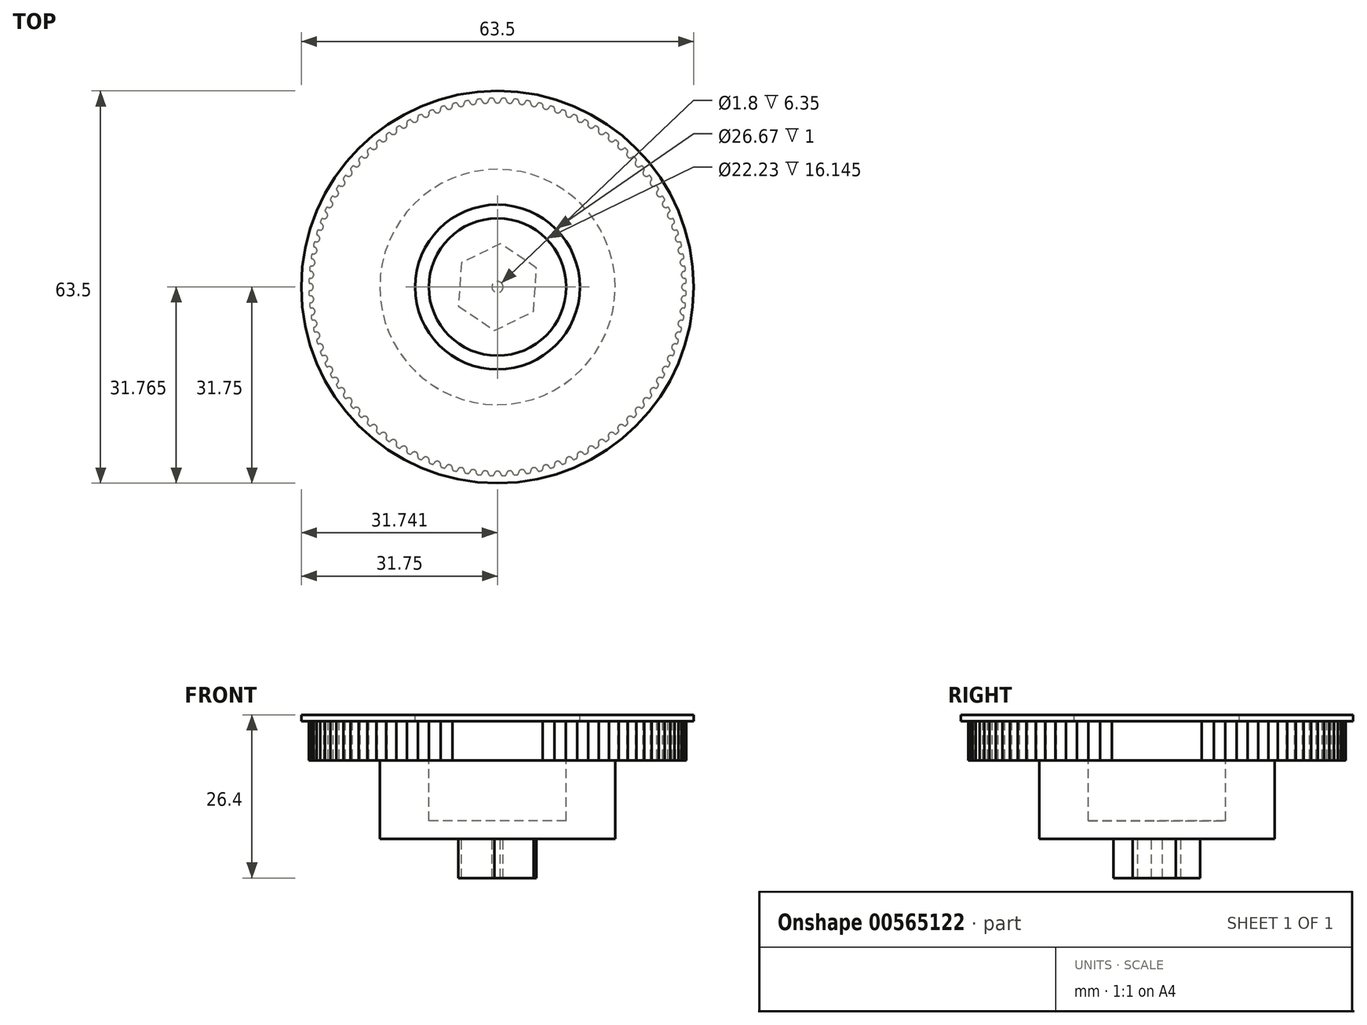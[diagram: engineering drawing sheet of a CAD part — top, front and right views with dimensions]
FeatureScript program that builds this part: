
annotation { "Feature Type Name" : "Feature", "Feature Type Description" : "" }
export const myFeature = defineFeature(function(context is Context, id is Id, definition is map)
    precondition{}
    {
        {
            var Q0;
            Q0=qCreatedBy(makeId("Top.planeOp"),FACE);
            var sketch = newSketch(context, id + "F0", { "sketchPlane" : qUnion([Q0])});
            skArc(sketch, "E0", {"start": v(0, 29.8) * mm, "mid": v(0.3, 29.9) * mm, "end": v(0.5, 30.12) * mm});
            skArc(sketch, "E1", {"start": v(1.47, 30.1) * mm, "mid": v(1.66, 29.85) * mm, "end": v(1.95, 29.74) * mm});
            skArc(sketch, "E2", {"start": v(0.5, 30.12) * mm, "mid": v(0.55, 30.23) * mm, "end": v(0.58, 30.34) * mm});
            skArc(sketch, "E3", {"start": v(1.4, 30.32) * mm, "mid": v(1.43, 30.2) * mm, "end": v(1.47, 30.1) * mm});
            skArc(sketch, "E4.trimOffspring", {"start": v(1.17, 30.53) * mm, "mid": v(1, 30.54) * mm, "end": v(0.83, 30.54) * mm});
            skPoint(sketch, "E5.visualSharp", {"position": v(0.6, 30.55) * mm});
            skArc(sketch, "E5.filletArc", {"start": v(0.83, 30.54) * mm, "mid": v(0.67, 30.5) * mm, "end": v(0.58, 30.34) * mm});
            skPoint(sketch, "E6.visualSharp", {"position": v(1.4, 30.52) * mm});
            skArc(sketch, "E6.filletArc", {"start": v(1.4, 30.32) * mm, "mid": v(1.33, 30.47) * mm, "end": v(1.17, 30.53) * mm});
            skArc(sketch, "E7.1.0", {"start": v(-1.95, 29.74) * mm, "mid": v(-1.66, 29.85) * mm, "end": v(-1.47, 30.1) * mm});
            skArc(sketch, "E7.1.1", {"start": v(-1.47, 30.1) * mm, "mid": v(-1.43, 30.2) * mm, "end": v(-1.4, 30.32) * mm});
            skArc(sketch, "E7.1.2", {"start": v(-1.17, 30.53) * mm, "mid": v(-1.33, 30.47) * mm, "end": v(-1.4, 30.32) * mm});
            skArc(sketch, "E7.1.3", {"start": v(-0.83, 30.54) * mm, "mid": v(-1, 30.54) * mm, "end": v(-1.17, 30.53) * mm});
            skArc(sketch, "E7.1.4", {"start": v(-0.58, 30.34) * mm, "mid": v(-0.67, 30.5) * mm, "end": v(-0.83, 30.54) * mm});
            skArc(sketch, "E7.1.5", {"start": v(-0.58, 30.34) * mm, "mid": v(-0.55, 30.23) * mm, "end": v(-0.5, 30.12) * mm});
            skArc(sketch, "E7.1.6", {"start": v(-0.5, 30.12) * mm, "mid": v(-0.3, 29.9) * mm, "end": v(0, 29.8) * mm});
            skArc(sketch, "E7.2.0", {"start": v(-3.9, 29.55) * mm, "mid": v(-3.6, 29.68) * mm, "end": v(-3.44, 29.93) * mm});
            skArc(sketch, "E7.2.1", {"start": v(-3.44, 29.93) * mm, "mid": v(-3.4, 30.04) * mm, "end": v(-3.39, 30.16) * mm});
            skArc(sketch, "E7.2.2", {"start": v(-3.16, 30.4) * mm, "mid": v(-3.32, 30.32) * mm, "end": v(-3.39, 30.16) * mm});
            skArc(sketch, "E7.2.3", {"start": v(-2.83, 30.43) * mm, "mid": v(-3, 30.4) * mm, "end": v(-3.16, 30.4) * mm});
            skArc(sketch, "E7.2.4", {"start": v(-2.56, 30.24) * mm, "mid": v(-2.66, 30.38) * mm, "end": v(-2.83, 30.43) * mm});
            skArc(sketch, "E7.2.5", {"start": v(-2.56, 30.24) * mm, "mid": v(-2.52, 30.13) * mm, "end": v(-2.47, 30.03) * mm});
            skArc(sketch, "E7.2.6", {"start": v(-2.47, 30.03) * mm, "mid": v(-2.25, 29.8) * mm, "end": v(-1.95, 29.74) * mm});
            skArc(sketch, "E7.3.0", {"start": v(-5.82, 29.23) * mm, "mid": v(-5.54, 29.38) * mm, "end": v(-5.39, 29.64) * mm});
            skArc(sketch, "E7.3.1", {"start": v(-5.39, 29.64) * mm, "mid": v(-5.36, 29.76) * mm, "end": v(-5.35, 29.87) * mm});
            skArc(sketch, "E7.3.2", {"start": v(-5.14, 30.12) * mm, "mid": v(-5.3, 30.04) * mm, "end": v(-5.35, 29.87) * mm});
            skArc(sketch, "E7.3.3", {"start": v(-4.81, 30.18) * mm, "mid": v(-4.98, 30.15) * mm, "end": v(-5.14, 30.12) * mm});
            skArc(sketch, "E7.3.4", {"start": v(-4.53, 30) * mm, "mid": v(-4.64, 30.14) * mm, "end": v(-4.81, 30.18) * mm});
            skArc(sketch, "E7.3.5", {"start": v(-4.53, 30) * mm, "mid": v(-4.49, 29.9) * mm, "end": v(-4.43, 29.8) * mm});
            skArc(sketch, "E7.3.6", {"start": v(-4.43, 29.8) * mm, "mid": v(-4.2, 29.6) * mm, "end": v(-3.9, 29.55) * mm});
            skArc(sketch, "E7.4.0", {"start": v(-7.71, 28.8) * mm, "mid": v(-7.45, 28.95) * mm, "end": v(-7.31, 29.23) * mm});
            skArc(sketch, "E7.4.1", {"start": v(-7.31, 29.23) * mm, "mid": v(-7.3, 29.34) * mm, "end": v(-7.3, 29.46) * mm});
            skArc(sketch, "E7.4.2", {"start": v(-7.1, 29.72) * mm, "mid": v(-7.25, 29.62) * mm, "end": v(-7.3, 29.46) * mm});
            skArc(sketch, "E7.4.3", {"start": v(-6.77, 29.8) * mm, "mid": v(-6.94, 29.76) * mm, "end": v(-7.1, 29.72) * mm});
            skArc(sketch, "E7.4.4", {"start": v(-6.49, 29.65) * mm, "mid": v(-6.6, 29.77) * mm, "end": v(-6.77, 29.8) * mm});
            skArc(sketch, "E7.4.5", {"start": v(-6.49, 29.65) * mm, "mid": v(-6.43, 29.54) * mm, "end": v(-6.37, 29.45) * mm});
            skArc(sketch, "E7.4.6", {"start": v(-6.37, 29.45) * mm, "mid": v(-6.12, 29.26) * mm, "end": v(-5.82, 29.23) * mm});
            skArc(sketch, "E7.5.0", {"start": v(-9.58, 28.23) * mm, "mid": v(-9.33, 28.4) * mm, "end": v(-9.2, 28.69) * mm});
            skArc(sketch, "E7.5.1", {"start": v(-9.2, 28.69) * mm, "mid": v(-9.2, 28.8) * mm, "end": v(-9.2, 28.92) * mm});
            skArc(sketch, "E7.5.2", {"start": v(-9.03, 29.2) * mm, "mid": v(-9.17, 29.09) * mm, "end": v(-9.2, 28.92) * mm});
            skArc(sketch, "E7.5.3", {"start": v(-8.7, 29.29) * mm, "mid": v(-8.87, 29.24) * mm, "end": v(-9.03, 29.2) * mm});
            skArc(sketch, "E7.5.4", {"start": v(-8.41, 29.16) * mm, "mid": v(-8.54, 29.28) * mm, "end": v(-8.7, 29.29) * mm});
            skArc(sketch, "E7.5.5", {"start": v(-8.41, 29.16) * mm, "mid": v(-8.35, 29.06) * mm, "end": v(-8.28, 28.97) * mm});
            skArc(sketch, "E7.5.6", {"start": v(-8.28, 28.97) * mm, "mid": v(-8.02, 28.8) * mm, "end": v(-7.71, 28.8) * mm});
            skArc(sketch, "E7.6.0", {"start": v(-11.4, 27.54) * mm, "mid": v(-11.17, 27.73) * mm, "end": v(-11.06, 28.02) * mm});
            skArc(sketch, "E7.6.1", {"start": v(-11.06, 28.02) * mm, "mid": v(-11.07, 28.14) * mm, "end": v(-11.08, 28.25) * mm});
            skArc(sketch, "E7.6.2", {"start": v(-10.92, 28.54) * mm, "mid": v(-11.05, 28.43) * mm, "end": v(-11.08, 28.25) * mm});
            skArc(sketch, "E7.6.3", {"start": v(-10.6, 28.66) * mm, "mid": v(-10.76, 28.6) * mm, "end": v(-10.92, 28.54) * mm});
            skArc(sketch, "E7.6.4", {"start": v(-10.3, 28.55) * mm, "mid": v(-10.43, 28.66) * mm, "end": v(-10.6, 28.66) * mm});
            skArc(sketch, "E7.6.5", {"start": v(-10.3, 28.55) * mm, "mid": v(-10.23, 28.45) * mm, "end": v(-10.16, 28.36) * mm});
            skArc(sketch, "E7.6.6", {"start": v(-10.16, 28.36) * mm, "mid": v(-9.89, 28.21) * mm, "end": v(-9.58, 28.23) * mm});
            skArc(sketch, "E7.7.0", {"start": v(-13.18, 26.73) * mm, "mid": v(-12.96, 26.94) * mm, "end": v(-12.87, 27.24) * mm});
            skArc(sketch, "E7.7.1", {"start": v(-12.87, 27.24) * mm, "mid": v(-12.88, 27.35) * mm, "end": v(-12.9, 27.47) * mm});
            skArc(sketch, "E7.7.2", {"start": v(-12.76, 27.76) * mm, "mid": v(-12.89, 27.64) * mm, "end": v(-12.9, 27.47) * mm});
            skArc(sketch, "E7.7.3", {"start": v(-12.46, 27.9) * mm, "mid": v(-12.61, 27.83) * mm, "end": v(-12.76, 27.76) * mm});
            skArc(sketch, "E7.7.4", {"start": v(-12.14, 27.81) * mm, "mid": v(-12.29, 27.91) * mm, "end": v(-12.46, 27.9) * mm});
            skArc(sketch, "E7.7.5", {"start": v(-12.14, 27.81) * mm, "mid": v(-12.07, 27.72) * mm, "end": v(-12, 27.64) * mm});
            skArc(sketch, "E7.7.6", {"start": v(-12, 27.64) * mm, "mid": v(-11.71, 27.5) * mm, "end": v(-11.4, 27.54) * mm});
            skArc(sketch, "E7.8.0", {"start": v(-14.9, 25.81) * mm, "mid": v(-14.69, 26.04) * mm, "end": v(-14.63, 26.34) * mm});
            skArc(sketch, "E7.8.1", {"start": v(-14.63, 26.34) * mm, "mid": v(-14.64, 26.45) * mm, "end": v(-14.67, 26.57) * mm});
            skArc(sketch, "E7.8.2", {"start": v(-14.55, 26.87) * mm, "mid": v(-14.67, 26.74) * mm, "end": v(-14.67, 26.57) * mm});
            skArc(sketch, "E7.8.3", {"start": v(-14.26, 27.03) * mm, "mid": v(-14.4, 26.95) * mm, "end": v(-14.55, 26.87) * mm});
            skArc(sketch, "E7.8.4", {"start": v(-13.94, 26.96) * mm, "mid": v(-14.08, 27.05) * mm, "end": v(-14.26, 27.03) * mm});
            skArc(sketch, "E7.8.5", {"start": v(-13.94, 26.96) * mm, "mid": v(-13.86, 26.87) * mm, "end": v(-13.77, 26.8) * mm});
            skArc(sketch, "E7.8.6", {"start": v(-13.77, 26.8) * mm, "mid": v(-13.49, 26.68) * mm, "end": v(-13.18, 26.73) * mm});
            skArc(sketch, "E7.9.0", {"start": v(-16.56, 24.78) * mm, "mid": v(-16.36, 25.02) * mm, "end": v(-16.32, 25.32) * mm});
            skArc(sketch, "E7.9.1", {"start": v(-16.32, 25.32) * mm, "mid": v(-16.34, 25.44) * mm, "end": v(-16.38, 25.55) * mm});
            skArc(sketch, "E7.9.2", {"start": v(-16.28, 25.86) * mm, "mid": v(-16.38, 25.72) * mm, "end": v(-16.38, 25.55) * mm});
            skArc(sketch, "E7.9.3", {"start": v(-16, 26.04) * mm, "mid": v(-16.14, 25.95) * mm, "end": v(-16.28, 25.86) * mm});
            skArc(sketch, "E7.9.4", {"start": v(-15.67, 26) * mm, "mid": v(-15.82, 26.07) * mm, "end": v(-16, 26.04) * mm});
            skArc(sketch, "E7.9.5", {"start": v(-15.67, 26) * mm, "mid": v(-15.59, 25.9) * mm, "end": v(-15.5, 25.84) * mm});
            skArc(sketch, "E7.9.6", {"start": v(-15.5, 25.84) * mm, "mid": v(-15.2, 25.74) * mm, "end": v(-14.9, 25.81) * mm});
            skArc(sketch, "E7.10.0", {"start": v(-18.15, 23.65) * mm, "mid": v(-17.96, 23.9) * mm, "end": v(-17.94, 24.2) * mm});
            skArc(sketch, "E7.10.1", {"start": v(-17.94, 24.2) * mm, "mid": v(-17.97, 24.32) * mm, "end": v(-18.02, 24.42) * mm});
            skArc(sketch, "E7.10.2", {"start": v(-17.93, 24.74) * mm, "mid": v(-18.03, 24.6) * mm, "end": v(-18.02, 24.42) * mm});
            skArc(sketch, "E7.10.3", {"start": v(-17.66, 24.94) * mm, "mid": v(-17.8, 24.84) * mm, "end": v(-17.93, 24.74) * mm});
            skArc(sketch, "E7.10.4", {"start": v(-17.34, 24.91) * mm, "mid": v(-17.5, 24.98) * mm, "end": v(-17.66, 24.94) * mm});
            skArc(sketch, "E7.10.5", {"start": v(-17.34, 24.91) * mm, "mid": v(-17.25, 24.83) * mm, "end": v(-17.15, 24.77) * mm});
            skArc(sketch, "E7.10.6", {"start": v(-17.15, 24.77) * mm, "mid": v(-16.85, 24.7) * mm, "end": v(-16.56, 24.78) * mm});
            skArc(sketch, "E7.11.0", {"start": v(-19.65, 22.41) * mm, "mid": v(-19.49, 22.67) * mm, "end": v(-19.48, 22.98) * mm});
            skArc(sketch, "E7.11.1", {"start": v(-19.48, 22.98) * mm, "mid": v(-19.52, 23.09) * mm, "end": v(-19.57, 23.2) * mm});
            skArc(sketch, "E7.11.2", {"start": v(-19.51, 23.51) * mm, "mid": v(-19.6, 23.36) * mm, "end": v(-19.57, 23.2) * mm});
            skArc(sketch, "E7.11.3", {"start": v(-19.25, 23.73) * mm, "mid": v(-19.38, 23.62) * mm, "end": v(-19.51, 23.51) * mm});
            skArc(sketch, "E7.11.4", {"start": v(-18.93, 23.72) * mm, "mid": v(-19.1, 23.78) * mm, "end": v(-19.25, 23.73) * mm});
            skArc(sketch, "E7.11.5", {"start": v(-18.93, 23.72) * mm, "mid": v(-18.84, 23.65) * mm, "end": v(-18.74, 23.6) * mm});
            skArc(sketch, "E7.11.6", {"start": v(-18.74, 23.6) * mm, "mid": v(-18.43, 23.54) * mm, "end": v(-18.15, 23.65) * mm});
            skArc(sketch, "E7.12.0", {"start": v(-21.08, 21.08) * mm, "mid": v(-20.93, 21.35) * mm, "end": v(-20.95, 21.65) * mm});
            skArc(sketch, "E7.12.1", {"start": v(-20.95, 21.65) * mm, "mid": v(-21, 21.76) * mm, "end": v(-21.05, 21.86) * mm});
            skArc(sketch, "E7.12.2", {"start": v(-21.01, 22.19) * mm, "mid": v(-21.09, 22.03) * mm, "end": v(-21.05, 21.86) * mm});
            skArc(sketch, "E7.12.3", {"start": v(-20.76, 22.42) * mm, "mid": v(-20.89, 22.3) * mm, "end": v(-21.01, 22.19) * mm});
            skArc(sketch, "E7.12.4", {"start": v(-20.44, 22.43) * mm, "mid": v(-20.6, 22.48) * mm, "end": v(-20.76, 22.42) * mm});
            skArc(sketch, "E7.12.5", {"start": v(-20.44, 22.43) * mm, "mid": v(-20.34, 22.37) * mm, "end": v(-20.24, 22.32) * mm});
            skArc(sketch, "E7.12.6", {"start": v(-20.24, 22.32) * mm, "mid": v(-19.93, 22.28) * mm, "end": v(-19.65, 22.41) * mm});
            skArc(sketch, "E7.13.0", {"start": v(-22.41, 19.65) * mm, "mid": v(-22.28, 19.93) * mm, "end": v(-22.32, 20.24) * mm});
            skArc(sketch, "E7.13.1", {"start": v(-22.32, 20.24) * mm, "mid": v(-22.37, 20.34) * mm, "end": v(-22.43, 20.44) * mm});
            skArc(sketch, "E7.13.2", {"start": v(-22.42, 20.76) * mm, "mid": v(-22.48, 20.6) * mm, "end": v(-22.43, 20.44) * mm});
            skArc(sketch, "E7.13.3", {"start": v(-22.19, 21.01) * mm, "mid": v(-22.3, 20.89) * mm, "end": v(-22.42, 20.76) * mm});
            skArc(sketch, "E7.13.4", {"start": v(-21.86, 21.05) * mm, "mid": v(-22.03, 21.09) * mm, "end": v(-22.19, 21.01) * mm});
            skArc(sketch, "E7.13.5", {"start": v(-21.86, 21.05) * mm, "mid": v(-21.76, 21) * mm, "end": v(-21.65, 20.95) * mm});
            skArc(sketch, "E7.13.6", {"start": v(-21.65, 20.95) * mm, "mid": v(-21.35, 20.93) * mm, "end": v(-21.08, 21.08) * mm});
            skArc(sketch, "E7.14.0", {"start": v(-23.65, 18.15) * mm, "mid": v(-23.54, 18.43) * mm, "end": v(-23.6, 18.74) * mm});
            skArc(sketch, "E7.14.1", {"start": v(-23.6, 18.74) * mm, "mid": v(-23.65, 18.84) * mm, "end": v(-23.72, 18.93) * mm});
            skArc(sketch, "E7.14.2", {"start": v(-23.73, 19.25) * mm, "mid": v(-23.78, 19.1) * mm, "end": v(-23.72, 18.93) * mm});
            skArc(sketch, "E7.14.3", {"start": v(-23.51, 19.51) * mm, "mid": v(-23.62, 19.38) * mm, "end": v(-23.73, 19.25) * mm});
            skArc(sketch, "E7.14.4", {"start": v(-23.2, 19.57) * mm, "mid": v(-23.36, 19.6) * mm, "end": v(-23.51, 19.51) * mm});
            skArc(sketch, "E7.14.5", {"start": v(-23.2, 19.57) * mm, "mid": v(-23.09, 19.52) * mm, "end": v(-22.98, 19.48) * mm});
            skArc(sketch, "E7.14.6", {"start": v(-22.98, 19.48) * mm, "mid": v(-22.67, 19.49) * mm, "end": v(-22.41, 19.65) * mm});
            skArc(sketch, "E7.15.0", {"start": v(-24.78, 16.56) * mm, "mid": v(-24.7, 16.85) * mm, "end": v(-24.77, 17.15) * mm});
            skArc(sketch, "E7.15.1", {"start": v(-24.77, 17.15) * mm, "mid": v(-24.83, 17.25) * mm, "end": v(-24.91, 17.34) * mm});
            skArc(sketch, "E7.15.2", {"start": v(-24.94, 17.66) * mm, "mid": v(-24.98, 17.5) * mm, "end": v(-24.91, 17.34) * mm});
            skArc(sketch, "E7.15.3", {"start": v(-24.74, 17.93) * mm, "mid": v(-24.84, 17.8) * mm, "end": v(-24.94, 17.66) * mm});
            skArc(sketch, "E7.15.4", {"start": v(-24.42, 18.02) * mm, "mid": v(-24.6, 18.03) * mm, "end": v(-24.74, 17.93) * mm});
            skArc(sketch, "E7.15.5", {"start": v(-24.42, 18.02) * mm, "mid": v(-24.32, 17.97) * mm, "end": v(-24.2, 17.94) * mm});
            skArc(sketch, "E7.15.6", {"start": v(-24.2, 17.94) * mm, "mid": v(-23.9, 17.96) * mm, "end": v(-23.65, 18.15) * mm});
            skArc(sketch, "E7.16.0", {"start": v(-25.81, 14.9) * mm, "mid": v(-25.74, 15.2) * mm, "end": v(-25.84, 15.5) * mm});
            skArc(sketch, "E7.16.1", {"start": v(-25.84, 15.5) * mm, "mid": v(-25.9, 15.59) * mm, "end": v(-26, 15.67) * mm});
            skArc(sketch, "E7.16.2", {"start": v(-26.04, 16) * mm, "mid": v(-26.07, 15.82) * mm, "end": v(-26, 15.67) * mm});
            skArc(sketch, "E7.16.3", {"start": v(-25.86, 16.28) * mm, "mid": v(-25.95, 16.14) * mm, "end": v(-26.04, 16) * mm});
            skArc(sketch, "E7.16.4", {"start": v(-25.55, 16.38) * mm, "mid": v(-25.72, 16.38) * mm, "end": v(-25.86, 16.28) * mm});
            skArc(sketch, "E7.16.5", {"start": v(-25.55, 16.38) * mm, "mid": v(-25.44, 16.34) * mm, "end": v(-25.32, 16.32) * mm});
            skArc(sketch, "E7.16.6", {"start": v(-25.32, 16.32) * mm, "mid": v(-25.02, 16.36) * mm, "end": v(-24.78, 16.56) * mm});
            skArc(sketch, "E7.17.0", {"start": v(-26.73, 13.18) * mm, "mid": v(-26.68, 13.49) * mm, "end": v(-26.8, 13.77) * mm});
            skArc(sketch, "E7.17.1", {"start": v(-26.8, 13.77) * mm, "mid": v(-26.87, 13.86) * mm, "end": v(-26.96, 13.94) * mm});
            skArc(sketch, "E7.17.2", {"start": v(-27.03, 14.26) * mm, "mid": v(-27.05, 14.08) * mm, "end": v(-26.96, 13.94) * mm});
            skArc(sketch, "E7.17.3", {"start": v(-26.87, 14.55) * mm, "mid": v(-26.95, 14.4) * mm, "end": v(-27.03, 14.26) * mm});
            skArc(sketch, "E7.17.4", {"start": v(-26.57, 14.67) * mm, "mid": v(-26.74, 14.67) * mm, "end": v(-26.87, 14.55) * mm});
            skArc(sketch, "E7.17.5", {"start": v(-26.57, 14.67) * mm, "mid": v(-26.45, 14.64) * mm, "end": v(-26.34, 14.63) * mm});
            skArc(sketch, "E7.17.6", {"start": v(-26.34, 14.63) * mm, "mid": v(-26.04, 14.69) * mm, "end": v(-25.81, 14.9) * mm});
            skArc(sketch, "E7.18.0", {"start": v(-27.54, 11.4) * mm, "mid": v(-27.5, 11.71) * mm, "end": v(-27.64, 12) * mm});
            skArc(sketch, "E7.18.1", {"start": v(-27.64, 12) * mm, "mid": v(-27.72, 12.07) * mm, "end": v(-27.81, 12.14) * mm});
            skArc(sketch, "E7.18.2", {"start": v(-27.9, 12.46) * mm, "mid": v(-27.91, 12.29) * mm, "end": v(-27.81, 12.14) * mm});
            skArc(sketch, "E7.18.3", {"start": v(-27.76, 12.76) * mm, "mid": v(-27.83, 12.61) * mm, "end": v(-27.9, 12.46) * mm});
            skArc(sketch, "E7.18.4", {"start": v(-27.47, 12.9) * mm, "mid": v(-27.64, 12.89) * mm, "end": v(-27.76, 12.76) * mm});
            skArc(sketch, "E7.18.5", {"start": v(-27.47, 12.9) * mm, "mid": v(-27.35, 12.88) * mm, "end": v(-27.24, 12.87) * mm});
            skArc(sketch, "E7.18.6", {"start": v(-27.24, 12.87) * mm, "mid": v(-26.94, 12.96) * mm, "end": v(-26.73, 13.18) * mm});
            skArc(sketch, "E7.19.0", {"start": v(-28.23, 9.58) * mm, "mid": v(-28.21, 9.89) * mm, "end": v(-28.36, 10.16) * mm});
            skArc(sketch, "E7.19.1", {"start": v(-28.36, 10.16) * mm, "mid": v(-28.45, 10.23) * mm, "end": v(-28.55, 10.3) * mm});
            skArc(sketch, "E7.19.2", {"start": v(-28.66, 10.6) * mm, "mid": v(-28.66, 10.43) * mm, "end": v(-28.55, 10.3) * mm});
            skArc(sketch, "E7.19.3", {"start": v(-28.54, 10.92) * mm, "mid": v(-28.6, 10.76) * mm, "end": v(-28.66, 10.6) * mm});
            skArc(sketch, "E7.19.4", {"start": v(-28.25, 11.08) * mm, "mid": v(-28.43, 11.05) * mm, "end": v(-28.54, 10.92) * mm});
            skArc(sketch, "E7.19.5", {"start": v(-28.25, 11.08) * mm, "mid": v(-28.14, 11.07) * mm, "end": v(-28.02, 11.06) * mm});
            skArc(sketch, "E7.19.6", {"start": v(-28.02, 11.06) * mm, "mid": v(-27.73, 11.17) * mm, "end": v(-27.54, 11.4) * mm});
            skArc(sketch, "E7.20.0", {"start": v(-28.8, 7.71) * mm, "mid": v(-28.8, 8.02) * mm, "end": v(-28.97, 8.28) * mm});
            skArc(sketch, "E7.20.1", {"start": v(-28.97, 8.28) * mm, "mid": v(-29.06, 8.35) * mm, "end": v(-29.16, 8.41) * mm});
            skArc(sketch, "E7.20.2", {"start": v(-29.29, 8.7) * mm, "mid": v(-29.28, 8.54) * mm, "end": v(-29.16, 8.41) * mm});
            skArc(sketch, "E7.20.3", {"start": v(-29.2, 9.03) * mm, "mid": v(-29.24, 8.87) * mm, "end": v(-29.29, 8.7) * mm});
            skArc(sketch, "E7.20.4", {"start": v(-28.92, 9.2) * mm, "mid": v(-29.09, 9.17) * mm, "end": v(-29.2, 9.03) * mm});
            skArc(sketch, "E7.20.5", {"start": v(-28.92, 9.2) * mm, "mid": v(-28.8, 9.2) * mm, "end": v(-28.69, 9.2) * mm});
            skArc(sketch, "E7.20.6", {"start": v(-28.69, 9.2) * mm, "mid": v(-28.4, 9.33) * mm, "end": v(-28.23, 9.58) * mm});
            skArc(sketch, "E7.21.0", {"start": v(-29.23, 5.82) * mm, "mid": v(-29.26, 6.12) * mm, "end": v(-29.45, 6.37) * mm});
            skArc(sketch, "E7.21.1", {"start": v(-29.45, 6.37) * mm, "mid": v(-29.54, 6.43) * mm, "end": v(-29.65, 6.49) * mm});
            skArc(sketch, "E7.21.2", {"start": v(-29.8, 6.77) * mm, "mid": v(-29.77, 6.6) * mm, "end": v(-29.65, 6.49) * mm});
            skArc(sketch, "E7.21.3", {"start": v(-29.72, 7.1) * mm, "mid": v(-29.76, 6.94) * mm, "end": v(-29.8, 6.77) * mm});
            skArc(sketch, "E7.21.4", {"start": v(-29.46, 7.3) * mm, "mid": v(-29.62, 7.25) * mm, "end": v(-29.72, 7.1) * mm});
            skArc(sketch, "E7.21.5", {"start": v(-29.46, 7.3) * mm, "mid": v(-29.34, 7.3) * mm, "end": v(-29.23, 7.31) * mm});
            skArc(sketch, "E7.21.6", {"start": v(-29.23, 7.31) * mm, "mid": v(-28.95, 7.45) * mm, "end": v(-28.8, 7.71) * mm});
            skArc(sketch, "E7.22.0", {"start": v(-29.55, 3.9) * mm, "mid": v(-29.6, 4.2) * mm, "end": v(-29.8, 4.43) * mm});
            skArc(sketch, "E7.22.1", {"start": v(-29.8, 4.43) * mm, "mid": v(-29.9, 4.49) * mm, "end": v(-30, 4.53) * mm});
            skArc(sketch, "E7.22.2", {"start": v(-30.18, 4.81) * mm, "mid": v(-30.14, 4.64) * mm, "end": v(-30, 4.53) * mm});
            skArc(sketch, "E7.22.3", {"start": v(-30.12, 5.14) * mm, "mid": v(-30.15, 4.98) * mm, "end": v(-30.18, 4.81) * mm});
            skArc(sketch, "E7.22.4", {"start": v(-29.87, 5.35) * mm, "mid": v(-30.04, 5.3) * mm, "end": v(-30.12, 5.14) * mm});
            skArc(sketch, "E7.22.5", {"start": v(-29.87, 5.35) * mm, "mid": v(-29.76, 5.36) * mm, "end": v(-29.64, 5.39) * mm});
            skArc(sketch, "E7.22.6", {"start": v(-29.64, 5.39) * mm, "mid": v(-29.38, 5.54) * mm, "end": v(-29.23, 5.82) * mm});
            skArc(sketch, "E7.23.0", {"start": v(-29.74, 1.95) * mm, "mid": v(-29.8, 2.25) * mm, "end": v(-30.03, 2.47) * mm});
            skArc(sketch, "E7.23.1", {"start": v(-30.03, 2.47) * mm, "mid": v(-30.13, 2.52) * mm, "end": v(-30.24, 2.56) * mm});
            skArc(sketch, "E7.23.2", {"start": v(-30.43, 2.83) * mm, "mid": v(-30.38, 2.66) * mm, "end": v(-30.24, 2.56) * mm});
            skArc(sketch, "E7.23.3", {"start": v(-30.4, 3.16) * mm, "mid": v(-30.4, 3) * mm, "end": v(-30.43, 2.83) * mm});
            skArc(sketch, "E7.23.4", {"start": v(-30.16, 3.39) * mm, "mid": v(-30.32, 3.32) * mm, "end": v(-30.4, 3.16) * mm});
            skArc(sketch, "E7.23.5", {"start": v(-30.16, 3.39) * mm, "mid": v(-30.04, 3.4) * mm, "end": v(-29.93, 3.44) * mm});
            skArc(sketch, "E7.23.6", {"start": v(-29.93, 3.44) * mm, "mid": v(-29.68, 3.6) * mm, "end": v(-29.55, 3.9) * mm});
            skArc(sketch, "E7.24.0", {"start": v(-29.8, 0) * mm, "mid": v(-29.9, 0.3) * mm, "end": v(-30.12, 0.5) * mm});
            skArc(sketch, "E7.24.1", {"start": v(-30.12, 0.5) * mm, "mid": v(-30.23, 0.55) * mm, "end": v(-30.34, 0.58) * mm});
            skArc(sketch, "E7.24.2", {"start": v(-30.54, 0.83) * mm, "mid": v(-30.5, 0.67) * mm, "end": v(-30.34, 0.58) * mm});
            skArc(sketch, "E7.24.3", {"start": v(-30.53, 1.17) * mm, "mid": v(-30.54, 1) * mm, "end": v(-30.54, 0.83) * mm});
            skArc(sketch, "E7.24.4", {"start": v(-30.32, 1.4) * mm, "mid": v(-30.47, 1.33) * mm, "end": v(-30.53, 1.17) * mm});
            skArc(sketch, "E7.24.5", {"start": v(-30.32, 1.4) * mm, "mid": v(-30.2, 1.43) * mm, "end": v(-30.1, 1.47) * mm});
            skArc(sketch, "E7.24.6", {"start": v(-30.1, 1.47) * mm, "mid": v(-29.85, 1.66) * mm, "end": v(-29.74, 1.95) * mm});
            skArc(sketch, "E7.25.0", {"start": v(-29.74, -1.95) * mm, "mid": v(-29.85, -1.66) * mm, "end": v(-30.1, -1.47) * mm});
            skArc(sketch, "E7.25.1", {"start": v(-30.1, -1.47) * mm, "mid": v(-30.2, -1.43) * mm, "end": v(-30.32, -1.4) * mm});
            skArc(sketch, "E7.25.2", {"start": v(-30.53, -1.17) * mm, "mid": v(-30.47, -1.33) * mm, "end": v(-30.32, -1.4) * mm});
            skArc(sketch, "E7.25.3", {"start": v(-30.54, -0.83) * mm, "mid": v(-30.54, -1) * mm, "end": v(-30.53, -1.17) * mm});
            skArc(sketch, "E7.25.4", {"start": v(-30.34, -0.58) * mm, "mid": v(-30.5, -0.67) * mm, "end": v(-30.54, -0.83) * mm});
            skArc(sketch, "E7.25.5", {"start": v(-30.34, -0.58) * mm, "mid": v(-30.23, -0.55) * mm, "end": v(-30.12, -0.5) * mm});
            skArc(sketch, "E7.25.6", {"start": v(-30.12, -0.5) * mm, "mid": v(-29.9, -0.3) * mm, "end": v(-29.8, 0) * mm});
            skArc(sketch, "E7.26.0", {"start": v(-29.55, -3.9) * mm, "mid": v(-29.68, -3.6) * mm, "end": v(-29.93, -3.44) * mm});
            skArc(sketch, "E7.26.1", {"start": v(-29.93, -3.44) * mm, "mid": v(-30.04, -3.4) * mm, "end": v(-30.16, -3.39) * mm});
            skArc(sketch, "E7.26.2", {"start": v(-30.4, -3.16) * mm, "mid": v(-30.32, -3.32) * mm, "end": v(-30.16, -3.39) * mm});
            skArc(sketch, "E7.26.3", {"start": v(-30.43, -2.83) * mm, "mid": v(-30.4, -3) * mm, "end": v(-30.4, -3.16) * mm});
            skArc(sketch, "E7.26.4", {"start": v(-30.24, -2.56) * mm, "mid": v(-30.38, -2.66) * mm, "end": v(-30.43, -2.83) * mm});
            skArc(sketch, "E7.26.5", {"start": v(-30.24, -2.56) * mm, "mid": v(-30.13, -2.52) * mm, "end": v(-30.03, -2.47) * mm});
            skArc(sketch, "E7.26.6", {"start": v(-30.03, -2.47) * mm, "mid": v(-29.8, -2.25) * mm, "end": v(-29.74, -1.95) * mm});
            skArc(sketch, "E7.27.0", {"start": v(-29.23, -5.82) * mm, "mid": v(-29.38, -5.54) * mm, "end": v(-29.64, -5.39) * mm});
            skArc(sketch, "E7.27.1", {"start": v(-29.64, -5.39) * mm, "mid": v(-29.76, -5.36) * mm, "end": v(-29.87, -5.35) * mm});
            skArc(sketch, "E7.27.2", {"start": v(-30.12, -5.14) * mm, "mid": v(-30.04, -5.3) * mm, "end": v(-29.87, -5.35) * mm});
            skArc(sketch, "E7.27.3", {"start": v(-30.18, -4.81) * mm, "mid": v(-30.15, -4.98) * mm, "end": v(-30.12, -5.14) * mm});
            skArc(sketch, "E7.27.4", {"start": v(-30, -4.53) * mm, "mid": v(-30.14, -4.64) * mm, "end": v(-30.18, -4.81) * mm});
            skArc(sketch, "E7.27.5", {"start": v(-30, -4.53) * mm, "mid": v(-29.9, -4.49) * mm, "end": v(-29.8, -4.43) * mm});
            skArc(sketch, "E7.27.6", {"start": v(-29.8, -4.43) * mm, "mid": v(-29.6, -4.2) * mm, "end": v(-29.55, -3.9) * mm});
            skArc(sketch, "E7.28.0", {"start": v(-28.8, -7.71) * mm, "mid": v(-28.95, -7.45) * mm, "end": v(-29.23, -7.31) * mm});
            skArc(sketch, "E7.28.1", {"start": v(-29.23, -7.31) * mm, "mid": v(-29.34, -7.3) * mm, "end": v(-29.46, -7.3) * mm});
            skArc(sketch, "E7.28.2", {"start": v(-29.72, -7.1) * mm, "mid": v(-29.62, -7.25) * mm, "end": v(-29.46, -7.3) * mm});
            skArc(sketch, "E7.28.3", {"start": v(-29.8, -6.77) * mm, "mid": v(-29.76, -6.94) * mm, "end": v(-29.72, -7.1) * mm});
            skArc(sketch, "E7.28.4", {"start": v(-29.65, -6.49) * mm, "mid": v(-29.77, -6.6) * mm, "end": v(-29.8, -6.77) * mm});
            skArc(sketch, "E7.28.5", {"start": v(-29.65, -6.49) * mm, "mid": v(-29.54, -6.43) * mm, "end": v(-29.45, -6.37) * mm});
            skArc(sketch, "E7.28.6", {"start": v(-29.45, -6.37) * mm, "mid": v(-29.26, -6.12) * mm, "end": v(-29.23, -5.82) * mm});
            skArc(sketch, "E7.29.0", {"start": v(-28.23, -9.58) * mm, "mid": v(-28.4, -9.33) * mm, "end": v(-28.69, -9.2) * mm});
            skArc(sketch, "E7.29.1", {"start": v(-28.69, -9.2) * mm, "mid": v(-28.8, -9.2) * mm, "end": v(-28.92, -9.2) * mm});
            skArc(sketch, "E7.29.2", {"start": v(-29.2, -9.03) * mm, "mid": v(-29.09, -9.17) * mm, "end": v(-28.92, -9.2) * mm});
            skArc(sketch, "E7.29.3", {"start": v(-29.29, -8.7) * mm, "mid": v(-29.24, -8.87) * mm, "end": v(-29.2, -9.03) * mm});
            skArc(sketch, "E7.29.4", {"start": v(-29.16, -8.41) * mm, "mid": v(-29.28, -8.54) * mm, "end": v(-29.29, -8.7) * mm});
            skArc(sketch, "E7.29.5", {"start": v(-29.16, -8.41) * mm, "mid": v(-29.06, -8.35) * mm, "end": v(-28.97, -8.28) * mm});
            skArc(sketch, "E7.29.6", {"start": v(-28.97, -8.28) * mm, "mid": v(-28.8, -8.02) * mm, "end": v(-28.8, -7.71) * mm});
            skArc(sketch, "E7.30.0", {"start": v(-27.54, -11.4) * mm, "mid": v(-27.73, -11.17) * mm, "end": v(-28.02, -11.06) * mm});
            skArc(sketch, "E7.30.1", {"start": v(-28.02, -11.06) * mm, "mid": v(-28.14, -11.07) * mm, "end": v(-28.25, -11.08) * mm});
            skArc(sketch, "E7.30.2", {"start": v(-28.54, -10.92) * mm, "mid": v(-28.43, -11.05) * mm, "end": v(-28.25, -11.08) * mm});
            skArc(sketch, "E7.30.3", {"start": v(-28.66, -10.6) * mm, "mid": v(-28.6, -10.76) * mm, "end": v(-28.54, -10.92) * mm});
            skArc(sketch, "E7.30.4", {"start": v(-28.55, -10.3) * mm, "mid": v(-28.66, -10.43) * mm, "end": v(-28.66, -10.6) * mm});
            skArc(sketch, "E7.30.5", {"start": v(-28.55, -10.3) * mm, "mid": v(-28.45, -10.23) * mm, "end": v(-28.36, -10.16) * mm});
            skArc(sketch, "E7.30.6", {"start": v(-28.36, -10.16) * mm, "mid": v(-28.21, -9.89) * mm, "end": v(-28.23, -9.58) * mm});
            skArc(sketch, "E7.31.0", {"start": v(-26.73, -13.18) * mm, "mid": v(-26.94, -12.96) * mm, "end": v(-27.24, -12.87) * mm});
            skArc(sketch, "E7.31.1", {"start": v(-27.24, -12.87) * mm, "mid": v(-27.35, -12.88) * mm, "end": v(-27.47, -12.9) * mm});
            skArc(sketch, "E7.31.2", {"start": v(-27.76, -12.76) * mm, "mid": v(-27.64, -12.89) * mm, "end": v(-27.47, -12.9) * mm});
            skArc(sketch, "E7.31.3", {"start": v(-27.9, -12.46) * mm, "mid": v(-27.83, -12.61) * mm, "end": v(-27.76, -12.76) * mm});
            skArc(sketch, "E7.31.4", {"start": v(-27.81, -12.14) * mm, "mid": v(-27.91, -12.29) * mm, "end": v(-27.9, -12.46) * mm});
            skArc(sketch, "E7.31.5", {"start": v(-27.81, -12.14) * mm, "mid": v(-27.72, -12.07) * mm, "end": v(-27.64, -12) * mm});
            skArc(sketch, "E7.31.6", {"start": v(-27.64, -12) * mm, "mid": v(-27.5, -11.71) * mm, "end": v(-27.54, -11.4) * mm});
            skArc(sketch, "E7.32.0", {"start": v(-25.81, -14.9) * mm, "mid": v(-26.04, -14.69) * mm, "end": v(-26.34, -14.63) * mm});
            skArc(sketch, "E7.32.1", {"start": v(-26.34, -14.63) * mm, "mid": v(-26.45, -14.64) * mm, "end": v(-26.57, -14.67) * mm});
            skArc(sketch, "E7.32.2", {"start": v(-26.87, -14.55) * mm, "mid": v(-26.74, -14.67) * mm, "end": v(-26.57, -14.67) * mm});
            skArc(sketch, "E7.32.3", {"start": v(-27.03, -14.26) * mm, "mid": v(-26.95, -14.4) * mm, "end": v(-26.87, -14.55) * mm});
            skArc(sketch, "E7.32.4", {"start": v(-26.96, -13.94) * mm, "mid": v(-27.05, -14.08) * mm, "end": v(-27.03, -14.26) * mm});
            skArc(sketch, "E7.32.5", {"start": v(-26.96, -13.94) * mm, "mid": v(-26.87, -13.86) * mm, "end": v(-26.8, -13.77) * mm});
            skArc(sketch, "E7.32.6", {"start": v(-26.8, -13.77) * mm, "mid": v(-26.68, -13.49) * mm, "end": v(-26.73, -13.18) * mm});
            skArc(sketch, "E7.33.0", {"start": v(-24.78, -16.56) * mm, "mid": v(-25.02, -16.36) * mm, "end": v(-25.32, -16.32) * mm});
            skArc(sketch, "E7.33.1", {"start": v(-25.32, -16.32) * mm, "mid": v(-25.44, -16.34) * mm, "end": v(-25.55, -16.38) * mm});
            skArc(sketch, "E7.33.2", {"start": v(-25.86, -16.28) * mm, "mid": v(-25.72, -16.38) * mm, "end": v(-25.55, -16.38) * mm});
            skArc(sketch, "E7.33.3", {"start": v(-26.04, -16) * mm, "mid": v(-25.95, -16.14) * mm, "end": v(-25.86, -16.28) * mm});
            skArc(sketch, "E7.33.4", {"start": v(-26, -15.67) * mm, "mid": v(-26.07, -15.82) * mm, "end": v(-26.04, -16) * mm});
            skArc(sketch, "E7.33.5", {"start": v(-26, -15.67) * mm, "mid": v(-25.9, -15.59) * mm, "end": v(-25.84, -15.5) * mm});
            skArc(sketch, "E7.33.6", {"start": v(-25.84, -15.5) * mm, "mid": v(-25.74, -15.2) * mm, "end": v(-25.81, -14.9) * mm});
            skArc(sketch, "E7.34.0", {"start": v(-23.65, -18.15) * mm, "mid": v(-23.9, -17.96) * mm, "end": v(-24.2, -17.94) * mm});
            skArc(sketch, "E7.34.1", {"start": v(-24.2, -17.94) * mm, "mid": v(-24.32, -17.97) * mm, "end": v(-24.42, -18.02) * mm});
            skArc(sketch, "E7.34.2", {"start": v(-24.74, -17.93) * mm, "mid": v(-24.6, -18.03) * mm, "end": v(-24.42, -18.02) * mm});
            skArc(sketch, "E7.34.3", {"start": v(-24.94, -17.66) * mm, "mid": v(-24.84, -17.8) * mm, "end": v(-24.74, -17.93) * mm});
            skArc(sketch, "E7.34.4", {"start": v(-24.91, -17.34) * mm, "mid": v(-24.98, -17.5) * mm, "end": v(-24.94, -17.66) * mm});
            skArc(sketch, "E7.34.5", {"start": v(-24.91, -17.34) * mm, "mid": v(-24.83, -17.25) * mm, "end": v(-24.77, -17.15) * mm});
            skArc(sketch, "E7.34.6", {"start": v(-24.77, -17.15) * mm, "mid": v(-24.7, -16.85) * mm, "end": v(-24.78, -16.56) * mm});
            skArc(sketch, "E7.35.0", {"start": v(-22.41, -19.65) * mm, "mid": v(-22.67, -19.49) * mm, "end": v(-22.98, -19.48) * mm});
            skArc(sketch, "E7.35.1", {"start": v(-22.98, -19.48) * mm, "mid": v(-23.09, -19.52) * mm, "end": v(-23.2, -19.57) * mm});
            skArc(sketch, "E7.35.2", {"start": v(-23.51, -19.51) * mm, "mid": v(-23.36, -19.6) * mm, "end": v(-23.2, -19.57) * mm});
            skArc(sketch, "E7.35.3", {"start": v(-23.73, -19.25) * mm, "mid": v(-23.62, -19.38) * mm, "end": v(-23.51, -19.51) * mm});
            skArc(sketch, "E7.35.4", {"start": v(-23.72, -18.93) * mm, "mid": v(-23.78, -19.1) * mm, "end": v(-23.73, -19.25) * mm});
            skArc(sketch, "E7.35.5", {"start": v(-23.72, -18.93) * mm, "mid": v(-23.65, -18.84) * mm, "end": v(-23.6, -18.74) * mm});
            skArc(sketch, "E7.35.6", {"start": v(-23.6, -18.74) * mm, "mid": v(-23.54, -18.43) * mm, "end": v(-23.65, -18.15) * mm});
            skArc(sketch, "E7.36.0", {"start": v(-21.08, -21.08) * mm, "mid": v(-21.35, -20.93) * mm, "end": v(-21.65, -20.95) * mm});
            skArc(sketch, "E7.36.1", {"start": v(-21.65, -20.95) * mm, "mid": v(-21.76, -21) * mm, "end": v(-21.86, -21.05) * mm});
            skArc(sketch, "E7.36.2", {"start": v(-22.19, -21.01) * mm, "mid": v(-22.03, -21.09) * mm, "end": v(-21.86, -21.05) * mm});
            skArc(sketch, "E7.36.3", {"start": v(-22.42, -20.76) * mm, "mid": v(-22.3, -20.89) * mm, "end": v(-22.19, -21.01) * mm});
            skArc(sketch, "E7.36.4", {"start": v(-22.43, -20.44) * mm, "mid": v(-22.48, -20.6) * mm, "end": v(-22.42, -20.76) * mm});
            skArc(sketch, "E7.36.5", {"start": v(-22.43, -20.44) * mm, "mid": v(-22.37, -20.34) * mm, "end": v(-22.32, -20.24) * mm});
            skArc(sketch, "E7.36.6", {"start": v(-22.32, -20.24) * mm, "mid": v(-22.28, -19.93) * mm, "end": v(-22.41, -19.65) * mm});
            skArc(sketch, "E7.37.0", {"start": v(-19.65, -22.41) * mm, "mid": v(-19.93, -22.28) * mm, "end": v(-20.24, -22.32) * mm});
            skArc(sketch, "E7.37.1", {"start": v(-20.24, -22.32) * mm, "mid": v(-20.34, -22.37) * mm, "end": v(-20.44, -22.43) * mm});
            skArc(sketch, "E7.37.2", {"start": v(-20.76, -22.42) * mm, "mid": v(-20.6, -22.48) * mm, "end": v(-20.44, -22.43) * mm});
            skArc(sketch, "E7.37.3", {"start": v(-21.01, -22.19) * mm, "mid": v(-20.89, -22.3) * mm, "end": v(-20.76, -22.42) * mm});
            skArc(sketch, "E7.37.4", {"start": v(-21.05, -21.86) * mm, "mid": v(-21.09, -22.03) * mm, "end": v(-21.01, -22.19) * mm});
            skArc(sketch, "E7.37.5", {"start": v(-21.05, -21.86) * mm, "mid": v(-21, -21.76) * mm, "end": v(-20.95, -21.65) * mm});
            skArc(sketch, "E7.37.6", {"start": v(-20.95, -21.65) * mm, "mid": v(-20.93, -21.35) * mm, "end": v(-21.08, -21.08) * mm});
            skArc(sketch, "E7.38.0", {"start": v(-18.15, -23.65) * mm, "mid": v(-18.43, -23.54) * mm, "end": v(-18.74, -23.6) * mm});
            skArc(sketch, "E7.38.1", {"start": v(-18.74, -23.6) * mm, "mid": v(-18.84, -23.65) * mm, "end": v(-18.93, -23.72) * mm});
            skArc(sketch, "E7.38.2", {"start": v(-19.25, -23.73) * mm, "mid": v(-19.1, -23.78) * mm, "end": v(-18.93, -23.72) * mm});
            skArc(sketch, "E7.38.3", {"start": v(-19.51, -23.51) * mm, "mid": v(-19.38, -23.62) * mm, "end": v(-19.25, -23.73) * mm});
            skArc(sketch, "E7.38.4", {"start": v(-19.57, -23.2) * mm, "mid": v(-19.6, -23.36) * mm, "end": v(-19.51, -23.51) * mm});
            skArc(sketch, "E7.38.5", {"start": v(-19.57, -23.2) * mm, "mid": v(-19.52, -23.09) * mm, "end": v(-19.48, -22.98) * mm});
            skArc(sketch, "E7.38.6", {"start": v(-19.48, -22.98) * mm, "mid": v(-19.49, -22.67) * mm, "end": v(-19.65, -22.41) * mm});
            skArc(sketch, "E7.39.0", {"start": v(-16.56, -24.78) * mm, "mid": v(-16.85, -24.7) * mm, "end": v(-17.15, -24.77) * mm});
            skArc(sketch, "E7.39.1", {"start": v(-17.15, -24.77) * mm, "mid": v(-17.25, -24.83) * mm, "end": v(-17.34, -24.91) * mm});
            skArc(sketch, "E7.39.2", {"start": v(-17.66, -24.94) * mm, "mid": v(-17.5, -24.98) * mm, "end": v(-17.34, -24.91) * mm});
            skArc(sketch, "E7.39.3", {"start": v(-17.93, -24.74) * mm, "mid": v(-17.8, -24.84) * mm, "end": v(-17.66, -24.94) * mm});
            skArc(sketch, "E7.39.4", {"start": v(-18.02, -24.42) * mm, "mid": v(-18.03, -24.6) * mm, "end": v(-17.93, -24.74) * mm});
            skArc(sketch, "E7.39.5", {"start": v(-18.02, -24.42) * mm, "mid": v(-17.97, -24.32) * mm, "end": v(-17.94, -24.2) * mm});
            skArc(sketch, "E7.39.6", {"start": v(-17.94, -24.2) * mm, "mid": v(-17.96, -23.9) * mm, "end": v(-18.15, -23.65) * mm});
            skArc(sketch, "E7.40.0", {"start": v(-14.9, -25.81) * mm, "mid": v(-15.2, -25.74) * mm, "end": v(-15.5, -25.84) * mm});
            skArc(sketch, "E7.40.1", {"start": v(-15.5, -25.84) * mm, "mid": v(-15.59, -25.9) * mm, "end": v(-15.67, -26) * mm});
            skArc(sketch, "E7.40.2", {"start": v(-16, -26.04) * mm, "mid": v(-15.82, -26.07) * mm, "end": v(-15.67, -26) * mm});
            skArc(sketch, "E7.40.3", {"start": v(-16.28, -25.86) * mm, "mid": v(-16.14, -25.95) * mm, "end": v(-16, -26.04) * mm});
            skArc(sketch, "E7.40.4", {"start": v(-16.38, -25.55) * mm, "mid": v(-16.38, -25.72) * mm, "end": v(-16.28, -25.86) * mm});
            skArc(sketch, "E7.40.5", {"start": v(-16.38, -25.55) * mm, "mid": v(-16.34, -25.44) * mm, "end": v(-16.32, -25.32) * mm});
            skArc(sketch, "E7.40.6", {"start": v(-16.32, -25.32) * mm, "mid": v(-16.36, -25.02) * mm, "end": v(-16.56, -24.78) * mm});
            skArc(sketch, "E7.41.0", {"start": v(-13.18, -26.73) * mm, "mid": v(-13.49, -26.68) * mm, "end": v(-13.77, -26.8) * mm});
            skArc(sketch, "E7.41.1", {"start": v(-13.77, -26.8) * mm, "mid": v(-13.86, -26.87) * mm, "end": v(-13.94, -26.96) * mm});
            skArc(sketch, "E7.41.2", {"start": v(-14.26, -27.03) * mm, "mid": v(-14.08, -27.05) * mm, "end": v(-13.94, -26.96) * mm});
            skArc(sketch, "E7.41.3", {"start": v(-14.55, -26.87) * mm, "mid": v(-14.4, -26.95) * mm, "end": v(-14.26, -27.03) * mm});
            skArc(sketch, "E7.41.4", {"start": v(-14.67, -26.57) * mm, "mid": v(-14.67, -26.74) * mm, "end": v(-14.55, -26.87) * mm});
            skArc(sketch, "E7.41.5", {"start": v(-14.67, -26.57) * mm, "mid": v(-14.64, -26.45) * mm, "end": v(-14.63, -26.34) * mm});
            skArc(sketch, "E7.41.6", {"start": v(-14.63, -26.34) * mm, "mid": v(-14.69, -26.04) * mm, "end": v(-14.9, -25.81) * mm});
            skArc(sketch, "E7.42.0", {"start": v(-11.4, -27.54) * mm, "mid": v(-11.71, -27.5) * mm, "end": v(-12, -27.64) * mm});
            skArc(sketch, "E7.42.1", {"start": v(-12, -27.64) * mm, "mid": v(-12.07, -27.72) * mm, "end": v(-12.14, -27.81) * mm});
            skArc(sketch, "E7.42.2", {"start": v(-12.46, -27.9) * mm, "mid": v(-12.29, -27.91) * mm, "end": v(-12.14, -27.81) * mm});
            skArc(sketch, "E7.42.3", {"start": v(-12.76, -27.76) * mm, "mid": v(-12.61, -27.83) * mm, "end": v(-12.46, -27.9) * mm});
            skArc(sketch, "E7.42.4", {"start": v(-12.9, -27.47) * mm, "mid": v(-12.89, -27.64) * mm, "end": v(-12.76, -27.76) * mm});
            skArc(sketch, "E7.42.5", {"start": v(-12.9, -27.47) * mm, "mid": v(-12.88, -27.35) * mm, "end": v(-12.87, -27.24) * mm});
            skArc(sketch, "E7.42.6", {"start": v(-12.87, -27.24) * mm, "mid": v(-12.96, -26.94) * mm, "end": v(-13.18, -26.73) * mm});
            skArc(sketch, "E7.43.0", {"start": v(-9.58, -28.23) * mm, "mid": v(-9.89, -28.21) * mm, "end": v(-10.16, -28.36) * mm});
            skArc(sketch, "E7.43.1", {"start": v(-10.16, -28.36) * mm, "mid": v(-10.23, -28.45) * mm, "end": v(-10.3, -28.55) * mm});
            skArc(sketch, "E7.43.2", {"start": v(-10.6, -28.66) * mm, "mid": v(-10.43, -28.66) * mm, "end": v(-10.3, -28.55) * mm});
            skArc(sketch, "E7.43.3", {"start": v(-10.92, -28.54) * mm, "mid": v(-10.76, -28.6) * mm, "end": v(-10.6, -28.66) * mm});
            skArc(sketch, "E7.43.4", {"start": v(-11.08, -28.25) * mm, "mid": v(-11.05, -28.43) * mm, "end": v(-10.92, -28.54) * mm});
            skArc(sketch, "E7.43.5", {"start": v(-11.08, -28.25) * mm, "mid": v(-11.07, -28.14) * mm, "end": v(-11.06, -28.02) * mm});
            skArc(sketch, "E7.43.6", {"start": v(-11.06, -28.02) * mm, "mid": v(-11.17, -27.73) * mm, "end": v(-11.4, -27.54) * mm});
            skArc(sketch, "E7.44.0", {"start": v(-7.71, -28.8) * mm, "mid": v(-8.02, -28.8) * mm, "end": v(-8.28, -28.97) * mm});
            skArc(sketch, "E7.44.1", {"start": v(-8.28, -28.97) * mm, "mid": v(-8.35, -29.06) * mm, "end": v(-8.41, -29.16) * mm});
            skArc(sketch, "E7.44.2", {"start": v(-8.7, -29.29) * mm, "mid": v(-8.54, -29.28) * mm, "end": v(-8.41, -29.16) * mm});
            skArc(sketch, "E7.44.3", {"start": v(-9.03, -29.2) * mm, "mid": v(-8.87, -29.24) * mm, "end": v(-8.7, -29.29) * mm});
            skArc(sketch, "E7.44.4", {"start": v(-9.2, -28.92) * mm, "mid": v(-9.17, -29.09) * mm, "end": v(-9.03, -29.2) * mm});
            skArc(sketch, "E7.44.5", {"start": v(-9.2, -28.92) * mm, "mid": v(-9.2, -28.8) * mm, "end": v(-9.2, -28.69) * mm});
            skArc(sketch, "E7.44.6", {"start": v(-9.2, -28.69) * mm, "mid": v(-9.33, -28.4) * mm, "end": v(-9.58, -28.23) * mm});
            skArc(sketch, "E7.45.0", {"start": v(-5.82, -29.23) * mm, "mid": v(-6.12, -29.26) * mm, "end": v(-6.37, -29.45) * mm});
            skArc(sketch, "E7.45.1", {"start": v(-6.37, -29.45) * mm, "mid": v(-6.43, -29.54) * mm, "end": v(-6.49, -29.65) * mm});
            skArc(sketch, "E7.45.2", {"start": v(-6.77, -29.8) * mm, "mid": v(-6.6, -29.77) * mm, "end": v(-6.49, -29.65) * mm});
            skArc(sketch, "E7.45.3", {"start": v(-7.1, -29.72) * mm, "mid": v(-6.94, -29.76) * mm, "end": v(-6.77, -29.8) * mm});
            skArc(sketch, "E7.45.4", {"start": v(-7.3, -29.46) * mm, "mid": v(-7.25, -29.62) * mm, "end": v(-7.1, -29.72) * mm});
            skArc(sketch, "E7.45.5", {"start": v(-7.3, -29.46) * mm, "mid": v(-7.3, -29.34) * mm, "end": v(-7.31, -29.23) * mm});
            skArc(sketch, "E7.45.6", {"start": v(-7.31, -29.23) * mm, "mid": v(-7.45, -28.95) * mm, "end": v(-7.71, -28.8) * mm});
            skArc(sketch, "E7.46.0", {"start": v(-3.9, -29.55) * mm, "mid": v(-4.2, -29.6) * mm, "end": v(-4.43, -29.8) * mm});
            skArc(sketch, "E7.46.1", {"start": v(-4.43, -29.8) * mm, "mid": v(-4.49, -29.9) * mm, "end": v(-4.53, -30) * mm});
            skArc(sketch, "E7.46.2", {"start": v(-4.81, -30.18) * mm, "mid": v(-4.64, -30.14) * mm, "end": v(-4.53, -30) * mm});
            skArc(sketch, "E7.46.3", {"start": v(-5.14, -30.12) * mm, "mid": v(-4.98, -30.15) * mm, "end": v(-4.81, -30.18) * mm});
            skArc(sketch, "E7.46.4", {"start": v(-5.35, -29.87) * mm, "mid": v(-5.3, -30.04) * mm, "end": v(-5.14, -30.12) * mm});
            skArc(sketch, "E7.46.5", {"start": v(-5.35, -29.87) * mm, "mid": v(-5.36, -29.76) * mm, "end": v(-5.39, -29.64) * mm});
            skArc(sketch, "E7.46.6", {"start": v(-5.39, -29.64) * mm, "mid": v(-5.54, -29.38) * mm, "end": v(-5.82, -29.23) * mm});
            skArc(sketch, "E7.47.0", {"start": v(-1.95, -29.74) * mm, "mid": v(-2.25, -29.8) * mm, "end": v(-2.47, -30.03) * mm});
            skArc(sketch, "E7.47.1", {"start": v(-2.47, -30.03) * mm, "mid": v(-2.52, -30.13) * mm, "end": v(-2.56, -30.24) * mm});
            skArc(sketch, "E7.47.2", {"start": v(-2.83, -30.43) * mm, "mid": v(-2.66, -30.38) * mm, "end": v(-2.56, -30.24) * mm});
            skArc(sketch, "E7.47.3", {"start": v(-3.16, -30.4) * mm, "mid": v(-3, -30.4) * mm, "end": v(-2.83, -30.43) * mm});
            skArc(sketch, "E7.47.4", {"start": v(-3.39, -30.16) * mm, "mid": v(-3.32, -30.32) * mm, "end": v(-3.16, -30.4) * mm});
            skArc(sketch, "E7.47.5", {"start": v(-3.39, -30.16) * mm, "mid": v(-3.4, -30.04) * mm, "end": v(-3.44, -29.93) * mm});
            skArc(sketch, "E7.47.6", {"start": v(-3.44, -29.93) * mm, "mid": v(-3.6, -29.68) * mm, "end": v(-3.9, -29.55) * mm});
            skArc(sketch, "E7.48.0", {"start": v(0, -29.8) * mm, "mid": v(-0.3, -29.9) * mm, "end": v(-0.5, -30.12) * mm});
            skArc(sketch, "E7.48.1", {"start": v(-0.5, -30.12) * mm, "mid": v(-0.55, -30.23) * mm, "end": v(-0.58, -30.34) * mm});
            skArc(sketch, "E7.48.2", {"start": v(-0.83, -30.54) * mm, "mid": v(-0.67, -30.5) * mm, "end": v(-0.58, -30.34) * mm});
            skArc(sketch, "E7.48.3", {"start": v(-1.17, -30.53) * mm, "mid": v(-1, -30.54) * mm, "end": v(-0.83, -30.54) * mm});
            skArc(sketch, "E7.48.4", {"start": v(-1.4, -30.32) * mm, "mid": v(-1.33, -30.47) * mm, "end": v(-1.17, -30.53) * mm});
            skArc(sketch, "E7.48.5", {"start": v(-1.4, -30.32) * mm, "mid": v(-1.43, -30.2) * mm, "end": v(-1.47, -30.1) * mm});
            skArc(sketch, "E7.48.6", {"start": v(-1.47, -30.1) * mm, "mid": v(-1.66, -29.85) * mm, "end": v(-1.95, -29.74) * mm});
            skArc(sketch, "E7.49.0", {"start": v(1.95, -29.74) * mm, "mid": v(1.66, -29.85) * mm, "end": v(1.47, -30.1) * mm});
            skArc(sketch, "E7.49.1", {"start": v(1.47, -30.1) * mm, "mid": v(1.43, -30.2) * mm, "end": v(1.4, -30.32) * mm});
            skArc(sketch, "E7.49.2", {"start": v(1.17, -30.53) * mm, "mid": v(1.33, -30.47) * mm, "end": v(1.4, -30.32) * mm});
            skArc(sketch, "E7.49.3", {"start": v(0.83, -30.54) * mm, "mid": v(1, -30.54) * mm, "end": v(1.17, -30.53) * mm});
            skArc(sketch, "E7.49.4", {"start": v(0.58, -30.34) * mm, "mid": v(0.67, -30.5) * mm, "end": v(0.83, -30.54) * mm});
            skArc(sketch, "E7.49.5", {"start": v(0.58, -30.34) * mm, "mid": v(0.55, -30.23) * mm, "end": v(0.5, -30.12) * mm});
            skArc(sketch, "E7.49.6", {"start": v(0.5, -30.12) * mm, "mid": v(0.3, -29.9) * mm, "end": v(0, -29.8) * mm});
            skArc(sketch, "E7.50.0", {"start": v(3.9, -29.55) * mm, "mid": v(3.6, -29.68) * mm, "end": v(3.44, -29.93) * mm});
            skArc(sketch, "E7.50.1", {"start": v(3.44, -29.93) * mm, "mid": v(3.4, -30.04) * mm, "end": v(3.39, -30.16) * mm});
            skArc(sketch, "E7.50.2", {"start": v(3.16, -30.4) * mm, "mid": v(3.32, -30.32) * mm, "end": v(3.39, -30.16) * mm});
            skArc(sketch, "E7.50.3", {"start": v(2.83, -30.43) * mm, "mid": v(3, -30.4) * mm, "end": v(3.16, -30.4) * mm});
            skArc(sketch, "E7.50.4", {"start": v(2.56, -30.24) * mm, "mid": v(2.66, -30.38) * mm, "end": v(2.83, -30.43) * mm});
            skArc(sketch, "E7.50.5", {"start": v(2.56, -30.24) * mm, "mid": v(2.52, -30.13) * mm, "end": v(2.47, -30.03) * mm});
            skArc(sketch, "E7.50.6", {"start": v(2.47, -30.03) * mm, "mid": v(2.25, -29.8) * mm, "end": v(1.95, -29.74) * mm});
            skArc(sketch, "E7.51.0", {"start": v(5.82, -29.23) * mm, "mid": v(5.54, -29.38) * mm, "end": v(5.39, -29.64) * mm});
            skArc(sketch, "E7.51.1", {"start": v(5.39, -29.64) * mm, "mid": v(5.36, -29.76) * mm, "end": v(5.35, -29.87) * mm});
            skArc(sketch, "E7.51.2", {"start": v(5.14, -30.12) * mm, "mid": v(5.3, -30.04) * mm, "end": v(5.35, -29.87) * mm});
            skArc(sketch, "E7.51.3", {"start": v(4.81, -30.18) * mm, "mid": v(4.98, -30.15) * mm, "end": v(5.14, -30.12) * mm});
            skArc(sketch, "E7.51.4", {"start": v(4.53, -30) * mm, "mid": v(4.64, -30.14) * mm, "end": v(4.81, -30.18) * mm});
            skArc(sketch, "E7.51.5", {"start": v(4.53, -30) * mm, "mid": v(4.49, -29.9) * mm, "end": v(4.43, -29.8) * mm});
            skArc(sketch, "E7.51.6", {"start": v(4.43, -29.8) * mm, "mid": v(4.2, -29.6) * mm, "end": v(3.9, -29.55) * mm});
            skArc(sketch, "E7.52.0", {"start": v(7.71, -28.8) * mm, "mid": v(7.45, -28.95) * mm, "end": v(7.31, -29.23) * mm});
            skArc(sketch, "E7.52.1", {"start": v(7.31, -29.23) * mm, "mid": v(7.3, -29.34) * mm, "end": v(7.3, -29.46) * mm});
            skArc(sketch, "E7.52.2", {"start": v(7.1, -29.72) * mm, "mid": v(7.25, -29.62) * mm, "end": v(7.3, -29.46) * mm});
            skArc(sketch, "E7.52.3", {"start": v(6.77, -29.8) * mm, "mid": v(6.94, -29.76) * mm, "end": v(7.1, -29.72) * mm});
            skArc(sketch, "E7.52.4", {"start": v(6.49, -29.65) * mm, "mid": v(6.6, -29.77) * mm, "end": v(6.77, -29.8) * mm});
            skArc(sketch, "E7.52.5", {"start": v(6.49, -29.65) * mm, "mid": v(6.43, -29.54) * mm, "end": v(6.37, -29.45) * mm});
            skArc(sketch, "E7.52.6", {"start": v(6.37, -29.45) * mm, "mid": v(6.12, -29.26) * mm, "end": v(5.82, -29.23) * mm});
            skArc(sketch, "E7.53.0", {"start": v(9.58, -28.23) * mm, "mid": v(9.33, -28.4) * mm, "end": v(9.2, -28.69) * mm});
            skArc(sketch, "E7.53.1", {"start": v(9.2, -28.69) * mm, "mid": v(9.2, -28.8) * mm, "end": v(9.2, -28.92) * mm});
            skArc(sketch, "E7.53.2", {"start": v(9.03, -29.2) * mm, "mid": v(9.17, -29.09) * mm, "end": v(9.2, -28.92) * mm});
            skArc(sketch, "E7.53.3", {"start": v(8.7, -29.29) * mm, "mid": v(8.87, -29.24) * mm, "end": v(9.03, -29.2) * mm});
            skArc(sketch, "E7.53.4", {"start": v(8.41, -29.16) * mm, "mid": v(8.54, -29.28) * mm, "end": v(8.7, -29.29) * mm});
            skArc(sketch, "E7.53.5", {"start": v(8.41, -29.16) * mm, "mid": v(8.35, -29.06) * mm, "end": v(8.28, -28.97) * mm});
            skArc(sketch, "E7.53.6", {"start": v(8.28, -28.97) * mm, "mid": v(8.02, -28.8) * mm, "end": v(7.71, -28.8) * mm});
            skArc(sketch, "E7.54.0", {"start": v(11.4, -27.54) * mm, "mid": v(11.17, -27.73) * mm, "end": v(11.06, -28.02) * mm});
            skArc(sketch, "E7.54.1", {"start": v(11.06, -28.02) * mm, "mid": v(11.07, -28.14) * mm, "end": v(11.08, -28.25) * mm});
            skArc(sketch, "E7.54.2", {"start": v(10.92, -28.54) * mm, "mid": v(11.05, -28.43) * mm, "end": v(11.08, -28.25) * mm});
            skArc(sketch, "E7.54.3", {"start": v(10.6, -28.66) * mm, "mid": v(10.76, -28.6) * mm, "end": v(10.92, -28.54) * mm});
            skArc(sketch, "E7.54.4", {"start": v(10.3, -28.55) * mm, "mid": v(10.43, -28.66) * mm, "end": v(10.6, -28.66) * mm});
            skArc(sketch, "E7.54.5", {"start": v(10.3, -28.55) * mm, "mid": v(10.23, -28.45) * mm, "end": v(10.16, -28.36) * mm});
            skArc(sketch, "E7.54.6", {"start": v(10.16, -28.36) * mm, "mid": v(9.89, -28.21) * mm, "end": v(9.58, -28.23) * mm});
            skArc(sketch, "E7.55.0", {"start": v(13.18, -26.73) * mm, "mid": v(12.96, -26.94) * mm, "end": v(12.87, -27.24) * mm});
            skArc(sketch, "E7.55.1", {"start": v(12.87, -27.24) * mm, "mid": v(12.88, -27.35) * mm, "end": v(12.9, -27.47) * mm});
            skArc(sketch, "E7.55.2", {"start": v(12.76, -27.76) * mm, "mid": v(12.89, -27.64) * mm, "end": v(12.9, -27.47) * mm});
            skArc(sketch, "E7.55.3", {"start": v(12.46, -27.9) * mm, "mid": v(12.61, -27.83) * mm, "end": v(12.76, -27.76) * mm});
            skArc(sketch, "E7.55.4", {"start": v(12.14, -27.81) * mm, "mid": v(12.29, -27.91) * mm, "end": v(12.46, -27.9) * mm});
            skArc(sketch, "E7.55.5", {"start": v(12.14, -27.81) * mm, "mid": v(12.07, -27.72) * mm, "end": v(12, -27.64) * mm});
            skArc(sketch, "E7.55.6", {"start": v(12, -27.64) * mm, "mid": v(11.71, -27.5) * mm, "end": v(11.4, -27.54) * mm});
            skArc(sketch, "E7.56.0", {"start": v(14.9, -25.81) * mm, "mid": v(14.69, -26.04) * mm, "end": v(14.63, -26.34) * mm});
            skArc(sketch, "E7.56.1", {"start": v(14.63, -26.34) * mm, "mid": v(14.64, -26.45) * mm, "end": v(14.67, -26.57) * mm});
            skArc(sketch, "E7.56.2", {"start": v(14.55, -26.87) * mm, "mid": v(14.67, -26.74) * mm, "end": v(14.67, -26.57) * mm});
            skArc(sketch, "E7.56.3", {"start": v(14.26, -27.03) * mm, "mid": v(14.4, -26.95) * mm, "end": v(14.55, -26.87) * mm});
            skArc(sketch, "E7.56.4", {"start": v(13.94, -26.96) * mm, "mid": v(14.08, -27.05) * mm, "end": v(14.26, -27.03) * mm});
            skArc(sketch, "E7.56.5", {"start": v(13.94, -26.96) * mm, "mid": v(13.86, -26.87) * mm, "end": v(13.77, -26.8) * mm});
            skArc(sketch, "E7.56.6", {"start": v(13.77, -26.8) * mm, "mid": v(13.49, -26.68) * mm, "end": v(13.18, -26.73) * mm});
            skArc(sketch, "E7.57.0", {"start": v(16.56, -24.78) * mm, "mid": v(16.36, -25.02) * mm, "end": v(16.32, -25.32) * mm});
            skArc(sketch, "E7.57.1", {"start": v(16.32, -25.32) * mm, "mid": v(16.34, -25.44) * mm, "end": v(16.38, -25.55) * mm});
            skArc(sketch, "E7.57.2", {"start": v(16.28, -25.86) * mm, "mid": v(16.38, -25.72) * mm, "end": v(16.38, -25.55) * mm});
            skArc(sketch, "E7.57.3", {"start": v(16, -26.04) * mm, "mid": v(16.14, -25.95) * mm, "end": v(16.28, -25.86) * mm});
            skArc(sketch, "E7.57.4", {"start": v(15.67, -26) * mm, "mid": v(15.82, -26.07) * mm, "end": v(16, -26.04) * mm});
            skArc(sketch, "E7.57.5", {"start": v(15.67, -26) * mm, "mid": v(15.59, -25.9) * mm, "end": v(15.5, -25.84) * mm});
            skArc(sketch, "E7.57.6", {"start": v(15.5, -25.84) * mm, "mid": v(15.2, -25.74) * mm, "end": v(14.9, -25.81) * mm});
            skArc(sketch, "E7.58.0", {"start": v(18.15, -23.65) * mm, "mid": v(17.96, -23.9) * mm, "end": v(17.94, -24.2) * mm});
            skArc(sketch, "E7.58.1", {"start": v(17.94, -24.2) * mm, "mid": v(17.97, -24.32) * mm, "end": v(18.02, -24.42) * mm});
            skArc(sketch, "E7.58.2", {"start": v(17.93, -24.74) * mm, "mid": v(18.03, -24.6) * mm, "end": v(18.02, -24.42) * mm});
            skArc(sketch, "E7.58.3", {"start": v(17.66, -24.94) * mm, "mid": v(17.8, -24.84) * mm, "end": v(17.93, -24.74) * mm});
            skArc(sketch, "E7.58.4", {"start": v(17.34, -24.91) * mm, "mid": v(17.5, -24.98) * mm, "end": v(17.66, -24.94) * mm});
            skArc(sketch, "E7.58.5", {"start": v(17.34, -24.91) * mm, "mid": v(17.25, -24.83) * mm, "end": v(17.15, -24.77) * mm});
            skArc(sketch, "E7.58.6", {"start": v(17.15, -24.77) * mm, "mid": v(16.85, -24.7) * mm, "end": v(16.56, -24.78) * mm});
            skArc(sketch, "E7.59.0", {"start": v(19.65, -22.41) * mm, "mid": v(19.49, -22.67) * mm, "end": v(19.48, -22.98) * mm});
            skArc(sketch, "E7.59.1", {"start": v(19.48, -22.98) * mm, "mid": v(19.52, -23.09) * mm, "end": v(19.57, -23.2) * mm});
            skArc(sketch, "E7.59.2", {"start": v(19.51, -23.51) * mm, "mid": v(19.6, -23.36) * mm, "end": v(19.57, -23.2) * mm});
            skArc(sketch, "E7.59.3", {"start": v(19.25, -23.73) * mm, "mid": v(19.38, -23.62) * mm, "end": v(19.51, -23.51) * mm});
            skArc(sketch, "E7.59.4", {"start": v(18.93, -23.72) * mm, "mid": v(19.1, -23.78) * mm, "end": v(19.25, -23.73) * mm});
            skArc(sketch, "E7.59.5", {"start": v(18.93, -23.72) * mm, "mid": v(18.84, -23.65) * mm, "end": v(18.74, -23.6) * mm});
            skArc(sketch, "E7.59.6", {"start": v(18.74, -23.6) * mm, "mid": v(18.43, -23.54) * mm, "end": v(18.15, -23.65) * mm});
            skArc(sketch, "E7.60.0", {"start": v(21.08, -21.08) * mm, "mid": v(20.93, -21.35) * mm, "end": v(20.95, -21.65) * mm});
            skArc(sketch, "E7.60.1", {"start": v(20.95, -21.65) * mm, "mid": v(21, -21.76) * mm, "end": v(21.05, -21.86) * mm});
            skArc(sketch, "E7.60.2", {"start": v(21.01, -22.19) * mm, "mid": v(21.09, -22.03) * mm, "end": v(21.05, -21.86) * mm});
            skArc(sketch, "E7.60.3", {"start": v(20.76, -22.42) * mm, "mid": v(20.89, -22.3) * mm, "end": v(21.01, -22.19) * mm});
            skArc(sketch, "E7.60.4", {"start": v(20.44, -22.43) * mm, "mid": v(20.6, -22.48) * mm, "end": v(20.76, -22.42) * mm});
            skArc(sketch, "E7.60.5", {"start": v(20.44, -22.43) * mm, "mid": v(20.34, -22.37) * mm, "end": v(20.24, -22.32) * mm});
            skArc(sketch, "E7.60.6", {"start": v(20.24, -22.32) * mm, "mid": v(19.93, -22.28) * mm, "end": v(19.65, -22.41) * mm});
            skArc(sketch, "E7.61.0", {"start": v(22.41, -19.65) * mm, "mid": v(22.28, -19.93) * mm, "end": v(22.32, -20.24) * mm});
            skArc(sketch, "E7.61.1", {"start": v(22.32, -20.24) * mm, "mid": v(22.37, -20.34) * mm, "end": v(22.43, -20.44) * mm});
            skArc(sketch, "E7.61.2", {"start": v(22.42, -20.76) * mm, "mid": v(22.48, -20.6) * mm, "end": v(22.43, -20.44) * mm});
            skArc(sketch, "E7.61.3", {"start": v(22.19, -21.01) * mm, "mid": v(22.3, -20.89) * mm, "end": v(22.42, -20.76) * mm});
            skArc(sketch, "E7.61.4", {"start": v(21.86, -21.05) * mm, "mid": v(22.03, -21.09) * mm, "end": v(22.19, -21.01) * mm});
            skArc(sketch, "E7.61.5", {"start": v(21.86, -21.05) * mm, "mid": v(21.76, -21) * mm, "end": v(21.65, -20.95) * mm});
            skArc(sketch, "E7.61.6", {"start": v(21.65, -20.95) * mm, "mid": v(21.35, -20.93) * mm, "end": v(21.08, -21.08) * mm});
            skArc(sketch, "E7.62.0", {"start": v(23.65, -18.15) * mm, "mid": v(23.54, -18.43) * mm, "end": v(23.6, -18.74) * mm});
            skArc(sketch, "E7.62.1", {"start": v(23.6, -18.74) * mm, "mid": v(23.65, -18.84) * mm, "end": v(23.72, -18.93) * mm});
            skArc(sketch, "E7.62.2", {"start": v(23.73, -19.25) * mm, "mid": v(23.78, -19.1) * mm, "end": v(23.72, -18.93) * mm});
            skArc(sketch, "E7.62.3", {"start": v(23.51, -19.51) * mm, "mid": v(23.62, -19.38) * mm, "end": v(23.73, -19.25) * mm});
            skArc(sketch, "E7.62.4", {"start": v(23.2, -19.57) * mm, "mid": v(23.36, -19.6) * mm, "end": v(23.51, -19.51) * mm});
            skArc(sketch, "E7.62.5", {"start": v(23.2, -19.57) * mm, "mid": v(23.09, -19.52) * mm, "end": v(22.98, -19.48) * mm});
            skArc(sketch, "E7.62.6", {"start": v(22.98, -19.48) * mm, "mid": v(22.67, -19.49) * mm, "end": v(22.41, -19.65) * mm});
            skArc(sketch, "E7.63.0", {"start": v(24.78, -16.56) * mm, "mid": v(24.7, -16.85) * mm, "end": v(24.77, -17.15) * mm});
            skArc(sketch, "E7.63.1", {"start": v(24.77, -17.15) * mm, "mid": v(24.83, -17.25) * mm, "end": v(24.91, -17.34) * mm});
            skArc(sketch, "E7.63.2", {"start": v(24.94, -17.66) * mm, "mid": v(24.98, -17.5) * mm, "end": v(24.91, -17.34) * mm});
            skArc(sketch, "E7.63.3", {"start": v(24.74, -17.93) * mm, "mid": v(24.84, -17.8) * mm, "end": v(24.94, -17.66) * mm});
            skArc(sketch, "E7.63.4", {"start": v(24.42, -18.02) * mm, "mid": v(24.6, -18.03) * mm, "end": v(24.74, -17.93) * mm});
            skArc(sketch, "E7.63.5", {"start": v(24.42, -18.02) * mm, "mid": v(24.32, -17.97) * mm, "end": v(24.2, -17.94) * mm});
            skArc(sketch, "E7.63.6", {"start": v(24.2, -17.94) * mm, "mid": v(23.9, -17.96) * mm, "end": v(23.65, -18.15) * mm});
            skArc(sketch, "E7.64.0", {"start": v(25.81, -14.9) * mm, "mid": v(25.74, -15.2) * mm, "end": v(25.84, -15.5) * mm});
            skArc(sketch, "E7.64.1", {"start": v(25.84, -15.5) * mm, "mid": v(25.9, -15.59) * mm, "end": v(26, -15.67) * mm});
            skArc(sketch, "E7.64.2", {"start": v(26.04, -16) * mm, "mid": v(26.07, -15.82) * mm, "end": v(26, -15.67) * mm});
            skArc(sketch, "E7.64.3", {"start": v(25.86, -16.28) * mm, "mid": v(25.95, -16.14) * mm, "end": v(26.04, -16) * mm});
            skArc(sketch, "E7.64.4", {"start": v(25.55, -16.38) * mm, "mid": v(25.72, -16.38) * mm, "end": v(25.86, -16.28) * mm});
            skArc(sketch, "E7.64.5", {"start": v(25.55, -16.38) * mm, "mid": v(25.44, -16.34) * mm, "end": v(25.32, -16.32) * mm});
            skArc(sketch, "E7.64.6", {"start": v(25.32, -16.32) * mm, "mid": v(25.02, -16.36) * mm, "end": v(24.78, -16.56) * mm});
            skArc(sketch, "E7.65.0", {"start": v(26.73, -13.18) * mm, "mid": v(26.68, -13.49) * mm, "end": v(26.8, -13.77) * mm});
            skArc(sketch, "E7.65.1", {"start": v(26.8, -13.77) * mm, "mid": v(26.87, -13.86) * mm, "end": v(26.96, -13.94) * mm});
            skArc(sketch, "E7.65.2", {"start": v(27.03, -14.26) * mm, "mid": v(27.05, -14.08) * mm, "end": v(26.96, -13.94) * mm});
            skArc(sketch, "E7.65.3", {"start": v(26.87, -14.55) * mm, "mid": v(26.95, -14.4) * mm, "end": v(27.03, -14.26) * mm});
            skArc(sketch, "E7.65.4", {"start": v(26.57, -14.67) * mm, "mid": v(26.74, -14.67) * mm, "end": v(26.87, -14.55) * mm});
            skArc(sketch, "E7.65.5", {"start": v(26.57, -14.67) * mm, "mid": v(26.45, -14.64) * mm, "end": v(26.34, -14.63) * mm});
            skArc(sketch, "E7.65.6", {"start": v(26.34, -14.63) * mm, "mid": v(26.04, -14.69) * mm, "end": v(25.81, -14.9) * mm});
            skArc(sketch, "E7.66.0", {"start": v(27.54, -11.4) * mm, "mid": v(27.5, -11.71) * mm, "end": v(27.64, -12) * mm});
            skArc(sketch, "E7.66.1", {"start": v(27.64, -12) * mm, "mid": v(27.72, -12.07) * mm, "end": v(27.81, -12.14) * mm});
            skArc(sketch, "E7.66.2", {"start": v(27.9, -12.46) * mm, "mid": v(27.91, -12.29) * mm, "end": v(27.81, -12.14) * mm});
            skArc(sketch, "E7.66.3", {"start": v(27.76, -12.76) * mm, "mid": v(27.83, -12.61) * mm, "end": v(27.9, -12.46) * mm});
            skArc(sketch, "E7.66.4", {"start": v(27.47, -12.9) * mm, "mid": v(27.64, -12.89) * mm, "end": v(27.76, -12.76) * mm});
            skArc(sketch, "E7.66.5", {"start": v(27.47, -12.9) * mm, "mid": v(27.35, -12.88) * mm, "end": v(27.24, -12.87) * mm});
            skArc(sketch, "E7.66.6", {"start": v(27.24, -12.87) * mm, "mid": v(26.94, -12.96) * mm, "end": v(26.73, -13.18) * mm});
            skArc(sketch, "E7.67.0", {"start": v(28.23, -9.58) * mm, "mid": v(28.21, -9.89) * mm, "end": v(28.36, -10.16) * mm});
            skArc(sketch, "E7.67.1", {"start": v(28.36, -10.16) * mm, "mid": v(28.45, -10.23) * mm, "end": v(28.55, -10.3) * mm});
            skArc(sketch, "E7.67.2", {"start": v(28.66, -10.6) * mm, "mid": v(28.66, -10.43) * mm, "end": v(28.55, -10.3) * mm});
            skArc(sketch, "E7.67.3", {"start": v(28.54, -10.92) * mm, "mid": v(28.6, -10.76) * mm, "end": v(28.66, -10.6) * mm});
            skArc(sketch, "E7.67.4", {"start": v(28.25, -11.08) * mm, "mid": v(28.43, -11.05) * mm, "end": v(28.54, -10.92) * mm});
            skArc(sketch, "E7.67.5", {"start": v(28.25, -11.08) * mm, "mid": v(28.14, -11.07) * mm, "end": v(28.02, -11.06) * mm});
            skArc(sketch, "E7.67.6", {"start": v(28.02, -11.06) * mm, "mid": v(27.73, -11.17) * mm, "end": v(27.54, -11.4) * mm});
            skArc(sketch, "E7.68.0", {"start": v(28.8, -7.71) * mm, "mid": v(28.8, -8.02) * mm, "end": v(28.97, -8.28) * mm});
            skArc(sketch, "E7.68.1", {"start": v(28.97, -8.28) * mm, "mid": v(29.06, -8.35) * mm, "end": v(29.16, -8.41) * mm});
            skArc(sketch, "E7.68.2", {"start": v(29.29, -8.7) * mm, "mid": v(29.28, -8.54) * mm, "end": v(29.16, -8.41) * mm});
            skArc(sketch, "E7.68.3", {"start": v(29.2, -9.03) * mm, "mid": v(29.24, -8.87) * mm, "end": v(29.29, -8.7) * mm});
            skArc(sketch, "E7.68.4", {"start": v(28.92, -9.2) * mm, "mid": v(29.09, -9.17) * mm, "end": v(29.2, -9.03) * mm});
            skArc(sketch, "E7.68.5", {"start": v(28.92, -9.2) * mm, "mid": v(28.8, -9.2) * mm, "end": v(28.69, -9.2) * mm});
            skArc(sketch, "E7.68.6", {"start": v(28.69, -9.2) * mm, "mid": v(28.4, -9.33) * mm, "end": v(28.23, -9.58) * mm});
            skArc(sketch, "E7.69.0", {"start": v(29.23, -5.82) * mm, "mid": v(29.26, -6.12) * mm, "end": v(29.45, -6.37) * mm});
            skArc(sketch, "E7.69.1", {"start": v(29.45, -6.37) * mm, "mid": v(29.54, -6.43) * mm, "end": v(29.65, -6.49) * mm});
            skArc(sketch, "E7.69.2", {"start": v(29.8, -6.77) * mm, "mid": v(29.77, -6.6) * mm, "end": v(29.65, -6.49) * mm});
            skArc(sketch, "E7.69.3", {"start": v(29.72, -7.1) * mm, "mid": v(29.76, -6.94) * mm, "end": v(29.8, -6.77) * mm});
            skArc(sketch, "E7.69.4", {"start": v(29.46, -7.3) * mm, "mid": v(29.62, -7.25) * mm, "end": v(29.72, -7.1) * mm});
            skArc(sketch, "E7.69.5", {"start": v(29.46, -7.3) * mm, "mid": v(29.34, -7.3) * mm, "end": v(29.23, -7.31) * mm});
            skArc(sketch, "E7.69.6", {"start": v(29.23, -7.31) * mm, "mid": v(28.95, -7.45) * mm, "end": v(28.8, -7.71) * mm});
            skArc(sketch, "E7.70.0", {"start": v(29.55, -3.9) * mm, "mid": v(29.6, -4.2) * mm, "end": v(29.8, -4.43) * mm});
            skArc(sketch, "E7.70.1", {"start": v(29.8, -4.43) * mm, "mid": v(29.9, -4.49) * mm, "end": v(30, -4.53) * mm});
            skArc(sketch, "E7.70.2", {"start": v(30.18, -4.81) * mm, "mid": v(30.14, -4.64) * mm, "end": v(30, -4.53) * mm});
            skArc(sketch, "E7.70.3", {"start": v(30.12, -5.14) * mm, "mid": v(30.15, -4.98) * mm, "end": v(30.18, -4.81) * mm});
            skArc(sketch, "E7.70.4", {"start": v(29.87, -5.35) * mm, "mid": v(30.04, -5.3) * mm, "end": v(30.12, -5.14) * mm});
            skArc(sketch, "E7.70.5", {"start": v(29.87, -5.35) * mm, "mid": v(29.76, -5.36) * mm, "end": v(29.64, -5.39) * mm});
            skArc(sketch, "E7.70.6", {"start": v(29.64, -5.39) * mm, "mid": v(29.38, -5.54) * mm, "end": v(29.23, -5.82) * mm});
            skArc(sketch, "E7.71.0", {"start": v(29.74, -1.95) * mm, "mid": v(29.8, -2.25) * mm, "end": v(30.03, -2.47) * mm});
            skArc(sketch, "E7.71.1", {"start": v(30.03, -2.47) * mm, "mid": v(30.13, -2.52) * mm, "end": v(30.24, -2.56) * mm});
            skArc(sketch, "E7.71.2", {"start": v(30.43, -2.83) * mm, "mid": v(30.38, -2.66) * mm, "end": v(30.24, -2.56) * mm});
            skArc(sketch, "E7.71.3", {"start": v(30.4, -3.16) * mm, "mid": v(30.4, -3) * mm, "end": v(30.43, -2.83) * mm});
            skArc(sketch, "E7.71.4", {"start": v(30.16, -3.39) * mm, "mid": v(30.32, -3.32) * mm, "end": v(30.4, -3.16) * mm});
            skArc(sketch, "E7.71.5", {"start": v(30.16, -3.39) * mm, "mid": v(30.04, -3.4) * mm, "end": v(29.93, -3.44) * mm});
            skArc(sketch, "E7.71.6", {"start": v(29.93, -3.44) * mm, "mid": v(29.68, -3.6) * mm, "end": v(29.55, -3.9) * mm});
            skArc(sketch, "E7.72.0", {"start": v(29.8, 0) * mm, "mid": v(29.9, -0.3) * mm, "end": v(30.12, -0.5) * mm});
            skArc(sketch, "E7.72.1", {"start": v(30.12, -0.5) * mm, "mid": v(30.23, -0.55) * mm, "end": v(30.34, -0.58) * mm});
            skArc(sketch, "E7.72.2", {"start": v(30.54, -0.83) * mm, "mid": v(30.5, -0.67) * mm, "end": v(30.34, -0.58) * mm});
            skArc(sketch, "E7.72.3", {"start": v(30.53, -1.17) * mm, "mid": v(30.54, -1) * mm, "end": v(30.54, -0.83) * mm});
            skArc(sketch, "E7.72.4", {"start": v(30.32, -1.4) * mm, "mid": v(30.47, -1.33) * mm, "end": v(30.53, -1.17) * mm});
            skArc(sketch, "E7.72.5", {"start": v(30.32, -1.4) * mm, "mid": v(30.2, -1.43) * mm, "end": v(30.1, -1.47) * mm});
            skArc(sketch, "E7.72.6", {"start": v(30.1, -1.47) * mm, "mid": v(29.85, -1.66) * mm, "end": v(29.74, -1.95) * mm});
            skArc(sketch, "E7.73.0", {"start": v(29.74, 1.95) * mm, "mid": v(29.85, 1.66) * mm, "end": v(30.1, 1.47) * mm});
            skArc(sketch, "E7.73.1", {"start": v(30.1, 1.47) * mm, "mid": v(30.2, 1.43) * mm, "end": v(30.32, 1.4) * mm});
            skArc(sketch, "E7.73.2", {"start": v(30.53, 1.17) * mm, "mid": v(30.47, 1.33) * mm, "end": v(30.32, 1.4) * mm});
            skArc(sketch, "E7.73.3", {"start": v(30.54, 0.83) * mm, "mid": v(30.54, 1) * mm, "end": v(30.53, 1.17) * mm});
            skArc(sketch, "E7.73.4", {"start": v(30.34, 0.58) * mm, "mid": v(30.5, 0.67) * mm, "end": v(30.54, 0.83) * mm});
            skArc(sketch, "E7.73.5", {"start": v(30.34, 0.58) * mm, "mid": v(30.23, 0.55) * mm, "end": v(30.12, 0.5) * mm});
            skArc(sketch, "E7.73.6", {"start": v(30.12, 0.5) * mm, "mid": v(29.9, 0.3) * mm, "end": v(29.8, 0) * mm});
            skArc(sketch, "E7.74.0", {"start": v(29.55, 3.9) * mm, "mid": v(29.68, 3.6) * mm, "end": v(29.93, 3.44) * mm});
            skArc(sketch, "E7.74.1", {"start": v(29.93, 3.44) * mm, "mid": v(30.04, 3.4) * mm, "end": v(30.16, 3.39) * mm});
            skArc(sketch, "E7.74.2", {"start": v(30.4, 3.16) * mm, "mid": v(30.32, 3.32) * mm, "end": v(30.16, 3.39) * mm});
            skArc(sketch, "E7.74.3", {"start": v(30.43, 2.83) * mm, "mid": v(30.4, 3) * mm, "end": v(30.4, 3.16) * mm});
            skArc(sketch, "E7.74.4", {"start": v(30.24, 2.56) * mm, "mid": v(30.38, 2.66) * mm, "end": v(30.43, 2.83) * mm});
            skArc(sketch, "E7.74.5", {"start": v(30.24, 2.56) * mm, "mid": v(30.13, 2.52) * mm, "end": v(30.03, 2.47) * mm});
            skArc(sketch, "E7.74.6", {"start": v(30.03, 2.47) * mm, "mid": v(29.8, 2.25) * mm, "end": v(29.74, 1.95) * mm});
            skArc(sketch, "E7.75.0", {"start": v(29.23, 5.82) * mm, "mid": v(29.38, 5.54) * mm, "end": v(29.64, 5.39) * mm});
            skArc(sketch, "E7.75.1", {"start": v(29.64, 5.39) * mm, "mid": v(29.76, 5.36) * mm, "end": v(29.87, 5.35) * mm});
            skArc(sketch, "E7.75.2", {"start": v(30.12, 5.14) * mm, "mid": v(30.04, 5.3) * mm, "end": v(29.87, 5.35) * mm});
            skArc(sketch, "E7.75.3", {"start": v(30.18, 4.81) * mm, "mid": v(30.15, 4.98) * mm, "end": v(30.12, 5.14) * mm});
            skArc(sketch, "E7.75.4", {"start": v(30, 4.53) * mm, "mid": v(30.14, 4.64) * mm, "end": v(30.18, 4.81) * mm});
            skArc(sketch, "E7.75.5", {"start": v(30, 4.53) * mm, "mid": v(29.9, 4.49) * mm, "end": v(29.8, 4.43) * mm});
            skArc(sketch, "E7.75.6", {"start": v(29.8, 4.43) * mm, "mid": v(29.6, 4.2) * mm, "end": v(29.55, 3.9) * mm});
            skArc(sketch, "E7.76.0", {"start": v(28.8, 7.71) * mm, "mid": v(28.95, 7.45) * mm, "end": v(29.23, 7.31) * mm});
            skArc(sketch, "E7.76.1", {"start": v(29.23, 7.31) * mm, "mid": v(29.34, 7.3) * mm, "end": v(29.46, 7.3) * mm});
            skArc(sketch, "E7.76.2", {"start": v(29.72, 7.1) * mm, "mid": v(29.62, 7.25) * mm, "end": v(29.46, 7.3) * mm});
            skArc(sketch, "E7.76.3", {"start": v(29.8, 6.77) * mm, "mid": v(29.76, 6.94) * mm, "end": v(29.72, 7.1) * mm});
            skArc(sketch, "E7.76.4", {"start": v(29.65, 6.49) * mm, "mid": v(29.77, 6.6) * mm, "end": v(29.8, 6.77) * mm});
            skArc(sketch, "E7.76.5", {"start": v(29.65, 6.49) * mm, "mid": v(29.54, 6.43) * mm, "end": v(29.45, 6.37) * mm});
            skArc(sketch, "E7.76.6", {"start": v(29.45, 6.37) * mm, "mid": v(29.26, 6.12) * mm, "end": v(29.23, 5.82) * mm});
            skArc(sketch, "E7.77.0", {"start": v(28.23, 9.58) * mm, "mid": v(28.4, 9.33) * mm, "end": v(28.69, 9.2) * mm});
            skArc(sketch, "E7.77.1", {"start": v(28.69, 9.2) * mm, "mid": v(28.8, 9.2) * mm, "end": v(28.92, 9.2) * mm});
            skArc(sketch, "E7.77.2", {"start": v(29.2, 9.03) * mm, "mid": v(29.09, 9.17) * mm, "end": v(28.92, 9.2) * mm});
            skArc(sketch, "E7.77.3", {"start": v(29.29, 8.7) * mm, "mid": v(29.24, 8.87) * mm, "end": v(29.2, 9.03) * mm});
            skArc(sketch, "E7.77.4", {"start": v(29.16, 8.41) * mm, "mid": v(29.28, 8.54) * mm, "end": v(29.29, 8.7) * mm});
            skArc(sketch, "E7.77.5", {"start": v(29.16, 8.41) * mm, "mid": v(29.06, 8.35) * mm, "end": v(28.97, 8.28) * mm});
            skArc(sketch, "E7.77.6", {"start": v(28.97, 8.28) * mm, "mid": v(28.8, 8.02) * mm, "end": v(28.8, 7.71) * mm});
            skArc(sketch, "E7.78.0", {"start": v(27.54, 11.4) * mm, "mid": v(27.73, 11.17) * mm, "end": v(28.02, 11.06) * mm});
            skArc(sketch, "E7.78.1", {"start": v(28.02, 11.06) * mm, "mid": v(28.14, 11.07) * mm, "end": v(28.25, 11.08) * mm});
            skArc(sketch, "E7.78.2", {"start": v(28.54, 10.92) * mm, "mid": v(28.43, 11.05) * mm, "end": v(28.25, 11.08) * mm});
            skArc(sketch, "E7.78.3", {"start": v(28.66, 10.6) * mm, "mid": v(28.6, 10.76) * mm, "end": v(28.54, 10.92) * mm});
            skArc(sketch, "E7.78.4", {"start": v(28.55, 10.3) * mm, "mid": v(28.66, 10.43) * mm, "end": v(28.66, 10.6) * mm});
            skArc(sketch, "E7.78.5", {"start": v(28.55, 10.3) * mm, "mid": v(28.45, 10.23) * mm, "end": v(28.36, 10.16) * mm});
            skArc(sketch, "E7.78.6", {"start": v(28.36, 10.16) * mm, "mid": v(28.21, 9.89) * mm, "end": v(28.23, 9.58) * mm});
            skArc(sketch, "E7.79.0", {"start": v(26.73, 13.18) * mm, "mid": v(26.94, 12.96) * mm, "end": v(27.24, 12.87) * mm});
            skArc(sketch, "E7.79.1", {"start": v(27.24, 12.87) * mm, "mid": v(27.35, 12.88) * mm, "end": v(27.47, 12.9) * mm});
            skArc(sketch, "E7.79.2", {"start": v(27.76, 12.76) * mm, "mid": v(27.64, 12.89) * mm, "end": v(27.47, 12.9) * mm});
            skArc(sketch, "E7.79.3", {"start": v(27.9, 12.46) * mm, "mid": v(27.83, 12.61) * mm, "end": v(27.76, 12.76) * mm});
            skArc(sketch, "E7.79.4", {"start": v(27.81, 12.14) * mm, "mid": v(27.91, 12.29) * mm, "end": v(27.9, 12.46) * mm});
            skArc(sketch, "E7.79.5", {"start": v(27.81, 12.14) * mm, "mid": v(27.72, 12.07) * mm, "end": v(27.64, 12) * mm});
            skArc(sketch, "E7.79.6", {"start": v(27.64, 12) * mm, "mid": v(27.5, 11.71) * mm, "end": v(27.54, 11.4) * mm});
            skArc(sketch, "E7.80.0", {"start": v(25.81, 14.9) * mm, "mid": v(26.04, 14.69) * mm, "end": v(26.34, 14.63) * mm});
            skArc(sketch, "E7.80.1", {"start": v(26.34, 14.63) * mm, "mid": v(26.45, 14.64) * mm, "end": v(26.57, 14.67) * mm});
            skArc(sketch, "E7.80.2", {"start": v(26.87, 14.55) * mm, "mid": v(26.74, 14.67) * mm, "end": v(26.57, 14.67) * mm});
            skArc(sketch, "E7.80.3", {"start": v(27.03, 14.26) * mm, "mid": v(26.95, 14.4) * mm, "end": v(26.87, 14.55) * mm});
            skArc(sketch, "E7.80.4", {"start": v(26.96, 13.94) * mm, "mid": v(27.05, 14.08) * mm, "end": v(27.03, 14.26) * mm});
            skArc(sketch, "E7.80.5", {"start": v(26.96, 13.94) * mm, "mid": v(26.87, 13.86) * mm, "end": v(26.8, 13.77) * mm});
            skArc(sketch, "E7.80.6", {"start": v(26.8, 13.77) * mm, "mid": v(26.68, 13.49) * mm, "end": v(26.73, 13.18) * mm});
            skArc(sketch, "E7.81.0", {"start": v(24.78, 16.56) * mm, "mid": v(25.02, 16.36) * mm, "end": v(25.32, 16.32) * mm});
            skArc(sketch, "E7.81.1", {"start": v(25.32, 16.32) * mm, "mid": v(25.44, 16.34) * mm, "end": v(25.55, 16.38) * mm});
            skArc(sketch, "E7.81.2", {"start": v(25.86, 16.28) * mm, "mid": v(25.72, 16.38) * mm, "end": v(25.55, 16.38) * mm});
            skArc(sketch, "E7.81.3", {"start": v(26.04, 16) * mm, "mid": v(25.95, 16.14) * mm, "end": v(25.86, 16.28) * mm});
            skArc(sketch, "E7.81.4", {"start": v(26, 15.67) * mm, "mid": v(26.07, 15.82) * mm, "end": v(26.04, 16) * mm});
            skArc(sketch, "E7.81.5", {"start": v(26, 15.67) * mm, "mid": v(25.9, 15.59) * mm, "end": v(25.84, 15.5) * mm});
            skArc(sketch, "E7.81.6", {"start": v(25.84, 15.5) * mm, "mid": v(25.74, 15.2) * mm, "end": v(25.81, 14.9) * mm});
            skArc(sketch, "E7.82.0", {"start": v(23.65, 18.15) * mm, "mid": v(23.9, 17.96) * mm, "end": v(24.2, 17.94) * mm});
            skArc(sketch, "E7.82.1", {"start": v(24.2, 17.94) * mm, "mid": v(24.32, 17.97) * mm, "end": v(24.42, 18.02) * mm});
            skArc(sketch, "E7.82.2", {"start": v(24.74, 17.93) * mm, "mid": v(24.6, 18.03) * mm, "end": v(24.42, 18.02) * mm});
            skArc(sketch, "E7.82.3", {"start": v(24.94, 17.66) * mm, "mid": v(24.84, 17.8) * mm, "end": v(24.74, 17.93) * mm});
            skArc(sketch, "E7.82.4", {"start": v(24.91, 17.34) * mm, "mid": v(24.98, 17.5) * mm, "end": v(24.94, 17.66) * mm});
            skArc(sketch, "E7.82.5", {"start": v(24.91, 17.34) * mm, "mid": v(24.83, 17.25) * mm, "end": v(24.77, 17.15) * mm});
            skArc(sketch, "E7.82.6", {"start": v(24.77, 17.15) * mm, "mid": v(24.7, 16.85) * mm, "end": v(24.78, 16.56) * mm});
            skArc(sketch, "E7.83.0", {"start": v(22.41, 19.65) * mm, "mid": v(22.67, 19.49) * mm, "end": v(22.98, 19.48) * mm});
            skArc(sketch, "E7.83.1", {"start": v(22.98, 19.48) * mm, "mid": v(23.09, 19.52) * mm, "end": v(23.2, 19.57) * mm});
            skArc(sketch, "E7.83.2", {"start": v(23.51, 19.51) * mm, "mid": v(23.36, 19.6) * mm, "end": v(23.2, 19.57) * mm});
            skArc(sketch, "E7.83.3", {"start": v(23.73, 19.25) * mm, "mid": v(23.62, 19.38) * mm, "end": v(23.51, 19.51) * mm});
            skArc(sketch, "E7.83.4", {"start": v(23.72, 18.93) * mm, "mid": v(23.78, 19.1) * mm, "end": v(23.73, 19.25) * mm});
            skArc(sketch, "E7.83.5", {"start": v(23.72, 18.93) * mm, "mid": v(23.65, 18.84) * mm, "end": v(23.6, 18.74) * mm});
            skArc(sketch, "E7.83.6", {"start": v(23.6, 18.74) * mm, "mid": v(23.54, 18.43) * mm, "end": v(23.65, 18.15) * mm});
            skArc(sketch, "E7.84.0", {"start": v(21.08, 21.08) * mm, "mid": v(21.35, 20.93) * mm, "end": v(21.65, 20.95) * mm});
            skArc(sketch, "E7.84.1", {"start": v(21.65, 20.95) * mm, "mid": v(21.76, 21) * mm, "end": v(21.86, 21.05) * mm});
            skArc(sketch, "E7.84.2", {"start": v(22.19, 21.01) * mm, "mid": v(22.03, 21.09) * mm, "end": v(21.86, 21.05) * mm});
            skArc(sketch, "E7.84.3", {"start": v(22.42, 20.76) * mm, "mid": v(22.3, 20.89) * mm, "end": v(22.19, 21.01) * mm});
            skArc(sketch, "E7.84.4", {"start": v(22.43, 20.44) * mm, "mid": v(22.48, 20.6) * mm, "end": v(22.42, 20.76) * mm});
            skArc(sketch, "E7.84.5", {"start": v(22.43, 20.44) * mm, "mid": v(22.37, 20.34) * mm, "end": v(22.32, 20.24) * mm});
            skArc(sketch, "E7.84.6", {"start": v(22.32, 20.24) * mm, "mid": v(22.28, 19.93) * mm, "end": v(22.41, 19.65) * mm});
            skArc(sketch, "E7.85.0", {"start": v(19.65, 22.41) * mm, "mid": v(19.93, 22.28) * mm, "end": v(20.24, 22.32) * mm});
            skArc(sketch, "E7.85.1", {"start": v(20.24, 22.32) * mm, "mid": v(20.34, 22.37) * mm, "end": v(20.44, 22.43) * mm});
            skArc(sketch, "E7.85.2", {"start": v(20.76, 22.42) * mm, "mid": v(20.6, 22.48) * mm, "end": v(20.44, 22.43) * mm});
            skArc(sketch, "E7.85.3", {"start": v(21.01, 22.19) * mm, "mid": v(20.89, 22.3) * mm, "end": v(20.76, 22.42) * mm});
            skArc(sketch, "E7.85.4", {"start": v(21.05, 21.86) * mm, "mid": v(21.09, 22.03) * mm, "end": v(21.01, 22.19) * mm});
            skArc(sketch, "E7.85.5", {"start": v(21.05, 21.86) * mm, "mid": v(21, 21.76) * mm, "end": v(20.95, 21.65) * mm});
            skArc(sketch, "E7.85.6", {"start": v(20.95, 21.65) * mm, "mid": v(20.93, 21.35) * mm, "end": v(21.08, 21.08) * mm});
            skArc(sketch, "E7.86.0", {"start": v(18.15, 23.65) * mm, "mid": v(18.43, 23.54) * mm, "end": v(18.74, 23.6) * mm});
            skArc(sketch, "E7.86.1", {"start": v(18.74, 23.6) * mm, "mid": v(18.84, 23.65) * mm, "end": v(18.93, 23.72) * mm});
            skArc(sketch, "E7.86.2", {"start": v(19.25, 23.73) * mm, "mid": v(19.1, 23.78) * mm, "end": v(18.93, 23.72) * mm});
            skArc(sketch, "E7.86.3", {"start": v(19.51, 23.51) * mm, "mid": v(19.38, 23.62) * mm, "end": v(19.25, 23.73) * mm});
            skArc(sketch, "E7.86.4", {"start": v(19.57, 23.2) * mm, "mid": v(19.6, 23.36) * mm, "end": v(19.51, 23.51) * mm});
            skArc(sketch, "E7.86.5", {"start": v(19.57, 23.2) * mm, "mid": v(19.52, 23.09) * mm, "end": v(19.48, 22.98) * mm});
            skArc(sketch, "E7.86.6", {"start": v(19.48, 22.98) * mm, "mid": v(19.49, 22.67) * mm, "end": v(19.65, 22.41) * mm});
            skArc(sketch, "E7.87.0", {"start": v(16.56, 24.78) * mm, "mid": v(16.85, 24.7) * mm, "end": v(17.15, 24.77) * mm});
            skArc(sketch, "E7.87.1", {"start": v(17.15, 24.77) * mm, "mid": v(17.25, 24.83) * mm, "end": v(17.34, 24.91) * mm});
            skArc(sketch, "E7.87.2", {"start": v(17.66, 24.94) * mm, "mid": v(17.5, 24.98) * mm, "end": v(17.34, 24.91) * mm});
            skArc(sketch, "E7.87.3", {"start": v(17.93, 24.74) * mm, "mid": v(17.8, 24.84) * mm, "end": v(17.66, 24.94) * mm});
            skArc(sketch, "E7.87.4", {"start": v(18.02, 24.42) * mm, "mid": v(18.03, 24.6) * mm, "end": v(17.93, 24.74) * mm});
            skArc(sketch, "E7.87.5", {"start": v(18.02, 24.42) * mm, "mid": v(17.97, 24.32) * mm, "end": v(17.94, 24.2) * mm});
            skArc(sketch, "E7.87.6", {"start": v(17.94, 24.2) * mm, "mid": v(17.96, 23.9) * mm, "end": v(18.15, 23.65) * mm});
            skArc(sketch, "E7.88.0", {"start": v(14.9, 25.81) * mm, "mid": v(15.2, 25.74) * mm, "end": v(15.5, 25.84) * mm});
            skArc(sketch, "E7.88.1", {"start": v(15.5, 25.84) * mm, "mid": v(15.59, 25.9) * mm, "end": v(15.67, 26) * mm});
            skArc(sketch, "E7.88.2", {"start": v(16, 26.04) * mm, "mid": v(15.82, 26.07) * mm, "end": v(15.67, 26) * mm});
            skArc(sketch, "E7.88.3", {"start": v(16.28, 25.86) * mm, "mid": v(16.14, 25.95) * mm, "end": v(16, 26.04) * mm});
            skArc(sketch, "E7.88.4", {"start": v(16.38, 25.55) * mm, "mid": v(16.38, 25.72) * mm, "end": v(16.28, 25.86) * mm});
            skArc(sketch, "E7.88.5", {"start": v(16.38, 25.55) * mm, "mid": v(16.34, 25.44) * mm, "end": v(16.32, 25.32) * mm});
            skArc(sketch, "E7.88.6", {"start": v(16.32, 25.32) * mm, "mid": v(16.36, 25.02) * mm, "end": v(16.56, 24.78) * mm});
            skArc(sketch, "E7.89.0", {"start": v(13.18, 26.73) * mm, "mid": v(13.49, 26.68) * mm, "end": v(13.77, 26.8) * mm});
            skArc(sketch, "E7.89.1", {"start": v(13.77, 26.8) * mm, "mid": v(13.86, 26.87) * mm, "end": v(13.94, 26.96) * mm});
            skArc(sketch, "E7.89.2", {"start": v(14.26, 27.03) * mm, "mid": v(14.08, 27.05) * mm, "end": v(13.94, 26.96) * mm});
            skArc(sketch, "E7.89.3", {"start": v(14.55, 26.87) * mm, "mid": v(14.4, 26.95) * mm, "end": v(14.26, 27.03) * mm});
            skArc(sketch, "E7.89.4", {"start": v(14.67, 26.57) * mm, "mid": v(14.67, 26.74) * mm, "end": v(14.55, 26.87) * mm});
            skArc(sketch, "E7.89.5", {"start": v(14.67, 26.57) * mm, "mid": v(14.64, 26.45) * mm, "end": v(14.63, 26.34) * mm});
            skArc(sketch, "E7.89.6", {"start": v(14.63, 26.34) * mm, "mid": v(14.69, 26.04) * mm, "end": v(14.9, 25.81) * mm});
            skArc(sketch, "E7.90.0", {"start": v(11.4, 27.54) * mm, "mid": v(11.71, 27.5) * mm, "end": v(12, 27.64) * mm});
            skArc(sketch, "E7.90.1", {"start": v(12, 27.64) * mm, "mid": v(12.07, 27.72) * mm, "end": v(12.14, 27.81) * mm});
            skArc(sketch, "E7.90.2", {"start": v(12.46, 27.9) * mm, "mid": v(12.29, 27.91) * mm, "end": v(12.14, 27.81) * mm});
            skArc(sketch, "E7.90.3", {"start": v(12.76, 27.76) * mm, "mid": v(12.61, 27.83) * mm, "end": v(12.46, 27.9) * mm});
            skArc(sketch, "E7.90.4", {"start": v(12.9, 27.47) * mm, "mid": v(12.89, 27.64) * mm, "end": v(12.76, 27.76) * mm});
            skArc(sketch, "E7.90.5", {"start": v(12.9, 27.47) * mm, "mid": v(12.88, 27.35) * mm, "end": v(12.87, 27.24) * mm});
            skArc(sketch, "E7.90.6", {"start": v(12.87, 27.24) * mm, "mid": v(12.96, 26.94) * mm, "end": v(13.18, 26.73) * mm});
            skArc(sketch, "E7.91.0", {"start": v(9.58, 28.23) * mm, "mid": v(9.89, 28.21) * mm, "end": v(10.16, 28.36) * mm});
            skArc(sketch, "E7.91.1", {"start": v(10.16, 28.36) * mm, "mid": v(10.23, 28.45) * mm, "end": v(10.3, 28.55) * mm});
            skArc(sketch, "E7.91.2", {"start": v(10.6, 28.66) * mm, "mid": v(10.43, 28.66) * mm, "end": v(10.3, 28.55) * mm});
            skArc(sketch, "E7.91.3", {"start": v(10.92, 28.54) * mm, "mid": v(10.76, 28.6) * mm, "end": v(10.6, 28.66) * mm});
            skArc(sketch, "E7.91.4", {"start": v(11.08, 28.25) * mm, "mid": v(11.05, 28.43) * mm, "end": v(10.92, 28.54) * mm});
            skArc(sketch, "E7.91.5", {"start": v(11.08, 28.25) * mm, "mid": v(11.07, 28.14) * mm, "end": v(11.06, 28.02) * mm});
            skArc(sketch, "E7.91.6", {"start": v(11.06, 28.02) * mm, "mid": v(11.17, 27.73) * mm, "end": v(11.4, 27.54) * mm});
            skArc(sketch, "E7.92.0", {"start": v(7.71, 28.8) * mm, "mid": v(8.02, 28.8) * mm, "end": v(8.28, 28.97) * mm});
            skArc(sketch, "E7.92.1", {"start": v(8.28, 28.97) * mm, "mid": v(8.35, 29.06) * mm, "end": v(8.41, 29.16) * mm});
            skArc(sketch, "E7.92.2", {"start": v(8.7, 29.29) * mm, "mid": v(8.54, 29.28) * mm, "end": v(8.41, 29.16) * mm});
            skArc(sketch, "E7.92.3", {"start": v(9.03, 29.2) * mm, "mid": v(8.87, 29.24) * mm, "end": v(8.7, 29.29) * mm});
            skArc(sketch, "E7.92.4", {"start": v(9.2, 28.92) * mm, "mid": v(9.17, 29.09) * mm, "end": v(9.03, 29.2) * mm});
            skArc(sketch, "E7.92.5", {"start": v(9.2, 28.92) * mm, "mid": v(9.2, 28.8) * mm, "end": v(9.2, 28.69) * mm});
            skArc(sketch, "E7.92.6", {"start": v(9.2, 28.69) * mm, "mid": v(9.33, 28.4) * mm, "end": v(9.58, 28.23) * mm});
            skArc(sketch, "E7.93.0", {"start": v(5.82, 29.23) * mm, "mid": v(6.12, 29.26) * mm, "end": v(6.37, 29.45) * mm});
            skArc(sketch, "E7.93.1", {"start": v(6.37, 29.45) * mm, "mid": v(6.43, 29.54) * mm, "end": v(6.49, 29.65) * mm});
            skArc(sketch, "E7.93.2", {"start": v(6.77, 29.8) * mm, "mid": v(6.6, 29.77) * mm, "end": v(6.49, 29.65) * mm});
            skArc(sketch, "E7.93.3", {"start": v(7.1, 29.72) * mm, "mid": v(6.94, 29.76) * mm, "end": v(6.77, 29.8) * mm});
            skArc(sketch, "E7.93.4", {"start": v(7.3, 29.46) * mm, "mid": v(7.25, 29.62) * mm, "end": v(7.1, 29.72) * mm});
            skArc(sketch, "E7.93.5", {"start": v(7.3, 29.46) * mm, "mid": v(7.3, 29.34) * mm, "end": v(7.31, 29.23) * mm});
            skArc(sketch, "E7.93.6", {"start": v(7.31, 29.23) * mm, "mid": v(7.45, 28.95) * mm, "end": v(7.71, 28.8) * mm});
            skArc(sketch, "E7.94.0", {"start": v(3.9, 29.55) * mm, "mid": v(4.2, 29.6) * mm, "end": v(4.43, 29.8) * mm});
            skArc(sketch, "E7.94.1", {"start": v(4.43, 29.8) * mm, "mid": v(4.49, 29.9) * mm, "end": v(4.53, 30) * mm});
            skArc(sketch, "E7.94.2", {"start": v(4.81, 30.18) * mm, "mid": v(4.64, 30.14) * mm, "end": v(4.53, 30) * mm});
            skArc(sketch, "E7.94.3", {"start": v(5.14, 30.12) * mm, "mid": v(4.98, 30.15) * mm, "end": v(4.81, 30.18) * mm});
            skArc(sketch, "E7.94.4", {"start": v(5.35, 29.87) * mm, "mid": v(5.3, 30.04) * mm, "end": v(5.14, 30.12) * mm});
            skArc(sketch, "E7.94.5", {"start": v(5.35, 29.87) * mm, "mid": v(5.36, 29.76) * mm, "end": v(5.39, 29.64) * mm});
            skArc(sketch, "E7.94.6", {"start": v(5.39, 29.64) * mm, "mid": v(5.54, 29.38) * mm, "end": v(5.82, 29.23) * mm});
            skArc(sketch, "E7.95.0", {"start": v(1.95, 29.74) * mm, "mid": v(2.25, 29.8) * mm, "end": v(2.47, 30.03) * mm});
            skArc(sketch, "E7.95.1", {"start": v(2.47, 30.03) * mm, "mid": v(2.52, 30.13) * mm, "end": v(2.56, 30.24) * mm});
            skArc(sketch, "E7.95.2", {"start": v(2.83, 30.43) * mm, "mid": v(2.66, 30.38) * mm, "end": v(2.56, 30.24) * mm});
            skArc(sketch, "E7.95.3", {"start": v(3.16, 30.4) * mm, "mid": v(3, 30.4) * mm, "end": v(2.83, 30.43) * mm});
            skArc(sketch, "E7.95.4", {"start": v(3.39, 30.16) * mm, "mid": v(3.32, 30.32) * mm, "end": v(3.16, 30.4) * mm});
            skArc(sketch, "E7.95.5", {"start": v(3.39, 30.16) * mm, "mid": v(3.4, 30.04) * mm, "end": v(3.44, 29.93) * mm});
            skArc(sketch, "E7.95.6", {"start": v(3.44, 29.93) * mm, "mid": v(3.6, 29.68) * mm, "end": v(3.9, 29.55) * mm});
            skSolve(sketch);
        }
        {
            var Q0;
            Q0=makeQuery(id+"F0.imprint","IMPRINT",FACE,{"disambiguationData":[TD([[makeQuery(id+"F0.imprint","IMPRINT",EDGE,{"derivedFrom":sQuery(id+"F0.wireOp",EDGE,"E0")}),-1.0]])]});
            extrude(context, id + "F1", {"entities" : qUnion([Q0]), "depth" : 6.35 * mm, "offsetDistance" : 25.4 * mm});
        }
        {
            var Q0;
            Q0=makeQuery(id+"F1.opExtrude","CAP_FACE",FACE,{"disambiguationData":[OSD([sQuery(id+"F0.wireOp",EDGE,"E0"),sQuery(id+"F0.wireOp",EDGE,"E1"),sQuery(id+"F0.wireOp",EDGE,"E2"),sQuery(id+"F0.wireOp",EDGE,"E3"),sQuery(id+"F0.wireOp",EDGE,"E4.trimOffspring"),sQuery(id+"F0.wireOp",EDGE,"E5.filletArc"),sQuery(id+"F0.wireOp",EDGE,"E6.filletArc"),sQuery(id+"F0.wireOp",EDGE,"E7.1.0"),sQuery(id+"F0.wireOp",EDGE,"E7.1.1"),sQuery(id+"F0.wireOp",EDGE,"E7.1.2"),sQuery(id+"F0.wireOp",EDGE,"E7.1.3"),sQuery(id+"F0.wireOp",EDGE,"E7.1.4"),sQuery(id+"F0.wireOp",EDGE,"E7.1.5"),sQuery(id+"F0.wireOp",EDGE,"E7.1.6"),sQuery(id+"F0.wireOp",EDGE,"E7.2.0"),sQuery(id+"F0.wireOp",EDGE,"E7.2.1"),sQuery(id+"F0.wireOp",EDGE,"E7.2.2"),sQuery(id+"F0.wireOp",EDGE,"E7.2.3"),sQuery(id+"F0.wireOp",EDGE,"E7.2.4"),sQuery(id+"F0.wireOp",EDGE,"E7.2.5"),sQuery(id+"F0.wireOp",EDGE,"E7.2.6"),sQuery(id+"F0.wireOp",EDGE,"E7.3.0"),sQuery(id+"F0.wireOp",EDGE,"E7.3.1"),sQuery(id+"F0.wireOp",EDGE,"E7.3.2"),sQuery(id+"F0.wireOp",EDGE,"E7.3.3"),sQuery(id+"F0.wireOp",EDGE,"E7.3.4"),sQuery(id+"F0.wireOp",EDGE,"E7.3.5"),sQuery(id+"F0.wireOp",EDGE,"E7.3.6"),sQuery(id+"F0.wireOp",EDGE,"E7.4.0"),sQuery(id+"F0.wireOp",EDGE,"E7.4.1"),sQuery(id+"F0.wireOp",EDGE,"E7.4.2"),sQuery(id+"F0.wireOp",EDGE,"E7.4.3"),sQuery(id+"F0.wireOp",EDGE,"E7.4.4"),sQuery(id+"F0.wireOp",EDGE,"E7.4.5"),sQuery(id+"F0.wireOp",EDGE,"E7.4.6"),sQuery(id+"F0.wireOp",EDGE,"E7.5.0"),sQuery(id+"F0.wireOp",EDGE,"E7.5.1"),sQuery(id+"F0.wireOp",EDGE,"E7.5.2"),sQuery(id+"F0.wireOp",EDGE,"E7.5.3"),sQuery(id+"F0.wireOp",EDGE,"E7.5.4"),sQuery(id+"F0.wireOp",EDGE,"E7.5.5"),sQuery(id+"F0.wireOp",EDGE,"E7.5.6"),sQuery(id+"F0.wireOp",EDGE,"E7.6.0"),sQuery(id+"F0.wireOp",EDGE,"E7.6.1"),sQuery(id+"F0.wireOp",EDGE,"E7.6.2"),sQuery(id+"F0.wireOp",EDGE,"E7.6.3"),sQuery(id+"F0.wireOp",EDGE,"E7.6.4"),sQuery(id+"F0.wireOp",EDGE,"E7.6.5"),sQuery(id+"F0.wireOp",EDGE,"E7.6.6"),sQuery(id+"F0.wireOp",EDGE,"E7.7.0"),sQuery(id+"F0.wireOp",EDGE,"E7.7.1"),sQuery(id+"F0.wireOp",EDGE,"E7.7.2"),sQuery(id+"F0.wireOp",EDGE,"E7.7.3"),sQuery(id+"F0.wireOp",EDGE,"E7.7.4"),sQuery(id+"F0.wireOp",EDGE,"E7.7.5"),sQuery(id+"F0.wireOp",EDGE,"E7.7.6"),sQuery(id+"F0.wireOp",EDGE,"E7.8.0"),sQuery(id+"F0.wireOp",EDGE,"E7.8.1"),sQuery(id+"F0.wireOp",EDGE,"E7.8.2"),sQuery(id+"F0.wireOp",EDGE,"E7.8.3"),sQuery(id+"F0.wireOp",EDGE,"E7.8.4"),sQuery(id+"F0.wireOp",EDGE,"E7.8.5"),sQuery(id+"F0.wireOp",EDGE,"E7.8.6"),sQuery(id+"F0.wireOp",EDGE,"E7.9.0"),sQuery(id+"F0.wireOp",EDGE,"E7.9.1"),sQuery(id+"F0.wireOp",EDGE,"E7.9.2"),sQuery(id+"F0.wireOp",EDGE,"E7.9.3"),sQuery(id+"F0.wireOp",EDGE,"E7.9.4"),sQuery(id+"F0.wireOp",EDGE,"E7.9.5"),sQuery(id+"F0.wireOp",EDGE,"E7.9.6"),sQuery(id+"F0.wireOp",EDGE,"E7.10.0"),sQuery(id+"F0.wireOp",EDGE,"E7.10.1"),sQuery(id+"F0.wireOp",EDGE,"E7.10.2"),sQuery(id+"F0.wireOp",EDGE,"E7.10.3"),sQuery(id+"F0.wireOp",EDGE,"E7.10.4"),sQuery(id+"F0.wireOp",EDGE,"E7.10.5"),sQuery(id+"F0.wireOp",EDGE,"E7.10.6"),sQuery(id+"F0.wireOp",EDGE,"E7.11.0"),sQuery(id+"F0.wireOp",EDGE,"E7.11.1"),sQuery(id+"F0.wireOp",EDGE,"E7.11.2"),sQuery(id+"F0.wireOp",EDGE,"E7.11.3"),sQuery(id+"F0.wireOp",EDGE,"E7.11.4"),sQuery(id+"F0.wireOp",EDGE,"E7.11.5"),sQuery(id+"F0.wireOp",EDGE,"E7.11.6"),sQuery(id+"F0.wireOp",EDGE,"E7.12.0"),sQuery(id+"F0.wireOp",EDGE,"E7.12.1"),sQuery(id+"F0.wireOp",EDGE,"E7.12.2"),sQuery(id+"F0.wireOp",EDGE,"E7.12.3"),sQuery(id+"F0.wireOp",EDGE,"E7.12.4"),sQuery(id+"F0.wireOp",EDGE,"E7.12.5"),sQuery(id+"F0.wireOp",EDGE,"E7.12.6"),sQuery(id+"F0.wireOp",EDGE,"E7.13.0"),sQuery(id+"F0.wireOp",EDGE,"E7.13.1"),sQuery(id+"F0.wireOp",EDGE,"E7.13.2"),sQuery(id+"F0.wireOp",EDGE,"E7.13.3"),sQuery(id+"F0.wireOp",EDGE,"E7.13.4"),sQuery(id+"F0.wireOp",EDGE,"E7.13.5"),sQuery(id+"F0.wireOp",EDGE,"E7.13.6"),sQuery(id+"F0.wireOp",EDGE,"E7.14.0"),sQuery(id+"F0.wireOp",EDGE,"E7.14.1"),sQuery(id+"F0.wireOp",EDGE,"E7.14.2"),sQuery(id+"F0.wireOp",EDGE,"E7.14.3"),sQuery(id+"F0.wireOp",EDGE,"E7.14.4"),sQuery(id+"F0.wireOp",EDGE,"E7.14.5"),sQuery(id+"F0.wireOp",EDGE,"E7.14.6"),sQuery(id+"F0.wireOp",EDGE,"E7.15.0"),sQuery(id+"F0.wireOp",EDGE,"E7.15.1"),sQuery(id+"F0.wireOp",EDGE,"E7.15.2"),sQuery(id+"F0.wireOp",EDGE,"E7.15.3"),sQuery(id+"F0.wireOp",EDGE,"E7.15.4"),sQuery(id+"F0.wireOp",EDGE,"E7.15.5"),sQuery(id+"F0.wireOp",EDGE,"E7.15.6"),sQuery(id+"F0.wireOp",EDGE,"E7.16.0"),sQuery(id+"F0.wireOp",EDGE,"E7.16.1"),sQuery(id+"F0.wireOp",EDGE,"E7.16.2"),sQuery(id+"F0.wireOp",EDGE,"E7.16.3"),sQuery(id+"F0.wireOp",EDGE,"E7.16.4"),sQuery(id+"F0.wireOp",EDGE,"E7.16.5"),sQuery(id+"F0.wireOp",EDGE,"E7.16.6"),sQuery(id+"F0.wireOp",EDGE,"E7.17.0"),sQuery(id+"F0.wireOp",EDGE,"E7.17.1"),sQuery(id+"F0.wireOp",EDGE,"E7.17.2"),sQuery(id+"F0.wireOp",EDGE,"E7.17.3"),sQuery(id+"F0.wireOp",EDGE,"E7.17.4"),sQuery(id+"F0.wireOp",EDGE,"E7.17.5"),sQuery(id+"F0.wireOp",EDGE,"E7.17.6"),sQuery(id+"F0.wireOp",EDGE,"E7.18.0"),sQuery(id+"F0.wireOp",EDGE,"E7.18.1"),sQuery(id+"F0.wireOp",EDGE,"E7.18.2"),sQuery(id+"F0.wireOp",EDGE,"E7.18.3"),sQuery(id+"F0.wireOp",EDGE,"E7.18.4"),sQuery(id+"F0.wireOp",EDGE,"E7.18.5"),sQuery(id+"F0.wireOp",EDGE,"E7.18.6"),sQuery(id+"F0.wireOp",EDGE,"E7.19.0"),sQuery(id+"F0.wireOp",EDGE,"E7.19.1"),sQuery(id+"F0.wireOp",EDGE,"E7.19.2"),sQuery(id+"F0.wireOp",EDGE,"E7.19.3"),sQuery(id+"F0.wireOp",EDGE,"E7.19.4"),sQuery(id+"F0.wireOp",EDGE,"E7.19.5"),sQuery(id+"F0.wireOp",EDGE,"E7.19.6"),sQuery(id+"F0.wireOp",EDGE,"E7.20.0"),sQuery(id+"F0.wireOp",EDGE,"E7.20.1"),sQuery(id+"F0.wireOp",EDGE,"E7.20.2"),sQuery(id+"F0.wireOp",EDGE,"E7.20.3"),sQuery(id+"F0.wireOp",EDGE,"E7.20.4"),sQuery(id+"F0.wireOp",EDGE,"E7.20.5"),sQuery(id+"F0.wireOp",EDGE,"E7.20.6"),sQuery(id+"F0.wireOp",EDGE,"E7.21.0"),sQuery(id+"F0.wireOp",EDGE,"E7.21.1"),sQuery(id+"F0.wireOp",EDGE,"E7.21.2"),sQuery(id+"F0.wireOp",EDGE,"E7.21.3"),sQuery(id+"F0.wireOp",EDGE,"E7.21.4"),sQuery(id+"F0.wireOp",EDGE,"E7.21.5"),sQuery(id+"F0.wireOp",EDGE,"E7.21.6"),sQuery(id+"F0.wireOp",EDGE,"E7.22.0"),sQuery(id+"F0.wireOp",EDGE,"E7.22.1"),sQuery(id+"F0.wireOp",EDGE,"E7.22.2"),sQuery(id+"F0.wireOp",EDGE,"E7.22.3"),sQuery(id+"F0.wireOp",EDGE,"E7.22.4"),sQuery(id+"F0.wireOp",EDGE,"E7.22.5"),sQuery(id+"F0.wireOp",EDGE,"E7.22.6"),sQuery(id+"F0.wireOp",EDGE,"E7.23.0"),sQuery(id+"F0.wireOp",EDGE,"E7.23.1"),sQuery(id+"F0.wireOp",EDGE,"E7.23.2"),sQuery(id+"F0.wireOp",EDGE,"E7.23.3"),sQuery(id+"F0.wireOp",EDGE,"E7.23.4"),sQuery(id+"F0.wireOp",EDGE,"E7.23.5"),sQuery(id+"F0.wireOp",EDGE,"E7.23.6"),sQuery(id+"F0.wireOp",EDGE,"E7.24.0"),sQuery(id+"F0.wireOp",EDGE,"E7.24.1"),sQuery(id+"F0.wireOp",EDGE,"E7.24.2"),sQuery(id+"F0.wireOp",EDGE,"E7.24.3"),sQuery(id+"F0.wireOp",EDGE,"E7.24.4"),sQuery(id+"F0.wireOp",EDGE,"E7.24.5"),sQuery(id+"F0.wireOp",EDGE,"E7.24.6"),sQuery(id+"F0.wireOp",EDGE,"E7.25.0"),sQuery(id+"F0.wireOp",EDGE,"E7.25.1"),sQuery(id+"F0.wireOp",EDGE,"E7.25.2"),sQuery(id+"F0.wireOp",EDGE,"E7.25.3"),sQuery(id+"F0.wireOp",EDGE,"E7.25.4"),sQuery(id+"F0.wireOp",EDGE,"E7.25.5"),sQuery(id+"F0.wireOp",EDGE,"E7.25.6"),sQuery(id+"F0.wireOp",EDGE,"E7.26.0"),sQuery(id+"F0.wireOp",EDGE,"E7.26.1"),sQuery(id+"F0.wireOp",EDGE,"E7.26.2"),sQuery(id+"F0.wireOp",EDGE,"E7.26.3"),sQuery(id+"F0.wireOp",EDGE,"E7.26.4"),sQuery(id+"F0.wireOp",EDGE,"E7.26.5"),sQuery(id+"F0.wireOp",EDGE,"E7.26.6"),sQuery(id+"F0.wireOp",EDGE,"E7.27.0"),sQuery(id+"F0.wireOp",EDGE,"E7.27.1"),sQuery(id+"F0.wireOp",EDGE,"E7.27.2"),sQuery(id+"F0.wireOp",EDGE,"E7.27.3"),sQuery(id+"F0.wireOp",EDGE,"E7.27.4"),sQuery(id+"F0.wireOp",EDGE,"E7.27.5"),sQuery(id+"F0.wireOp",EDGE,"E7.27.6"),sQuery(id+"F0.wireOp",EDGE,"E7.28.0"),sQuery(id+"F0.wireOp",EDGE,"E7.28.1"),sQuery(id+"F0.wireOp",EDGE,"E7.28.2"),sQuery(id+"F0.wireOp",EDGE,"E7.28.3"),sQuery(id+"F0.wireOp",EDGE,"E7.28.4"),sQuery(id+"F0.wireOp",EDGE,"E7.28.5"),sQuery(id+"F0.wireOp",EDGE,"E7.28.6"),sQuery(id+"F0.wireOp",EDGE,"E7.29.0"),sQuery(id+"F0.wireOp",EDGE,"E7.29.1"),sQuery(id+"F0.wireOp",EDGE,"E7.29.2"),sQuery(id+"F0.wireOp",EDGE,"E7.29.3"),sQuery(id+"F0.wireOp",EDGE,"E7.29.4"),sQuery(id+"F0.wireOp",EDGE,"E7.29.5"),sQuery(id+"F0.wireOp",EDGE,"E7.29.6"),sQuery(id+"F0.wireOp",EDGE,"E7.30.0"),sQuery(id+"F0.wireOp",EDGE,"E7.30.1"),sQuery(id+"F0.wireOp",EDGE,"E7.30.2"),sQuery(id+"F0.wireOp",EDGE,"E7.30.3"),sQuery(id+"F0.wireOp",EDGE,"E7.30.4"),sQuery(id+"F0.wireOp",EDGE,"E7.30.5"),sQuery(id+"F0.wireOp",EDGE,"E7.30.6"),sQuery(id+"F0.wireOp",EDGE,"E7.31.0"),sQuery(id+"F0.wireOp",EDGE,"E7.31.1"),sQuery(id+"F0.wireOp",EDGE,"E7.31.2"),sQuery(id+"F0.wireOp",EDGE,"E7.31.3"),sQuery(id+"F0.wireOp",EDGE,"E7.31.4"),sQuery(id+"F0.wireOp",EDGE,"E7.31.5"),sQuery(id+"F0.wireOp",EDGE,"E7.31.6"),sQuery(id+"F0.wireOp",EDGE,"E7.32.0"),sQuery(id+"F0.wireOp",EDGE,"E7.32.1"),sQuery(id+"F0.wireOp",EDGE,"E7.32.2"),sQuery(id+"F0.wireOp",EDGE,"E7.32.3"),sQuery(id+"F0.wireOp",EDGE,"E7.32.4"),sQuery(id+"F0.wireOp",EDGE,"E7.32.5"),sQuery(id+"F0.wireOp",EDGE,"E7.32.6"),sQuery(id+"F0.wireOp",EDGE,"E7.33.0"),sQuery(id+"F0.wireOp",EDGE,"E7.33.1"),sQuery(id+"F0.wireOp",EDGE,"E7.33.2"),sQuery(id+"F0.wireOp",EDGE,"E7.33.3"),sQuery(id+"F0.wireOp",EDGE,"E7.33.4"),sQuery(id+"F0.wireOp",EDGE,"E7.33.5"),sQuery(id+"F0.wireOp",EDGE,"E7.33.6"),sQuery(id+"F0.wireOp",EDGE,"E7.34.0"),sQuery(id+"F0.wireOp",EDGE,"E7.34.1"),sQuery(id+"F0.wireOp",EDGE,"E7.34.2"),sQuery(id+"F0.wireOp",EDGE,"E7.34.3"),sQuery(id+"F0.wireOp",EDGE,"E7.34.4"),sQuery(id+"F0.wireOp",EDGE,"E7.34.5"),sQuery(id+"F0.wireOp",EDGE,"E7.34.6"),sQuery(id+"F0.wireOp",EDGE,"E7.35.0"),sQuery(id+"F0.wireOp",EDGE,"E7.35.1"),sQuery(id+"F0.wireOp",EDGE,"E7.35.2"),sQuery(id+"F0.wireOp",EDGE,"E7.35.3"),sQuery(id+"F0.wireOp",EDGE,"E7.35.4"),sQuery(id+"F0.wireOp",EDGE,"E7.35.5"),sQuery(id+"F0.wireOp",EDGE,"E7.35.6"),sQuery(id+"F0.wireOp",EDGE,"E7.36.0"),sQuery(id+"F0.wireOp",EDGE,"E7.36.1"),sQuery(id+"F0.wireOp",EDGE,"E7.36.2"),sQuery(id+"F0.wireOp",EDGE,"E7.36.3"),sQuery(id+"F0.wireOp",EDGE,"E7.36.4"),sQuery(id+"F0.wireOp",EDGE,"E7.36.5"),sQuery(id+"F0.wireOp",EDGE,"E7.36.6"),sQuery(id+"F0.wireOp",EDGE,"E7.37.0"),sQuery(id+"F0.wireOp",EDGE,"E7.37.1"),sQuery(id+"F0.wireOp",EDGE,"E7.37.2"),sQuery(id+"F0.wireOp",EDGE,"E7.37.3"),sQuery(id+"F0.wireOp",EDGE,"E7.37.4"),sQuery(id+"F0.wireOp",EDGE,"E7.37.5"),sQuery(id+"F0.wireOp",EDGE,"E7.37.6"),sQuery(id+"F0.wireOp",EDGE,"E7.38.0"),sQuery(id+"F0.wireOp",EDGE,"E7.38.1"),sQuery(id+"F0.wireOp",EDGE,"E7.38.2"),sQuery(id+"F0.wireOp",EDGE,"E7.38.3"),sQuery(id+"F0.wireOp",EDGE,"E7.38.4"),sQuery(id+"F0.wireOp",EDGE,"E7.38.5"),sQuery(id+"F0.wireOp",EDGE,"E7.38.6"),sQuery(id+"F0.wireOp",EDGE,"E7.39.0"),sQuery(id+"F0.wireOp",EDGE,"E7.39.1"),sQuery(id+"F0.wireOp",EDGE,"E7.39.2"),sQuery(id+"F0.wireOp",EDGE,"E7.39.3"),sQuery(id+"F0.wireOp",EDGE,"E7.39.4"),sQuery(id+"F0.wireOp",EDGE,"E7.39.5"),sQuery(id+"F0.wireOp",EDGE,"E7.39.6"),sQuery(id+"F0.wireOp",EDGE,"E7.40.0"),sQuery(id+"F0.wireOp",EDGE,"E7.40.1"),sQuery(id+"F0.wireOp",EDGE,"E7.40.2"),sQuery(id+"F0.wireOp",EDGE,"E7.40.3"),sQuery(id+"F0.wireOp",EDGE,"E7.40.4"),sQuery(id+"F0.wireOp",EDGE,"E7.40.5"),sQuery(id+"F0.wireOp",EDGE,"E7.40.6"),sQuery(id+"F0.wireOp",EDGE,"E7.41.0"),sQuery(id+"F0.wireOp",EDGE,"E7.41.1"),sQuery(id+"F0.wireOp",EDGE,"E7.41.2"),sQuery(id+"F0.wireOp",EDGE,"E7.41.3"),sQuery(id+"F0.wireOp",EDGE,"E7.41.4"),sQuery(id+"F0.wireOp",EDGE,"E7.41.5"),sQuery(id+"F0.wireOp",EDGE,"E7.41.6"),sQuery(id+"F0.wireOp",EDGE,"E7.42.0"),sQuery(id+"F0.wireOp",EDGE,"E7.42.1"),sQuery(id+"F0.wireOp",EDGE,"E7.42.2"),sQuery(id+"F0.wireOp",EDGE,"E7.42.3"),sQuery(id+"F0.wireOp",EDGE,"E7.42.4"),sQuery(id+"F0.wireOp",EDGE,"E7.42.5"),sQuery(id+"F0.wireOp",EDGE,"E7.42.6"),sQuery(id+"F0.wireOp",EDGE,"E7.43.0"),sQuery(id+"F0.wireOp",EDGE,"E7.43.1"),sQuery(id+"F0.wireOp",EDGE,"E7.43.2"),sQuery(id+"F0.wireOp",EDGE,"E7.43.3"),sQuery(id+"F0.wireOp",EDGE,"E7.43.4"),sQuery(id+"F0.wireOp",EDGE,"E7.43.5"),sQuery(id+"F0.wireOp",EDGE,"E7.43.6"),sQuery(id+"F0.wireOp",EDGE,"E7.44.0"),sQuery(id+"F0.wireOp",EDGE,"E7.44.1"),sQuery(id+"F0.wireOp",EDGE,"E7.44.2"),sQuery(id+"F0.wireOp",EDGE,"E7.44.3"),sQuery(id+"F0.wireOp",EDGE,"E7.44.4"),sQuery(id+"F0.wireOp",EDGE,"E7.44.5"),sQuery(id+"F0.wireOp",EDGE,"E7.44.6"),sQuery(id+"F0.wireOp",EDGE,"E7.45.0"),sQuery(id+"F0.wireOp",EDGE,"E7.45.1"),sQuery(id+"F0.wireOp",EDGE,"E7.45.2"),sQuery(id+"F0.wireOp",EDGE,"E7.45.3"),sQuery(id+"F0.wireOp",EDGE,"E7.45.4"),sQuery(id+"F0.wireOp",EDGE,"E7.45.5"),sQuery(id+"F0.wireOp",EDGE,"E7.45.6"),sQuery(id+"F0.wireOp",EDGE,"E7.46.0"),sQuery(id+"F0.wireOp",EDGE,"E7.46.1"),sQuery(id+"F0.wireOp",EDGE,"E7.46.2"),sQuery(id+"F0.wireOp",EDGE,"E7.46.3"),sQuery(id+"F0.wireOp",EDGE,"E7.46.4"),sQuery(id+"F0.wireOp",EDGE,"E7.46.5"),sQuery(id+"F0.wireOp",EDGE,"E7.46.6"),sQuery(id+"F0.wireOp",EDGE,"E7.47.0"),sQuery(id+"F0.wireOp",EDGE,"E7.47.1"),sQuery(id+"F0.wireOp",EDGE,"E7.47.2"),sQuery(id+"F0.wireOp",EDGE,"E7.47.3"),sQuery(id+"F0.wireOp",EDGE,"E7.47.4"),sQuery(id+"F0.wireOp",EDGE,"E7.47.5"),sQuery(id+"F0.wireOp",EDGE,"E7.47.6"),sQuery(id+"F0.wireOp",EDGE,"E7.48.0"),sQuery(id+"F0.wireOp",EDGE,"E7.48.1"),sQuery(id+"F0.wireOp",EDGE,"E7.48.2"),sQuery(id+"F0.wireOp",EDGE,"E7.48.3"),sQuery(id+"F0.wireOp",EDGE,"E7.48.4"),sQuery(id+"F0.wireOp",EDGE,"E7.48.5"),sQuery(id+"F0.wireOp",EDGE,"E7.48.6"),sQuery(id+"F0.wireOp",EDGE,"E7.49.0"),sQuery(id+"F0.wireOp",EDGE,"E7.49.1"),sQuery(id+"F0.wireOp",EDGE,"E7.49.2"),sQuery(id+"F0.wireOp",EDGE,"E7.49.3"),sQuery(id+"F0.wireOp",EDGE,"E7.49.4"),sQuery(id+"F0.wireOp",EDGE,"E7.49.5"),sQuery(id+"F0.wireOp",EDGE,"E7.49.6"),sQuery(id+"F0.wireOp",EDGE,"E7.50.0"),sQuery(id+"F0.wireOp",EDGE,"E7.50.1"),sQuery(id+"F0.wireOp",EDGE,"E7.50.2"),sQuery(id+"F0.wireOp",EDGE,"E7.50.3"),sQuery(id+"F0.wireOp",EDGE,"E7.50.4"),sQuery(id+"F0.wireOp",EDGE,"E7.50.5"),sQuery(id+"F0.wireOp",EDGE,"E7.50.6"),sQuery(id+"F0.wireOp",EDGE,"E7.51.0"),sQuery(id+"F0.wireOp",EDGE,"E7.51.1"),sQuery(id+"F0.wireOp",EDGE,"E7.51.2"),sQuery(id+"F0.wireOp",EDGE,"E7.51.3"),sQuery(id+"F0.wireOp",EDGE,"E7.51.4"),sQuery(id+"F0.wireOp",EDGE,"E7.51.5"),sQuery(id+"F0.wireOp",EDGE,"E7.51.6"),sQuery(id+"F0.wireOp",EDGE,"E7.52.0"),sQuery(id+"F0.wireOp",EDGE,"E7.52.1"),sQuery(id+"F0.wireOp",EDGE,"E7.52.2"),sQuery(id+"F0.wireOp",EDGE,"E7.52.3"),sQuery(id+"F0.wireOp",EDGE,"E7.52.4"),sQuery(id+"F0.wireOp",EDGE,"E7.52.5"),sQuery(id+"F0.wireOp",EDGE,"E7.52.6"),sQuery(id+"F0.wireOp",EDGE,"E7.53.0"),sQuery(id+"F0.wireOp",EDGE,"E7.53.1"),sQuery(id+"F0.wireOp",EDGE,"E7.53.2"),sQuery(id+"F0.wireOp",EDGE,"E7.53.3"),sQuery(id+"F0.wireOp",EDGE,"E7.53.4"),sQuery(id+"F0.wireOp",EDGE,"E7.53.5"),sQuery(id+"F0.wireOp",EDGE,"E7.53.6"),sQuery(id+"F0.wireOp",EDGE,"E7.54.0"),sQuery(id+"F0.wireOp",EDGE,"E7.54.1"),sQuery(id+"F0.wireOp",EDGE,"E7.54.2"),sQuery(id+"F0.wireOp",EDGE,"E7.54.3"),sQuery(id+"F0.wireOp",EDGE,"E7.54.4"),sQuery(id+"F0.wireOp",EDGE,"E7.54.5"),sQuery(id+"F0.wireOp",EDGE,"E7.54.6"),sQuery(id+"F0.wireOp",EDGE,"E7.55.0"),sQuery(id+"F0.wireOp",EDGE,"E7.55.1"),sQuery(id+"F0.wireOp",EDGE,"E7.55.2"),sQuery(id+"F0.wireOp",EDGE,"E7.55.3"),sQuery(id+"F0.wireOp",EDGE,"E7.55.4"),sQuery(id+"F0.wireOp",EDGE,"E7.55.5"),sQuery(id+"F0.wireOp",EDGE,"E7.55.6"),sQuery(id+"F0.wireOp",EDGE,"E7.56.0"),sQuery(id+"F0.wireOp",EDGE,"E7.56.1"),sQuery(id+"F0.wireOp",EDGE,"E7.56.2"),sQuery(id+"F0.wireOp",EDGE,"E7.56.3"),sQuery(id+"F0.wireOp",EDGE,"E7.56.4"),sQuery(id+"F0.wireOp",EDGE,"E7.56.5"),sQuery(id+"F0.wireOp",EDGE,"E7.56.6"),sQuery(id+"F0.wireOp",EDGE,"E7.57.0"),sQuery(id+"F0.wireOp",EDGE,"E7.57.1"),sQuery(id+"F0.wireOp",EDGE,"E7.57.2"),sQuery(id+"F0.wireOp",EDGE,"E7.57.3"),sQuery(id+"F0.wireOp",EDGE,"E7.57.4"),sQuery(id+"F0.wireOp",EDGE,"E7.57.5"),sQuery(id+"F0.wireOp",EDGE,"E7.57.6"),sQuery(id+"F0.wireOp",EDGE,"E7.58.0"),sQuery(id+"F0.wireOp",EDGE,"E7.58.1"),sQuery(id+"F0.wireOp",EDGE,"E7.58.2"),sQuery(id+"F0.wireOp",EDGE,"E7.58.3"),sQuery(id+"F0.wireOp",EDGE,"E7.58.4"),sQuery(id+"F0.wireOp",EDGE,"E7.58.5"),sQuery(id+"F0.wireOp",EDGE,"E7.58.6"),sQuery(id+"F0.wireOp",EDGE,"E7.59.0"),sQuery(id+"F0.wireOp",EDGE,"E7.59.1"),sQuery(id+"F0.wireOp",EDGE,"E7.59.2"),sQuery(id+"F0.wireOp",EDGE,"E7.59.3"),sQuery(id+"F0.wireOp",EDGE,"E7.59.4"),sQuery(id+"F0.wireOp",EDGE,"E7.59.5"),sQuery(id+"F0.wireOp",EDGE,"E7.59.6"),sQuery(id+"F0.wireOp",EDGE,"E7.60.0"),sQuery(id+"F0.wireOp",EDGE,"E7.60.1"),sQuery(id+"F0.wireOp",EDGE,"E7.60.2"),sQuery(id+"F0.wireOp",EDGE,"E7.60.3"),sQuery(id+"F0.wireOp",EDGE,"E7.60.4"),sQuery(id+"F0.wireOp",EDGE,"E7.60.5"),sQuery(id+"F0.wireOp",EDGE,"E7.60.6"),sQuery(id+"F0.wireOp",EDGE,"E7.61.0"),sQuery(id+"F0.wireOp",EDGE,"E7.61.1"),sQuery(id+"F0.wireOp",EDGE,"E7.61.2"),sQuery(id+"F0.wireOp",EDGE,"E7.61.3"),sQuery(id+"F0.wireOp",EDGE,"E7.61.4"),sQuery(id+"F0.wireOp",EDGE,"E7.61.5"),sQuery(id+"F0.wireOp",EDGE,"E7.61.6"),sQuery(id+"F0.wireOp",EDGE,"E7.62.0"),sQuery(id+"F0.wireOp",EDGE,"E7.62.1"),sQuery(id+"F0.wireOp",EDGE,"E7.62.2"),sQuery(id+"F0.wireOp",EDGE,"E7.62.3"),sQuery(id+"F0.wireOp",EDGE,"E7.62.4"),sQuery(id+"F0.wireOp",EDGE,"E7.62.5"),sQuery(id+"F0.wireOp",EDGE,"E7.62.6"),sQuery(id+"F0.wireOp",EDGE,"E7.63.0"),sQuery(id+"F0.wireOp",EDGE,"E7.63.1"),sQuery(id+"F0.wireOp",EDGE,"E7.63.2"),sQuery(id+"F0.wireOp",EDGE,"E7.63.3"),sQuery(id+"F0.wireOp",EDGE,"E7.63.4"),sQuery(id+"F0.wireOp",EDGE,"E7.63.5"),sQuery(id+"F0.wireOp",EDGE,"E7.63.6"),sQuery(id+"F0.wireOp",EDGE,"E7.64.0"),sQuery(id+"F0.wireOp",EDGE,"E7.64.1"),sQuery(id+"F0.wireOp",EDGE,"E7.64.2"),sQuery(id+"F0.wireOp",EDGE,"E7.64.3"),sQuery(id+"F0.wireOp",EDGE,"E7.64.4"),sQuery(id+"F0.wireOp",EDGE,"E7.64.5"),sQuery(id+"F0.wireOp",EDGE,"E7.64.6"),sQuery(id+"F0.wireOp",EDGE,"E7.65.0"),sQuery(id+"F0.wireOp",EDGE,"E7.65.1"),sQuery(id+"F0.wireOp",EDGE,"E7.65.2"),sQuery(id+"F0.wireOp",EDGE,"E7.65.3"),sQuery(id+"F0.wireOp",EDGE,"E7.65.4"),sQuery(id+"F0.wireOp",EDGE,"E7.65.5"),sQuery(id+"F0.wireOp",EDGE,"E7.65.6"),sQuery(id+"F0.wireOp",EDGE,"E7.66.0"),sQuery(id+"F0.wireOp",EDGE,"E7.66.1"),sQuery(id+"F0.wireOp",EDGE,"E7.66.2"),sQuery(id+"F0.wireOp",EDGE,"E7.66.3"),sQuery(id+"F0.wireOp",EDGE,"E7.66.4"),sQuery(id+"F0.wireOp",EDGE,"E7.66.5"),sQuery(id+"F0.wireOp",EDGE,"E7.66.6"),sQuery(id+"F0.wireOp",EDGE,"E7.67.0"),sQuery(id+"F0.wireOp",EDGE,"E7.67.1"),sQuery(id+"F0.wireOp",EDGE,"E7.67.2"),sQuery(id+"F0.wireOp",EDGE,"E7.67.3"),sQuery(id+"F0.wireOp",EDGE,"E7.67.4"),sQuery(id+"F0.wireOp",EDGE,"E7.67.5"),sQuery(id+"F0.wireOp",EDGE,"E7.67.6"),sQuery(id+"F0.wireOp",EDGE,"E7.68.0"),sQuery(id+"F0.wireOp",EDGE,"E7.68.1"),sQuery(id+"F0.wireOp",EDGE,"E7.68.2"),sQuery(id+"F0.wireOp",EDGE,"E7.68.3"),sQuery(id+"F0.wireOp",EDGE,"E7.68.4"),sQuery(id+"F0.wireOp",EDGE,"E7.68.5"),sQuery(id+"F0.wireOp",EDGE,"E7.68.6"),sQuery(id+"F0.wireOp",EDGE,"E7.69.0"),sQuery(id+"F0.wireOp",EDGE,"E7.69.1"),sQuery(id+"F0.wireOp",EDGE,"E7.69.2"),sQuery(id+"F0.wireOp",EDGE,"E7.69.3"),sQuery(id+"F0.wireOp",EDGE,"E7.69.4"),sQuery(id+"F0.wireOp",EDGE,"E7.69.5"),sQuery(id+"F0.wireOp",EDGE,"E7.69.6"),sQuery(id+"F0.wireOp",EDGE,"E7.70.0"),sQuery(id+"F0.wireOp",EDGE,"E7.70.1"),sQuery(id+"F0.wireOp",EDGE,"E7.70.2"),sQuery(id+"F0.wireOp",EDGE,"E7.70.3"),sQuery(id+"F0.wireOp",EDGE,"E7.70.4"),sQuery(id+"F0.wireOp",EDGE,"E7.70.5"),sQuery(id+"F0.wireOp",EDGE,"E7.70.6"),sQuery(id+"F0.wireOp",EDGE,"E7.71.0"),sQuery(id+"F0.wireOp",EDGE,"E7.71.1"),sQuery(id+"F0.wireOp",EDGE,"E7.71.2"),sQuery(id+"F0.wireOp",EDGE,"E7.71.3"),sQuery(id+"F0.wireOp",EDGE,"E7.71.4"),sQuery(id+"F0.wireOp",EDGE,"E7.71.5"),sQuery(id+"F0.wireOp",EDGE,"E7.71.6"),sQuery(id+"F0.wireOp",EDGE,"E7.72.0"),sQuery(id+"F0.wireOp",EDGE,"E7.72.1"),sQuery(id+"F0.wireOp",EDGE,"E7.72.2"),sQuery(id+"F0.wireOp",EDGE,"E7.72.3"),sQuery(id+"F0.wireOp",EDGE,"E7.72.4"),sQuery(id+"F0.wireOp",EDGE,"E7.72.5"),sQuery(id+"F0.wireOp",EDGE,"E7.72.6"),sQuery(id+"F0.wireOp",EDGE,"E7.73.0"),sQuery(id+"F0.wireOp",EDGE,"E7.73.1"),sQuery(id+"F0.wireOp",EDGE,"E7.73.2"),sQuery(id+"F0.wireOp",EDGE,"E7.73.3"),sQuery(id+"F0.wireOp",EDGE,"E7.73.4"),sQuery(id+"F0.wireOp",EDGE,"E7.73.5"),sQuery(id+"F0.wireOp",EDGE,"E7.73.6"),sQuery(id+"F0.wireOp",EDGE,"E7.74.0"),sQuery(id+"F0.wireOp",EDGE,"E7.74.1"),sQuery(id+"F0.wireOp",EDGE,"E7.74.2"),sQuery(id+"F0.wireOp",EDGE,"E7.74.3"),sQuery(id+"F0.wireOp",EDGE,"E7.74.4"),sQuery(id+"F0.wireOp",EDGE,"E7.74.5"),sQuery(id+"F0.wireOp",EDGE,"E7.74.6"),sQuery(id+"F0.wireOp",EDGE,"E7.75.0"),sQuery(id+"F0.wireOp",EDGE,"E7.75.1"),sQuery(id+"F0.wireOp",EDGE,"E7.75.2"),sQuery(id+"F0.wireOp",EDGE,"E7.75.3"),sQuery(id+"F0.wireOp",EDGE,"E7.75.4"),sQuery(id+"F0.wireOp",EDGE,"E7.75.5"),sQuery(id+"F0.wireOp",EDGE,"E7.75.6"),sQuery(id+"F0.wireOp",EDGE,"E7.76.0"),sQuery(id+"F0.wireOp",EDGE,"E7.76.1"),sQuery(id+"F0.wireOp",EDGE,"E7.76.2"),sQuery(id+"F0.wireOp",EDGE,"E7.76.3"),sQuery(id+"F0.wireOp",EDGE,"E7.76.4"),sQuery(id+"F0.wireOp",EDGE,"E7.76.5"),sQuery(id+"F0.wireOp",EDGE,"E7.76.6"),sQuery(id+"F0.wireOp",EDGE,"E7.77.0"),sQuery(id+"F0.wireOp",EDGE,"E7.77.1"),sQuery(id+"F0.wireOp",EDGE,"E7.77.2"),sQuery(id+"F0.wireOp",EDGE,"E7.77.3"),sQuery(id+"F0.wireOp",EDGE,"E7.77.4"),sQuery(id+"F0.wireOp",EDGE,"E7.77.5"),sQuery(id+"F0.wireOp",EDGE,"E7.77.6"),sQuery(id+"F0.wireOp",EDGE,"E7.78.0"),sQuery(id+"F0.wireOp",EDGE,"E7.78.1"),sQuery(id+"F0.wireOp",EDGE,"E7.78.2"),sQuery(id+"F0.wireOp",EDGE,"E7.78.3"),sQuery(id+"F0.wireOp",EDGE,"E7.78.4"),sQuery(id+"F0.wireOp",EDGE,"E7.78.5"),sQuery(id+"F0.wireOp",EDGE,"E7.78.6"),sQuery(id+"F0.wireOp",EDGE,"E7.79.0"),sQuery(id+"F0.wireOp",EDGE,"E7.79.1"),sQuery(id+"F0.wireOp",EDGE,"E7.79.2"),sQuery(id+"F0.wireOp",EDGE,"E7.79.3"),sQuery(id+"F0.wireOp",EDGE,"E7.79.4"),sQuery(id+"F0.wireOp",EDGE,"E7.79.5"),sQuery(id+"F0.wireOp",EDGE,"E7.79.6"),sQuery(id+"F0.wireOp",EDGE,"E7.80.0"),sQuery(id+"F0.wireOp",EDGE,"E7.80.1"),sQuery(id+"F0.wireOp",EDGE,"E7.80.2"),sQuery(id+"F0.wireOp",EDGE,"E7.80.3"),sQuery(id+"F0.wireOp",EDGE,"E7.80.4"),sQuery(id+"F0.wireOp",EDGE,"E7.80.5"),sQuery(id+"F0.wireOp",EDGE,"E7.80.6"),sQuery(id+"F0.wireOp",EDGE,"E7.81.0"),sQuery(id+"F0.wireOp",EDGE,"E7.81.1"),sQuery(id+"F0.wireOp",EDGE,"E7.81.2"),sQuery(id+"F0.wireOp",EDGE,"E7.81.3"),sQuery(id+"F0.wireOp",EDGE,"E7.81.4"),sQuery(id+"F0.wireOp",EDGE,"E7.81.5"),sQuery(id+"F0.wireOp",EDGE,"E7.81.6"),sQuery(id+"F0.wireOp",EDGE,"E7.82.0"),sQuery(id+"F0.wireOp",EDGE,"E7.82.1"),sQuery(id+"F0.wireOp",EDGE,"E7.82.2"),sQuery(id+"F0.wireOp",EDGE,"E7.82.3"),sQuery(id+"F0.wireOp",EDGE,"E7.82.4"),sQuery(id+"F0.wireOp",EDGE,"E7.82.5"),sQuery(id+"F0.wireOp",EDGE,"E7.82.6"),sQuery(id+"F0.wireOp",EDGE,"E7.83.0"),sQuery(id+"F0.wireOp",EDGE,"E7.83.1"),sQuery(id+"F0.wireOp",EDGE,"E7.83.2"),sQuery(id+"F0.wireOp",EDGE,"E7.83.3"),sQuery(id+"F0.wireOp",EDGE,"E7.83.4"),sQuery(id+"F0.wireOp",EDGE,"E7.83.5"),sQuery(id+"F0.wireOp",EDGE,"E7.83.6"),sQuery(id+"F0.wireOp",EDGE,"E7.84.0"),sQuery(id+"F0.wireOp",EDGE,"E7.84.1"),sQuery(id+"F0.wireOp",EDGE,"E7.84.2"),sQuery(id+"F0.wireOp",EDGE,"E7.84.3"),sQuery(id+"F0.wireOp",EDGE,"E7.84.4"),sQuery(id+"F0.wireOp",EDGE,"E7.84.5"),sQuery(id+"F0.wireOp",EDGE,"E7.84.6"),sQuery(id+"F0.wireOp",EDGE,"E7.85.0"),sQuery(id+"F0.wireOp",EDGE,"E7.85.1"),sQuery(id+"F0.wireOp",EDGE,"E7.85.2"),sQuery(id+"F0.wireOp",EDGE,"E7.85.3"),sQuery(id+"F0.wireOp",EDGE,"E7.85.4"),sQuery(id+"F0.wireOp",EDGE,"E7.85.5"),sQuery(id+"F0.wireOp",EDGE,"E7.85.6"),sQuery(id+"F0.wireOp",EDGE,"E7.86.0"),sQuery(id+"F0.wireOp",EDGE,"E7.86.1"),sQuery(id+"F0.wireOp",EDGE,"E7.86.2"),sQuery(id+"F0.wireOp",EDGE,"E7.86.3"),sQuery(id+"F0.wireOp",EDGE,"E7.86.4"),sQuery(id+"F0.wireOp",EDGE,"E7.86.5"),sQuery(id+"F0.wireOp",EDGE,"E7.86.6"),sQuery(id+"F0.wireOp",EDGE,"E7.87.0"),sQuery(id+"F0.wireOp",EDGE,"E7.87.1"),sQuery(id+"F0.wireOp",EDGE,"E7.87.2"),sQuery(id+"F0.wireOp",EDGE,"E7.87.3"),sQuery(id+"F0.wireOp",EDGE,"E7.87.4"),sQuery(id+"F0.wireOp",EDGE,"E7.87.5"),sQuery(id+"F0.wireOp",EDGE,"E7.87.6"),sQuery(id+"F0.wireOp",EDGE,"E7.88.0"),sQuery(id+"F0.wireOp",EDGE,"E7.88.1"),sQuery(id+"F0.wireOp",EDGE,"E7.88.2"),sQuery(id+"F0.wireOp",EDGE,"E7.88.3"),sQuery(id+"F0.wireOp",EDGE,"E7.88.4"),sQuery(id+"F0.wireOp",EDGE,"E7.88.5"),sQuery(id+"F0.wireOp",EDGE,"E7.88.6"),sQuery(id+"F0.wireOp",EDGE,"E7.89.0"),sQuery(id+"F0.wireOp",EDGE,"E7.89.1"),sQuery(id+"F0.wireOp",EDGE,"E7.89.2"),sQuery(id+"F0.wireOp",EDGE,"E7.89.3"),sQuery(id+"F0.wireOp",EDGE,"E7.89.4"),sQuery(id+"F0.wireOp",EDGE,"E7.89.5"),sQuery(id+"F0.wireOp",EDGE,"E7.89.6"),sQuery(id+"F0.wireOp",EDGE,"E7.90.0"),sQuery(id+"F0.wireOp",EDGE,"E7.90.1"),sQuery(id+"F0.wireOp",EDGE,"E7.90.2"),sQuery(id+"F0.wireOp",EDGE,"E7.90.3"),sQuery(id+"F0.wireOp",EDGE,"E7.90.4"),sQuery(id+"F0.wireOp",EDGE,"E7.90.5"),sQuery(id+"F0.wireOp",EDGE,"E7.90.6"),sQuery(id+"F0.wireOp",EDGE,"E7.91.0"),sQuery(id+"F0.wireOp",EDGE,"E7.91.1"),sQuery(id+"F0.wireOp",EDGE,"E7.91.2"),sQuery(id+"F0.wireOp",EDGE,"E7.91.3"),sQuery(id+"F0.wireOp",EDGE,"E7.91.4"),sQuery(id+"F0.wireOp",EDGE,"E7.91.5"),sQuery(id+"F0.wireOp",EDGE,"E7.91.6"),sQuery(id+"F0.wireOp",EDGE,"E7.92.0"),sQuery(id+"F0.wireOp",EDGE,"E7.92.1"),sQuery(id+"F0.wireOp",EDGE,"E7.92.2"),sQuery(id+"F0.wireOp",EDGE,"E7.92.3"),sQuery(id+"F0.wireOp",EDGE,"E7.92.4"),sQuery(id+"F0.wireOp",EDGE,"E7.92.5"),sQuery(id+"F0.wireOp",EDGE,"E7.92.6"),sQuery(id+"F0.wireOp",EDGE,"E7.93.0"),sQuery(id+"F0.wireOp",EDGE,"E7.93.1"),sQuery(id+"F0.wireOp",EDGE,"E7.93.2"),sQuery(id+"F0.wireOp",EDGE,"E7.93.3"),sQuery(id+"F0.wireOp",EDGE,"E7.93.4"),sQuery(id+"F0.wireOp",EDGE,"E7.93.5"),sQuery(id+"F0.wireOp",EDGE,"E7.93.6"),sQuery(id+"F0.wireOp",EDGE,"E7.94.0"),sQuery(id+"F0.wireOp",EDGE,"E7.94.1"),sQuery(id+"F0.wireOp",EDGE,"E7.94.2"),sQuery(id+"F0.wireOp",EDGE,"E7.94.3"),sQuery(id+"F0.wireOp",EDGE,"E7.94.4"),sQuery(id+"F0.wireOp",EDGE,"E7.94.5"),sQuery(id+"F0.wireOp",EDGE,"E7.94.6"),sQuery(id+"F0.wireOp",EDGE,"E7.95.0"),sQuery(id+"F0.wireOp",EDGE,"E7.95.1"),sQuery(id+"F0.wireOp",EDGE,"E7.95.2"),sQuery(id+"F0.wireOp",EDGE,"E7.95.3"),sQuery(id+"F0.wireOp",EDGE,"E7.95.4"),sQuery(id+"F0.wireOp",EDGE,"E7.95.5"),sQuery(id+"F0.wireOp",EDGE,"E7.95.6")])],"isStart":false});
            var sketch = newSketch(context, id + "F2", { "sketchPlane" : qUnion([Q0])});
            skCircle(sketch, "E8", {"center": v(0, 0) * mm, "radius": 31.75 * mm});
            skSolve(sketch);
        }
        {
            var Q0;
            Q0 = qSketchRegion(id + "F2", true);
            extrude(context, id + "F3", {"entities" : qUnion([Q0]), "operationType" : NewBodyOperationType.ADD, "depth" : 1 * mm, "offsetDistance" : 25.4 * mm});
        }
        {
            var Q0;
            Q0=makeQuery(id+"F1.opExtrude","CAP_FACE",FACE,{"disambiguationData":[OSD([sQuery(id+"F0.wireOp",EDGE,"E0"),sQuery(id+"F0.wireOp",EDGE,"E1"),sQuery(id+"F0.wireOp",EDGE,"E2"),sQuery(id+"F0.wireOp",EDGE,"E3"),sQuery(id+"F0.wireOp",EDGE,"E4.trimOffspring"),sQuery(id+"F0.wireOp",EDGE,"E5.filletArc"),sQuery(id+"F0.wireOp",EDGE,"E6.filletArc"),sQuery(id+"F0.wireOp",EDGE,"E7.1.0"),sQuery(id+"F0.wireOp",EDGE,"E7.1.1"),sQuery(id+"F0.wireOp",EDGE,"E7.1.2"),sQuery(id+"F0.wireOp",EDGE,"E7.1.3"),sQuery(id+"F0.wireOp",EDGE,"E7.1.4"),sQuery(id+"F0.wireOp",EDGE,"E7.1.5"),sQuery(id+"F0.wireOp",EDGE,"E7.1.6"),sQuery(id+"F0.wireOp",EDGE,"E7.2.0"),sQuery(id+"F0.wireOp",EDGE,"E7.2.1"),sQuery(id+"F0.wireOp",EDGE,"E7.2.2"),sQuery(id+"F0.wireOp",EDGE,"E7.2.3"),sQuery(id+"F0.wireOp",EDGE,"E7.2.4"),sQuery(id+"F0.wireOp",EDGE,"E7.2.5"),sQuery(id+"F0.wireOp",EDGE,"E7.2.6"),sQuery(id+"F0.wireOp",EDGE,"E7.3.0"),sQuery(id+"F0.wireOp",EDGE,"E7.3.1"),sQuery(id+"F0.wireOp",EDGE,"E7.3.2"),sQuery(id+"F0.wireOp",EDGE,"E7.3.3"),sQuery(id+"F0.wireOp",EDGE,"E7.3.4"),sQuery(id+"F0.wireOp",EDGE,"E7.3.5"),sQuery(id+"F0.wireOp",EDGE,"E7.3.6"),sQuery(id+"F0.wireOp",EDGE,"E7.4.0"),sQuery(id+"F0.wireOp",EDGE,"E7.4.1"),sQuery(id+"F0.wireOp",EDGE,"E7.4.2"),sQuery(id+"F0.wireOp",EDGE,"E7.4.3"),sQuery(id+"F0.wireOp",EDGE,"E7.4.4"),sQuery(id+"F0.wireOp",EDGE,"E7.4.5"),sQuery(id+"F0.wireOp",EDGE,"E7.4.6"),sQuery(id+"F0.wireOp",EDGE,"E7.5.0"),sQuery(id+"F0.wireOp",EDGE,"E7.5.1"),sQuery(id+"F0.wireOp",EDGE,"E7.5.2"),sQuery(id+"F0.wireOp",EDGE,"E7.5.3"),sQuery(id+"F0.wireOp",EDGE,"E7.5.4"),sQuery(id+"F0.wireOp",EDGE,"E7.5.5"),sQuery(id+"F0.wireOp",EDGE,"E7.5.6"),sQuery(id+"F0.wireOp",EDGE,"E7.6.0"),sQuery(id+"F0.wireOp",EDGE,"E7.6.1"),sQuery(id+"F0.wireOp",EDGE,"E7.6.2"),sQuery(id+"F0.wireOp",EDGE,"E7.6.3"),sQuery(id+"F0.wireOp",EDGE,"E7.6.4"),sQuery(id+"F0.wireOp",EDGE,"E7.6.5"),sQuery(id+"F0.wireOp",EDGE,"E7.6.6"),sQuery(id+"F0.wireOp",EDGE,"E7.7.0"),sQuery(id+"F0.wireOp",EDGE,"E7.7.1"),sQuery(id+"F0.wireOp",EDGE,"E7.7.2"),sQuery(id+"F0.wireOp",EDGE,"E7.7.3"),sQuery(id+"F0.wireOp",EDGE,"E7.7.4"),sQuery(id+"F0.wireOp",EDGE,"E7.7.5"),sQuery(id+"F0.wireOp",EDGE,"E7.7.6"),sQuery(id+"F0.wireOp",EDGE,"E7.8.0"),sQuery(id+"F0.wireOp",EDGE,"E7.8.1"),sQuery(id+"F0.wireOp",EDGE,"E7.8.2"),sQuery(id+"F0.wireOp",EDGE,"E7.8.3"),sQuery(id+"F0.wireOp",EDGE,"E7.8.4"),sQuery(id+"F0.wireOp",EDGE,"E7.8.5"),sQuery(id+"F0.wireOp",EDGE,"E7.8.6"),sQuery(id+"F0.wireOp",EDGE,"E7.9.0"),sQuery(id+"F0.wireOp",EDGE,"E7.9.1"),sQuery(id+"F0.wireOp",EDGE,"E7.9.2"),sQuery(id+"F0.wireOp",EDGE,"E7.9.3"),sQuery(id+"F0.wireOp",EDGE,"E7.9.4"),sQuery(id+"F0.wireOp",EDGE,"E7.9.5"),sQuery(id+"F0.wireOp",EDGE,"E7.9.6"),sQuery(id+"F0.wireOp",EDGE,"E7.10.0"),sQuery(id+"F0.wireOp",EDGE,"E7.10.1"),sQuery(id+"F0.wireOp",EDGE,"E7.10.2"),sQuery(id+"F0.wireOp",EDGE,"E7.10.3"),sQuery(id+"F0.wireOp",EDGE,"E7.10.4"),sQuery(id+"F0.wireOp",EDGE,"E7.10.5"),sQuery(id+"F0.wireOp",EDGE,"E7.10.6"),sQuery(id+"F0.wireOp",EDGE,"E7.11.0"),sQuery(id+"F0.wireOp",EDGE,"E7.11.1"),sQuery(id+"F0.wireOp",EDGE,"E7.11.2"),sQuery(id+"F0.wireOp",EDGE,"E7.11.3"),sQuery(id+"F0.wireOp",EDGE,"E7.11.4"),sQuery(id+"F0.wireOp",EDGE,"E7.11.5"),sQuery(id+"F0.wireOp",EDGE,"E7.11.6"),sQuery(id+"F0.wireOp",EDGE,"E7.12.0"),sQuery(id+"F0.wireOp",EDGE,"E7.12.1"),sQuery(id+"F0.wireOp",EDGE,"E7.12.2"),sQuery(id+"F0.wireOp",EDGE,"E7.12.3"),sQuery(id+"F0.wireOp",EDGE,"E7.12.4"),sQuery(id+"F0.wireOp",EDGE,"E7.12.5"),sQuery(id+"F0.wireOp",EDGE,"E7.12.6"),sQuery(id+"F0.wireOp",EDGE,"E7.13.0"),sQuery(id+"F0.wireOp",EDGE,"E7.13.1"),sQuery(id+"F0.wireOp",EDGE,"E7.13.2"),sQuery(id+"F0.wireOp",EDGE,"E7.13.3"),sQuery(id+"F0.wireOp",EDGE,"E7.13.4"),sQuery(id+"F0.wireOp",EDGE,"E7.13.5"),sQuery(id+"F0.wireOp",EDGE,"E7.13.6"),sQuery(id+"F0.wireOp",EDGE,"E7.14.0"),sQuery(id+"F0.wireOp",EDGE,"E7.14.1"),sQuery(id+"F0.wireOp",EDGE,"E7.14.2"),sQuery(id+"F0.wireOp",EDGE,"E7.14.3"),sQuery(id+"F0.wireOp",EDGE,"E7.14.4"),sQuery(id+"F0.wireOp",EDGE,"E7.14.5"),sQuery(id+"F0.wireOp",EDGE,"E7.14.6"),sQuery(id+"F0.wireOp",EDGE,"E7.15.0"),sQuery(id+"F0.wireOp",EDGE,"E7.15.1"),sQuery(id+"F0.wireOp",EDGE,"E7.15.2"),sQuery(id+"F0.wireOp",EDGE,"E7.15.3"),sQuery(id+"F0.wireOp",EDGE,"E7.15.4"),sQuery(id+"F0.wireOp",EDGE,"E7.15.5"),sQuery(id+"F0.wireOp",EDGE,"E7.15.6"),sQuery(id+"F0.wireOp",EDGE,"E7.16.0"),sQuery(id+"F0.wireOp",EDGE,"E7.16.1"),sQuery(id+"F0.wireOp",EDGE,"E7.16.2"),sQuery(id+"F0.wireOp",EDGE,"E7.16.3"),sQuery(id+"F0.wireOp",EDGE,"E7.16.4"),sQuery(id+"F0.wireOp",EDGE,"E7.16.5"),sQuery(id+"F0.wireOp",EDGE,"E7.16.6"),sQuery(id+"F0.wireOp",EDGE,"E7.17.0"),sQuery(id+"F0.wireOp",EDGE,"E7.17.1"),sQuery(id+"F0.wireOp",EDGE,"E7.17.2"),sQuery(id+"F0.wireOp",EDGE,"E7.17.3"),sQuery(id+"F0.wireOp",EDGE,"E7.17.4"),sQuery(id+"F0.wireOp",EDGE,"E7.17.5"),sQuery(id+"F0.wireOp",EDGE,"E7.17.6"),sQuery(id+"F0.wireOp",EDGE,"E7.18.0"),sQuery(id+"F0.wireOp",EDGE,"E7.18.1"),sQuery(id+"F0.wireOp",EDGE,"E7.18.2"),sQuery(id+"F0.wireOp",EDGE,"E7.18.3"),sQuery(id+"F0.wireOp",EDGE,"E7.18.4"),sQuery(id+"F0.wireOp",EDGE,"E7.18.5"),sQuery(id+"F0.wireOp",EDGE,"E7.18.6"),sQuery(id+"F0.wireOp",EDGE,"E7.19.0"),sQuery(id+"F0.wireOp",EDGE,"E7.19.1"),sQuery(id+"F0.wireOp",EDGE,"E7.19.2"),sQuery(id+"F0.wireOp",EDGE,"E7.19.3"),sQuery(id+"F0.wireOp",EDGE,"E7.19.4"),sQuery(id+"F0.wireOp",EDGE,"E7.19.5"),sQuery(id+"F0.wireOp",EDGE,"E7.19.6"),sQuery(id+"F0.wireOp",EDGE,"E7.20.0"),sQuery(id+"F0.wireOp",EDGE,"E7.20.1"),sQuery(id+"F0.wireOp",EDGE,"E7.20.2"),sQuery(id+"F0.wireOp",EDGE,"E7.20.3"),sQuery(id+"F0.wireOp",EDGE,"E7.20.4"),sQuery(id+"F0.wireOp",EDGE,"E7.20.5"),sQuery(id+"F0.wireOp",EDGE,"E7.20.6"),sQuery(id+"F0.wireOp",EDGE,"E7.21.0"),sQuery(id+"F0.wireOp",EDGE,"E7.21.1"),sQuery(id+"F0.wireOp",EDGE,"E7.21.2"),sQuery(id+"F0.wireOp",EDGE,"E7.21.3"),sQuery(id+"F0.wireOp",EDGE,"E7.21.4"),sQuery(id+"F0.wireOp",EDGE,"E7.21.5"),sQuery(id+"F0.wireOp",EDGE,"E7.21.6"),sQuery(id+"F0.wireOp",EDGE,"E7.22.0"),sQuery(id+"F0.wireOp",EDGE,"E7.22.1"),sQuery(id+"F0.wireOp",EDGE,"E7.22.2"),sQuery(id+"F0.wireOp",EDGE,"E7.22.3"),sQuery(id+"F0.wireOp",EDGE,"E7.22.4"),sQuery(id+"F0.wireOp",EDGE,"E7.22.5"),sQuery(id+"F0.wireOp",EDGE,"E7.22.6"),sQuery(id+"F0.wireOp",EDGE,"E7.23.0"),sQuery(id+"F0.wireOp",EDGE,"E7.23.1"),sQuery(id+"F0.wireOp",EDGE,"E7.23.2"),sQuery(id+"F0.wireOp",EDGE,"E7.23.3"),sQuery(id+"F0.wireOp",EDGE,"E7.23.4"),sQuery(id+"F0.wireOp",EDGE,"E7.23.5"),sQuery(id+"F0.wireOp",EDGE,"E7.23.6"),sQuery(id+"F0.wireOp",EDGE,"E7.24.0"),sQuery(id+"F0.wireOp",EDGE,"E7.24.1"),sQuery(id+"F0.wireOp",EDGE,"E7.24.2"),sQuery(id+"F0.wireOp",EDGE,"E7.24.3"),sQuery(id+"F0.wireOp",EDGE,"E7.24.4"),sQuery(id+"F0.wireOp",EDGE,"E7.24.5"),sQuery(id+"F0.wireOp",EDGE,"E7.24.6"),sQuery(id+"F0.wireOp",EDGE,"E7.25.0"),sQuery(id+"F0.wireOp",EDGE,"E7.25.1"),sQuery(id+"F0.wireOp",EDGE,"E7.25.2"),sQuery(id+"F0.wireOp",EDGE,"E7.25.3"),sQuery(id+"F0.wireOp",EDGE,"E7.25.4"),sQuery(id+"F0.wireOp",EDGE,"E7.25.5"),sQuery(id+"F0.wireOp",EDGE,"E7.25.6"),sQuery(id+"F0.wireOp",EDGE,"E7.26.0"),sQuery(id+"F0.wireOp",EDGE,"E7.26.1"),sQuery(id+"F0.wireOp",EDGE,"E7.26.2"),sQuery(id+"F0.wireOp",EDGE,"E7.26.3"),sQuery(id+"F0.wireOp",EDGE,"E7.26.4"),sQuery(id+"F0.wireOp",EDGE,"E7.26.5"),sQuery(id+"F0.wireOp",EDGE,"E7.26.6"),sQuery(id+"F0.wireOp",EDGE,"E7.27.0"),sQuery(id+"F0.wireOp",EDGE,"E7.27.1"),sQuery(id+"F0.wireOp",EDGE,"E7.27.2"),sQuery(id+"F0.wireOp",EDGE,"E7.27.3"),sQuery(id+"F0.wireOp",EDGE,"E7.27.4"),sQuery(id+"F0.wireOp",EDGE,"E7.27.5"),sQuery(id+"F0.wireOp",EDGE,"E7.27.6"),sQuery(id+"F0.wireOp",EDGE,"E7.28.0"),sQuery(id+"F0.wireOp",EDGE,"E7.28.1"),sQuery(id+"F0.wireOp",EDGE,"E7.28.2"),sQuery(id+"F0.wireOp",EDGE,"E7.28.3"),sQuery(id+"F0.wireOp",EDGE,"E7.28.4"),sQuery(id+"F0.wireOp",EDGE,"E7.28.5"),sQuery(id+"F0.wireOp",EDGE,"E7.28.6"),sQuery(id+"F0.wireOp",EDGE,"E7.29.0"),sQuery(id+"F0.wireOp",EDGE,"E7.29.1"),sQuery(id+"F0.wireOp",EDGE,"E7.29.2"),sQuery(id+"F0.wireOp",EDGE,"E7.29.3"),sQuery(id+"F0.wireOp",EDGE,"E7.29.4"),sQuery(id+"F0.wireOp",EDGE,"E7.29.5"),sQuery(id+"F0.wireOp",EDGE,"E7.29.6"),sQuery(id+"F0.wireOp",EDGE,"E7.30.0"),sQuery(id+"F0.wireOp",EDGE,"E7.30.1"),sQuery(id+"F0.wireOp",EDGE,"E7.30.2"),sQuery(id+"F0.wireOp",EDGE,"E7.30.3"),sQuery(id+"F0.wireOp",EDGE,"E7.30.4"),sQuery(id+"F0.wireOp",EDGE,"E7.30.5"),sQuery(id+"F0.wireOp",EDGE,"E7.30.6"),sQuery(id+"F0.wireOp",EDGE,"E7.31.0"),sQuery(id+"F0.wireOp",EDGE,"E7.31.1"),sQuery(id+"F0.wireOp",EDGE,"E7.31.2"),sQuery(id+"F0.wireOp",EDGE,"E7.31.3"),sQuery(id+"F0.wireOp",EDGE,"E7.31.4"),sQuery(id+"F0.wireOp",EDGE,"E7.31.5"),sQuery(id+"F0.wireOp",EDGE,"E7.31.6"),sQuery(id+"F0.wireOp",EDGE,"E7.32.0"),sQuery(id+"F0.wireOp",EDGE,"E7.32.1"),sQuery(id+"F0.wireOp",EDGE,"E7.32.2"),sQuery(id+"F0.wireOp",EDGE,"E7.32.3"),sQuery(id+"F0.wireOp",EDGE,"E7.32.4"),sQuery(id+"F0.wireOp",EDGE,"E7.32.5"),sQuery(id+"F0.wireOp",EDGE,"E7.32.6"),sQuery(id+"F0.wireOp",EDGE,"E7.33.0"),sQuery(id+"F0.wireOp",EDGE,"E7.33.1"),sQuery(id+"F0.wireOp",EDGE,"E7.33.2"),sQuery(id+"F0.wireOp",EDGE,"E7.33.3"),sQuery(id+"F0.wireOp",EDGE,"E7.33.4"),sQuery(id+"F0.wireOp",EDGE,"E7.33.5"),sQuery(id+"F0.wireOp",EDGE,"E7.33.6"),sQuery(id+"F0.wireOp",EDGE,"E7.34.0"),sQuery(id+"F0.wireOp",EDGE,"E7.34.1"),sQuery(id+"F0.wireOp",EDGE,"E7.34.2"),sQuery(id+"F0.wireOp",EDGE,"E7.34.3"),sQuery(id+"F0.wireOp",EDGE,"E7.34.4"),sQuery(id+"F0.wireOp",EDGE,"E7.34.5"),sQuery(id+"F0.wireOp",EDGE,"E7.34.6"),sQuery(id+"F0.wireOp",EDGE,"E7.35.0"),sQuery(id+"F0.wireOp",EDGE,"E7.35.1"),sQuery(id+"F0.wireOp",EDGE,"E7.35.2"),sQuery(id+"F0.wireOp",EDGE,"E7.35.3"),sQuery(id+"F0.wireOp",EDGE,"E7.35.4"),sQuery(id+"F0.wireOp",EDGE,"E7.35.5"),sQuery(id+"F0.wireOp",EDGE,"E7.35.6"),sQuery(id+"F0.wireOp",EDGE,"E7.36.0"),sQuery(id+"F0.wireOp",EDGE,"E7.36.1"),sQuery(id+"F0.wireOp",EDGE,"E7.36.2"),sQuery(id+"F0.wireOp",EDGE,"E7.36.3"),sQuery(id+"F0.wireOp",EDGE,"E7.36.4"),sQuery(id+"F0.wireOp",EDGE,"E7.36.5"),sQuery(id+"F0.wireOp",EDGE,"E7.36.6"),sQuery(id+"F0.wireOp",EDGE,"E7.37.0"),sQuery(id+"F0.wireOp",EDGE,"E7.37.1"),sQuery(id+"F0.wireOp",EDGE,"E7.37.2"),sQuery(id+"F0.wireOp",EDGE,"E7.37.3"),sQuery(id+"F0.wireOp",EDGE,"E7.37.4"),sQuery(id+"F0.wireOp",EDGE,"E7.37.5"),sQuery(id+"F0.wireOp",EDGE,"E7.37.6"),sQuery(id+"F0.wireOp",EDGE,"E7.38.0"),sQuery(id+"F0.wireOp",EDGE,"E7.38.1"),sQuery(id+"F0.wireOp",EDGE,"E7.38.2"),sQuery(id+"F0.wireOp",EDGE,"E7.38.3"),sQuery(id+"F0.wireOp",EDGE,"E7.38.4"),sQuery(id+"F0.wireOp",EDGE,"E7.38.5"),sQuery(id+"F0.wireOp",EDGE,"E7.38.6"),sQuery(id+"F0.wireOp",EDGE,"E7.39.0"),sQuery(id+"F0.wireOp",EDGE,"E7.39.1"),sQuery(id+"F0.wireOp",EDGE,"E7.39.2"),sQuery(id+"F0.wireOp",EDGE,"E7.39.3"),sQuery(id+"F0.wireOp",EDGE,"E7.39.4"),sQuery(id+"F0.wireOp",EDGE,"E7.39.5"),sQuery(id+"F0.wireOp",EDGE,"E7.39.6"),sQuery(id+"F0.wireOp",EDGE,"E7.40.0"),sQuery(id+"F0.wireOp",EDGE,"E7.40.1"),sQuery(id+"F0.wireOp",EDGE,"E7.40.2"),sQuery(id+"F0.wireOp",EDGE,"E7.40.3"),sQuery(id+"F0.wireOp",EDGE,"E7.40.4"),sQuery(id+"F0.wireOp",EDGE,"E7.40.5"),sQuery(id+"F0.wireOp",EDGE,"E7.40.6"),sQuery(id+"F0.wireOp",EDGE,"E7.41.0"),sQuery(id+"F0.wireOp",EDGE,"E7.41.1"),sQuery(id+"F0.wireOp",EDGE,"E7.41.2"),sQuery(id+"F0.wireOp",EDGE,"E7.41.3"),sQuery(id+"F0.wireOp",EDGE,"E7.41.4"),sQuery(id+"F0.wireOp",EDGE,"E7.41.5"),sQuery(id+"F0.wireOp",EDGE,"E7.41.6"),sQuery(id+"F0.wireOp",EDGE,"E7.42.0"),sQuery(id+"F0.wireOp",EDGE,"E7.42.1"),sQuery(id+"F0.wireOp",EDGE,"E7.42.2"),sQuery(id+"F0.wireOp",EDGE,"E7.42.3"),sQuery(id+"F0.wireOp",EDGE,"E7.42.4"),sQuery(id+"F0.wireOp",EDGE,"E7.42.5"),sQuery(id+"F0.wireOp",EDGE,"E7.42.6"),sQuery(id+"F0.wireOp",EDGE,"E7.43.0"),sQuery(id+"F0.wireOp",EDGE,"E7.43.1"),sQuery(id+"F0.wireOp",EDGE,"E7.43.2"),sQuery(id+"F0.wireOp",EDGE,"E7.43.3"),sQuery(id+"F0.wireOp",EDGE,"E7.43.4"),sQuery(id+"F0.wireOp",EDGE,"E7.43.5"),sQuery(id+"F0.wireOp",EDGE,"E7.43.6"),sQuery(id+"F0.wireOp",EDGE,"E7.44.0"),sQuery(id+"F0.wireOp",EDGE,"E7.44.1"),sQuery(id+"F0.wireOp",EDGE,"E7.44.2"),sQuery(id+"F0.wireOp",EDGE,"E7.44.3"),sQuery(id+"F0.wireOp",EDGE,"E7.44.4"),sQuery(id+"F0.wireOp",EDGE,"E7.44.5"),sQuery(id+"F0.wireOp",EDGE,"E7.44.6"),sQuery(id+"F0.wireOp",EDGE,"E7.45.0"),sQuery(id+"F0.wireOp",EDGE,"E7.45.1"),sQuery(id+"F0.wireOp",EDGE,"E7.45.2"),sQuery(id+"F0.wireOp",EDGE,"E7.45.3"),sQuery(id+"F0.wireOp",EDGE,"E7.45.4"),sQuery(id+"F0.wireOp",EDGE,"E7.45.5"),sQuery(id+"F0.wireOp",EDGE,"E7.45.6"),sQuery(id+"F0.wireOp",EDGE,"E7.46.0"),sQuery(id+"F0.wireOp",EDGE,"E7.46.1"),sQuery(id+"F0.wireOp",EDGE,"E7.46.2"),sQuery(id+"F0.wireOp",EDGE,"E7.46.3"),sQuery(id+"F0.wireOp",EDGE,"E7.46.4"),sQuery(id+"F0.wireOp",EDGE,"E7.46.5"),sQuery(id+"F0.wireOp",EDGE,"E7.46.6"),sQuery(id+"F0.wireOp",EDGE,"E7.47.0"),sQuery(id+"F0.wireOp",EDGE,"E7.47.1"),sQuery(id+"F0.wireOp",EDGE,"E7.47.2"),sQuery(id+"F0.wireOp",EDGE,"E7.47.3"),sQuery(id+"F0.wireOp",EDGE,"E7.47.4"),sQuery(id+"F0.wireOp",EDGE,"E7.47.5"),sQuery(id+"F0.wireOp",EDGE,"E7.47.6"),sQuery(id+"F0.wireOp",EDGE,"E7.48.0"),sQuery(id+"F0.wireOp",EDGE,"E7.48.1"),sQuery(id+"F0.wireOp",EDGE,"E7.48.2"),sQuery(id+"F0.wireOp",EDGE,"E7.48.3"),sQuery(id+"F0.wireOp",EDGE,"E7.48.4"),sQuery(id+"F0.wireOp",EDGE,"E7.48.5"),sQuery(id+"F0.wireOp",EDGE,"E7.48.6"),sQuery(id+"F0.wireOp",EDGE,"E7.49.0"),sQuery(id+"F0.wireOp",EDGE,"E7.49.1"),sQuery(id+"F0.wireOp",EDGE,"E7.49.2"),sQuery(id+"F0.wireOp",EDGE,"E7.49.3"),sQuery(id+"F0.wireOp",EDGE,"E7.49.4"),sQuery(id+"F0.wireOp",EDGE,"E7.49.5"),sQuery(id+"F0.wireOp",EDGE,"E7.49.6"),sQuery(id+"F0.wireOp",EDGE,"E7.50.0"),sQuery(id+"F0.wireOp",EDGE,"E7.50.1"),sQuery(id+"F0.wireOp",EDGE,"E7.50.2"),sQuery(id+"F0.wireOp",EDGE,"E7.50.3"),sQuery(id+"F0.wireOp",EDGE,"E7.50.4"),sQuery(id+"F0.wireOp",EDGE,"E7.50.5"),sQuery(id+"F0.wireOp",EDGE,"E7.50.6"),sQuery(id+"F0.wireOp",EDGE,"E7.51.0"),sQuery(id+"F0.wireOp",EDGE,"E7.51.1"),sQuery(id+"F0.wireOp",EDGE,"E7.51.2"),sQuery(id+"F0.wireOp",EDGE,"E7.51.3"),sQuery(id+"F0.wireOp",EDGE,"E7.51.4"),sQuery(id+"F0.wireOp",EDGE,"E7.51.5"),sQuery(id+"F0.wireOp",EDGE,"E7.51.6"),sQuery(id+"F0.wireOp",EDGE,"E7.52.0"),sQuery(id+"F0.wireOp",EDGE,"E7.52.1"),sQuery(id+"F0.wireOp",EDGE,"E7.52.2"),sQuery(id+"F0.wireOp",EDGE,"E7.52.3"),sQuery(id+"F0.wireOp",EDGE,"E7.52.4"),sQuery(id+"F0.wireOp",EDGE,"E7.52.5"),sQuery(id+"F0.wireOp",EDGE,"E7.52.6"),sQuery(id+"F0.wireOp",EDGE,"E7.53.0"),sQuery(id+"F0.wireOp",EDGE,"E7.53.1"),sQuery(id+"F0.wireOp",EDGE,"E7.53.2"),sQuery(id+"F0.wireOp",EDGE,"E7.53.3"),sQuery(id+"F0.wireOp",EDGE,"E7.53.4"),sQuery(id+"F0.wireOp",EDGE,"E7.53.5"),sQuery(id+"F0.wireOp",EDGE,"E7.53.6"),sQuery(id+"F0.wireOp",EDGE,"E7.54.0"),sQuery(id+"F0.wireOp",EDGE,"E7.54.1"),sQuery(id+"F0.wireOp",EDGE,"E7.54.2"),sQuery(id+"F0.wireOp",EDGE,"E7.54.3"),sQuery(id+"F0.wireOp",EDGE,"E7.54.4"),sQuery(id+"F0.wireOp",EDGE,"E7.54.5"),sQuery(id+"F0.wireOp",EDGE,"E7.54.6"),sQuery(id+"F0.wireOp",EDGE,"E7.55.0"),sQuery(id+"F0.wireOp",EDGE,"E7.55.1"),sQuery(id+"F0.wireOp",EDGE,"E7.55.2"),sQuery(id+"F0.wireOp",EDGE,"E7.55.3"),sQuery(id+"F0.wireOp",EDGE,"E7.55.4"),sQuery(id+"F0.wireOp",EDGE,"E7.55.5"),sQuery(id+"F0.wireOp",EDGE,"E7.55.6"),sQuery(id+"F0.wireOp",EDGE,"E7.56.0"),sQuery(id+"F0.wireOp",EDGE,"E7.56.1"),sQuery(id+"F0.wireOp",EDGE,"E7.56.2"),sQuery(id+"F0.wireOp",EDGE,"E7.56.3"),sQuery(id+"F0.wireOp",EDGE,"E7.56.4"),sQuery(id+"F0.wireOp",EDGE,"E7.56.5"),sQuery(id+"F0.wireOp",EDGE,"E7.56.6"),sQuery(id+"F0.wireOp",EDGE,"E7.57.0"),sQuery(id+"F0.wireOp",EDGE,"E7.57.1"),sQuery(id+"F0.wireOp",EDGE,"E7.57.2"),sQuery(id+"F0.wireOp",EDGE,"E7.57.3"),sQuery(id+"F0.wireOp",EDGE,"E7.57.4"),sQuery(id+"F0.wireOp",EDGE,"E7.57.5"),sQuery(id+"F0.wireOp",EDGE,"E7.57.6"),sQuery(id+"F0.wireOp",EDGE,"E7.58.0"),sQuery(id+"F0.wireOp",EDGE,"E7.58.1"),sQuery(id+"F0.wireOp",EDGE,"E7.58.2"),sQuery(id+"F0.wireOp",EDGE,"E7.58.3"),sQuery(id+"F0.wireOp",EDGE,"E7.58.4"),sQuery(id+"F0.wireOp",EDGE,"E7.58.5"),sQuery(id+"F0.wireOp",EDGE,"E7.58.6"),sQuery(id+"F0.wireOp",EDGE,"E7.59.0"),sQuery(id+"F0.wireOp",EDGE,"E7.59.1"),sQuery(id+"F0.wireOp",EDGE,"E7.59.2"),sQuery(id+"F0.wireOp",EDGE,"E7.59.3"),sQuery(id+"F0.wireOp",EDGE,"E7.59.4"),sQuery(id+"F0.wireOp",EDGE,"E7.59.5"),sQuery(id+"F0.wireOp",EDGE,"E7.59.6"),sQuery(id+"F0.wireOp",EDGE,"E7.60.0"),sQuery(id+"F0.wireOp",EDGE,"E7.60.1"),sQuery(id+"F0.wireOp",EDGE,"E7.60.2"),sQuery(id+"F0.wireOp",EDGE,"E7.60.3"),sQuery(id+"F0.wireOp",EDGE,"E7.60.4"),sQuery(id+"F0.wireOp",EDGE,"E7.60.5"),sQuery(id+"F0.wireOp",EDGE,"E7.60.6"),sQuery(id+"F0.wireOp",EDGE,"E7.61.0"),sQuery(id+"F0.wireOp",EDGE,"E7.61.1"),sQuery(id+"F0.wireOp",EDGE,"E7.61.2"),sQuery(id+"F0.wireOp",EDGE,"E7.61.3"),sQuery(id+"F0.wireOp",EDGE,"E7.61.4"),sQuery(id+"F0.wireOp",EDGE,"E7.61.5"),sQuery(id+"F0.wireOp",EDGE,"E7.61.6"),sQuery(id+"F0.wireOp",EDGE,"E7.62.0"),sQuery(id+"F0.wireOp",EDGE,"E7.62.1"),sQuery(id+"F0.wireOp",EDGE,"E7.62.2"),sQuery(id+"F0.wireOp",EDGE,"E7.62.3"),sQuery(id+"F0.wireOp",EDGE,"E7.62.4"),sQuery(id+"F0.wireOp",EDGE,"E7.62.5"),sQuery(id+"F0.wireOp",EDGE,"E7.62.6"),sQuery(id+"F0.wireOp",EDGE,"E7.63.0"),sQuery(id+"F0.wireOp",EDGE,"E7.63.1"),sQuery(id+"F0.wireOp",EDGE,"E7.63.2"),sQuery(id+"F0.wireOp",EDGE,"E7.63.3"),sQuery(id+"F0.wireOp",EDGE,"E7.63.4"),sQuery(id+"F0.wireOp",EDGE,"E7.63.5"),sQuery(id+"F0.wireOp",EDGE,"E7.63.6"),sQuery(id+"F0.wireOp",EDGE,"E7.64.0"),sQuery(id+"F0.wireOp",EDGE,"E7.64.1"),sQuery(id+"F0.wireOp",EDGE,"E7.64.2"),sQuery(id+"F0.wireOp",EDGE,"E7.64.3"),sQuery(id+"F0.wireOp",EDGE,"E7.64.4"),sQuery(id+"F0.wireOp",EDGE,"E7.64.5"),sQuery(id+"F0.wireOp",EDGE,"E7.64.6"),sQuery(id+"F0.wireOp",EDGE,"E7.65.0"),sQuery(id+"F0.wireOp",EDGE,"E7.65.1"),sQuery(id+"F0.wireOp",EDGE,"E7.65.2"),sQuery(id+"F0.wireOp",EDGE,"E7.65.3"),sQuery(id+"F0.wireOp",EDGE,"E7.65.4"),sQuery(id+"F0.wireOp",EDGE,"E7.65.5"),sQuery(id+"F0.wireOp",EDGE,"E7.65.6"),sQuery(id+"F0.wireOp",EDGE,"E7.66.0"),sQuery(id+"F0.wireOp",EDGE,"E7.66.1"),sQuery(id+"F0.wireOp",EDGE,"E7.66.2"),sQuery(id+"F0.wireOp",EDGE,"E7.66.3"),sQuery(id+"F0.wireOp",EDGE,"E7.66.4"),sQuery(id+"F0.wireOp",EDGE,"E7.66.5"),sQuery(id+"F0.wireOp",EDGE,"E7.66.6"),sQuery(id+"F0.wireOp",EDGE,"E7.67.0"),sQuery(id+"F0.wireOp",EDGE,"E7.67.1"),sQuery(id+"F0.wireOp",EDGE,"E7.67.2"),sQuery(id+"F0.wireOp",EDGE,"E7.67.3"),sQuery(id+"F0.wireOp",EDGE,"E7.67.4"),sQuery(id+"F0.wireOp",EDGE,"E7.67.5"),sQuery(id+"F0.wireOp",EDGE,"E7.67.6"),sQuery(id+"F0.wireOp",EDGE,"E7.68.0"),sQuery(id+"F0.wireOp",EDGE,"E7.68.1"),sQuery(id+"F0.wireOp",EDGE,"E7.68.2"),sQuery(id+"F0.wireOp",EDGE,"E7.68.3"),sQuery(id+"F0.wireOp",EDGE,"E7.68.4"),sQuery(id+"F0.wireOp",EDGE,"E7.68.5"),sQuery(id+"F0.wireOp",EDGE,"E7.68.6"),sQuery(id+"F0.wireOp",EDGE,"E7.69.0"),sQuery(id+"F0.wireOp",EDGE,"E7.69.1"),sQuery(id+"F0.wireOp",EDGE,"E7.69.2"),sQuery(id+"F0.wireOp",EDGE,"E7.69.3"),sQuery(id+"F0.wireOp",EDGE,"E7.69.4"),sQuery(id+"F0.wireOp",EDGE,"E7.69.5"),sQuery(id+"F0.wireOp",EDGE,"E7.69.6"),sQuery(id+"F0.wireOp",EDGE,"E7.70.0"),sQuery(id+"F0.wireOp",EDGE,"E7.70.1"),sQuery(id+"F0.wireOp",EDGE,"E7.70.2"),sQuery(id+"F0.wireOp",EDGE,"E7.70.3"),sQuery(id+"F0.wireOp",EDGE,"E7.70.4"),sQuery(id+"F0.wireOp",EDGE,"E7.70.5"),sQuery(id+"F0.wireOp",EDGE,"E7.70.6"),sQuery(id+"F0.wireOp",EDGE,"E7.71.0"),sQuery(id+"F0.wireOp",EDGE,"E7.71.1"),sQuery(id+"F0.wireOp",EDGE,"E7.71.2"),sQuery(id+"F0.wireOp",EDGE,"E7.71.3"),sQuery(id+"F0.wireOp",EDGE,"E7.71.4"),sQuery(id+"F0.wireOp",EDGE,"E7.71.5"),sQuery(id+"F0.wireOp",EDGE,"E7.71.6"),sQuery(id+"F0.wireOp",EDGE,"E7.72.0"),sQuery(id+"F0.wireOp",EDGE,"E7.72.1"),sQuery(id+"F0.wireOp",EDGE,"E7.72.2"),sQuery(id+"F0.wireOp",EDGE,"E7.72.3"),sQuery(id+"F0.wireOp",EDGE,"E7.72.4"),sQuery(id+"F0.wireOp",EDGE,"E7.72.5"),sQuery(id+"F0.wireOp",EDGE,"E7.72.6"),sQuery(id+"F0.wireOp",EDGE,"E7.73.0"),sQuery(id+"F0.wireOp",EDGE,"E7.73.1"),sQuery(id+"F0.wireOp",EDGE,"E7.73.2"),sQuery(id+"F0.wireOp",EDGE,"E7.73.3"),sQuery(id+"F0.wireOp",EDGE,"E7.73.4"),sQuery(id+"F0.wireOp",EDGE,"E7.73.5"),sQuery(id+"F0.wireOp",EDGE,"E7.73.6"),sQuery(id+"F0.wireOp",EDGE,"E7.74.0"),sQuery(id+"F0.wireOp",EDGE,"E7.74.1"),sQuery(id+"F0.wireOp",EDGE,"E7.74.2"),sQuery(id+"F0.wireOp",EDGE,"E7.74.3"),sQuery(id+"F0.wireOp",EDGE,"E7.74.4"),sQuery(id+"F0.wireOp",EDGE,"E7.74.5"),sQuery(id+"F0.wireOp",EDGE,"E7.74.6"),sQuery(id+"F0.wireOp",EDGE,"E7.75.0"),sQuery(id+"F0.wireOp",EDGE,"E7.75.1"),sQuery(id+"F0.wireOp",EDGE,"E7.75.2"),sQuery(id+"F0.wireOp",EDGE,"E7.75.3"),sQuery(id+"F0.wireOp",EDGE,"E7.75.4"),sQuery(id+"F0.wireOp",EDGE,"E7.75.5"),sQuery(id+"F0.wireOp",EDGE,"E7.75.6"),sQuery(id+"F0.wireOp",EDGE,"E7.76.0"),sQuery(id+"F0.wireOp",EDGE,"E7.76.1"),sQuery(id+"F0.wireOp",EDGE,"E7.76.2"),sQuery(id+"F0.wireOp",EDGE,"E7.76.3"),sQuery(id+"F0.wireOp",EDGE,"E7.76.4"),sQuery(id+"F0.wireOp",EDGE,"E7.76.5"),sQuery(id+"F0.wireOp",EDGE,"E7.76.6"),sQuery(id+"F0.wireOp",EDGE,"E7.77.0"),sQuery(id+"F0.wireOp",EDGE,"E7.77.1"),sQuery(id+"F0.wireOp",EDGE,"E7.77.2"),sQuery(id+"F0.wireOp",EDGE,"E7.77.3"),sQuery(id+"F0.wireOp",EDGE,"E7.77.4"),sQuery(id+"F0.wireOp",EDGE,"E7.77.5"),sQuery(id+"F0.wireOp",EDGE,"E7.77.6"),sQuery(id+"F0.wireOp",EDGE,"E7.78.0"),sQuery(id+"F0.wireOp",EDGE,"E7.78.1"),sQuery(id+"F0.wireOp",EDGE,"E7.78.2"),sQuery(id+"F0.wireOp",EDGE,"E7.78.3"),sQuery(id+"F0.wireOp",EDGE,"E7.78.4"),sQuery(id+"F0.wireOp",EDGE,"E7.78.5"),sQuery(id+"F0.wireOp",EDGE,"E7.78.6"),sQuery(id+"F0.wireOp",EDGE,"E7.79.0"),sQuery(id+"F0.wireOp",EDGE,"E7.79.1"),sQuery(id+"F0.wireOp",EDGE,"E7.79.2"),sQuery(id+"F0.wireOp",EDGE,"E7.79.3"),sQuery(id+"F0.wireOp",EDGE,"E7.79.4"),sQuery(id+"F0.wireOp",EDGE,"E7.79.5"),sQuery(id+"F0.wireOp",EDGE,"E7.79.6"),sQuery(id+"F0.wireOp",EDGE,"E7.80.0"),sQuery(id+"F0.wireOp",EDGE,"E7.80.1"),sQuery(id+"F0.wireOp",EDGE,"E7.80.2"),sQuery(id+"F0.wireOp",EDGE,"E7.80.3"),sQuery(id+"F0.wireOp",EDGE,"E7.80.4"),sQuery(id+"F0.wireOp",EDGE,"E7.80.5"),sQuery(id+"F0.wireOp",EDGE,"E7.80.6"),sQuery(id+"F0.wireOp",EDGE,"E7.81.0"),sQuery(id+"F0.wireOp",EDGE,"E7.81.1"),sQuery(id+"F0.wireOp",EDGE,"E7.81.2"),sQuery(id+"F0.wireOp",EDGE,"E7.81.3"),sQuery(id+"F0.wireOp",EDGE,"E7.81.4"),sQuery(id+"F0.wireOp",EDGE,"E7.81.5"),sQuery(id+"F0.wireOp",EDGE,"E7.81.6"),sQuery(id+"F0.wireOp",EDGE,"E7.82.0"),sQuery(id+"F0.wireOp",EDGE,"E7.82.1"),sQuery(id+"F0.wireOp",EDGE,"E7.82.2"),sQuery(id+"F0.wireOp",EDGE,"E7.82.3"),sQuery(id+"F0.wireOp",EDGE,"E7.82.4"),sQuery(id+"F0.wireOp",EDGE,"E7.82.5"),sQuery(id+"F0.wireOp",EDGE,"E7.82.6"),sQuery(id+"F0.wireOp",EDGE,"E7.83.0"),sQuery(id+"F0.wireOp",EDGE,"E7.83.1"),sQuery(id+"F0.wireOp",EDGE,"E7.83.2"),sQuery(id+"F0.wireOp",EDGE,"E7.83.3"),sQuery(id+"F0.wireOp",EDGE,"E7.83.4"),sQuery(id+"F0.wireOp",EDGE,"E7.83.5"),sQuery(id+"F0.wireOp",EDGE,"E7.83.6"),sQuery(id+"F0.wireOp",EDGE,"E7.84.0"),sQuery(id+"F0.wireOp",EDGE,"E7.84.1"),sQuery(id+"F0.wireOp",EDGE,"E7.84.2"),sQuery(id+"F0.wireOp",EDGE,"E7.84.3"),sQuery(id+"F0.wireOp",EDGE,"E7.84.4"),sQuery(id+"F0.wireOp",EDGE,"E7.84.5"),sQuery(id+"F0.wireOp",EDGE,"E7.84.6"),sQuery(id+"F0.wireOp",EDGE,"E7.85.0"),sQuery(id+"F0.wireOp",EDGE,"E7.85.1"),sQuery(id+"F0.wireOp",EDGE,"E7.85.2"),sQuery(id+"F0.wireOp",EDGE,"E7.85.3"),sQuery(id+"F0.wireOp",EDGE,"E7.85.4"),sQuery(id+"F0.wireOp",EDGE,"E7.85.5"),sQuery(id+"F0.wireOp",EDGE,"E7.85.6"),sQuery(id+"F0.wireOp",EDGE,"E7.86.0"),sQuery(id+"F0.wireOp",EDGE,"E7.86.1"),sQuery(id+"F0.wireOp",EDGE,"E7.86.2"),sQuery(id+"F0.wireOp",EDGE,"E7.86.3"),sQuery(id+"F0.wireOp",EDGE,"E7.86.4"),sQuery(id+"F0.wireOp",EDGE,"E7.86.5"),sQuery(id+"F0.wireOp",EDGE,"E7.86.6"),sQuery(id+"F0.wireOp",EDGE,"E7.87.0"),sQuery(id+"F0.wireOp",EDGE,"E7.87.1"),sQuery(id+"F0.wireOp",EDGE,"E7.87.2"),sQuery(id+"F0.wireOp",EDGE,"E7.87.3"),sQuery(id+"F0.wireOp",EDGE,"E7.87.4"),sQuery(id+"F0.wireOp",EDGE,"E7.87.5"),sQuery(id+"F0.wireOp",EDGE,"E7.87.6"),sQuery(id+"F0.wireOp",EDGE,"E7.88.0"),sQuery(id+"F0.wireOp",EDGE,"E7.88.1"),sQuery(id+"F0.wireOp",EDGE,"E7.88.2"),sQuery(id+"F0.wireOp",EDGE,"E7.88.3"),sQuery(id+"F0.wireOp",EDGE,"E7.88.4"),sQuery(id+"F0.wireOp",EDGE,"E7.88.5"),sQuery(id+"F0.wireOp",EDGE,"E7.88.6"),sQuery(id+"F0.wireOp",EDGE,"E7.89.0"),sQuery(id+"F0.wireOp",EDGE,"E7.89.1"),sQuery(id+"F0.wireOp",EDGE,"E7.89.2"),sQuery(id+"F0.wireOp",EDGE,"E7.89.3"),sQuery(id+"F0.wireOp",EDGE,"E7.89.4"),sQuery(id+"F0.wireOp",EDGE,"E7.89.5"),sQuery(id+"F0.wireOp",EDGE,"E7.89.6"),sQuery(id+"F0.wireOp",EDGE,"E7.90.0"),sQuery(id+"F0.wireOp",EDGE,"E7.90.1"),sQuery(id+"F0.wireOp",EDGE,"E7.90.2"),sQuery(id+"F0.wireOp",EDGE,"E7.90.3"),sQuery(id+"F0.wireOp",EDGE,"E7.90.4"),sQuery(id+"F0.wireOp",EDGE,"E7.90.5"),sQuery(id+"F0.wireOp",EDGE,"E7.90.6"),sQuery(id+"F0.wireOp",EDGE,"E7.91.0"),sQuery(id+"F0.wireOp",EDGE,"E7.91.1"),sQuery(id+"F0.wireOp",EDGE,"E7.91.2"),sQuery(id+"F0.wireOp",EDGE,"E7.91.3"),sQuery(id+"F0.wireOp",EDGE,"E7.91.4"),sQuery(id+"F0.wireOp",EDGE,"E7.91.5"),sQuery(id+"F0.wireOp",EDGE,"E7.91.6"),sQuery(id+"F0.wireOp",EDGE,"E7.92.0"),sQuery(id+"F0.wireOp",EDGE,"E7.92.1"),sQuery(id+"F0.wireOp",EDGE,"E7.92.2"),sQuery(id+"F0.wireOp",EDGE,"E7.92.3"),sQuery(id+"F0.wireOp",EDGE,"E7.92.4"),sQuery(id+"F0.wireOp",EDGE,"E7.92.5"),sQuery(id+"F0.wireOp",EDGE,"E7.92.6"),sQuery(id+"F0.wireOp",EDGE,"E7.93.0"),sQuery(id+"F0.wireOp",EDGE,"E7.93.1"),sQuery(id+"F0.wireOp",EDGE,"E7.93.2"),sQuery(id+"F0.wireOp",EDGE,"E7.93.3"),sQuery(id+"F0.wireOp",EDGE,"E7.93.4"),sQuery(id+"F0.wireOp",EDGE,"E7.93.5"),sQuery(id+"F0.wireOp",EDGE,"E7.93.6"),sQuery(id+"F0.wireOp",EDGE,"E7.94.0"),sQuery(id+"F0.wireOp",EDGE,"E7.94.1"),sQuery(id+"F0.wireOp",EDGE,"E7.94.2"),sQuery(id+"F0.wireOp",EDGE,"E7.94.3"),sQuery(id+"F0.wireOp",EDGE,"E7.94.4"),sQuery(id+"F0.wireOp",EDGE,"E7.94.5"),sQuery(id+"F0.wireOp",EDGE,"E7.94.6"),sQuery(id+"F0.wireOp",EDGE,"E7.95.0"),sQuery(id+"F0.wireOp",EDGE,"E7.95.1"),sQuery(id+"F0.wireOp",EDGE,"E7.95.2"),sQuery(id+"F0.wireOp",EDGE,"E7.95.3"),sQuery(id+"F0.wireOp",EDGE,"E7.95.4"),sQuery(id+"F0.wireOp",EDGE,"E7.95.5"),sQuery(id+"F0.wireOp",EDGE,"E7.95.6")])],"isStart":true});
            var sketch = newSketch(context, id + "F4", { "sketchPlane" : qUnion([Q0])});
            skCircle(sketch, "E9.cCircle", {"center": v(0, 0) * mm, "radius": 6.1 * mm, "construction": true});
            skLineSegment(sketch, "E9.0", {"start": v(0.48, -7.02) * mm, "end": v(-5.84, -3.93) * mm});
            skLineSegment(sketch, "E9.1", {"start": v(-5.84, -3.93) * mm, "end": v(-6.32, 3.1) * mm});
            skLineSegment(sketch, "E9.2", {"start": v(-6.32, 3.1) * mm, "end": v(-0.48, 7.02) * mm});
            skLineSegment(sketch, "E9.3", {"start": v(-0.48, 7.02) * mm, "end": v(5.84, 3.93) * mm});
            skLineSegment(sketch, "E9.4", {"start": v(5.84, 3.93) * mm, "end": v(6.32, -3.1) * mm});
            skLineSegment(sketch, "E9.5", {"start": v(6.32, -3.1) * mm, "end": v(0.48, -7.02) * mm});
            skPoint(sketch, "E9.0.midPoint", {"position": v(-2.68, -5.48) * mm});
            skCircle(sketch, "E10", {"center": v(0, -0.02) * mm, "radius": 0.9 * mm});
            skSolve(sketch);
        }
        {
            var Q0;
            Q0 = qSketchRegion(id + "F4", true);
            extrude(context, id + "F5", {"entities" : qUnion([Q0]), "operationType" : NewBodyOperationType.ADD, "depth" : 19.05 * mm, "offsetDistance" : 25.4 * mm});
        }
        {
            var Q0;
            {var subQ0=sQuery(id+"F0.wireOp",EDGE,"E7.67.4");var subQ1=sQuery(id+"F0.wireOp",EDGE,"E7.67.3");var subQ2=sQuery(id+"F0.wireOp",EDGE,"E7.67.2");var subQ3=sQuery(id+"F0.wireOp",EDGE,"E7.67.1");var subQ4=sQuery(id+"F0.wireOp",EDGE,"E7.68.6");var subQ5=sQuery(id+"F0.wireOp",EDGE,"E7.67.0");var subQ6=sQuery(id+"F0.wireOp",EDGE,"E7.66.5");var subQ7=sQuery(id+"F0.wireOp",EDGE,"E7.66.4");var subQ8=sQuery(id+"F0.wireOp",EDGE,"E7.66.3");var subQ9=sQuery(id+"F0.wireOp",EDGE,"E7.66.2");var subQ10=sQuery(id+"F0.wireOp",EDGE,"E7.66.1");var subQ11=sQuery(id+"F0.wireOp",EDGE,"E7.67.6");var subQ12=sQuery(id+"F0.wireOp",EDGE,"E7.66.0");var subQ13=sQuery(id+"F0.wireOp",EDGE,"E7.65.5");var subQ14=sQuery(id+"F0.wireOp",EDGE,"E7.65.4");var subQ15=sQuery(id+"F0.wireOp",EDGE,"E7.65.3");var subQ16=sQuery(id+"F0.wireOp",EDGE,"E7.65.2");var subQ17=sQuery(id+"F0.wireOp",EDGE,"E7.65.1");var subQ18=sQuery(id+"F0.wireOp",EDGE,"E7.66.6");var subQ19=sQuery(id+"F0.wireOp",EDGE,"E7.65.0");var subQ20=sQuery(id+"F0.wireOp",EDGE,"E7.64.5");var subQ21=sQuery(id+"F0.wireOp",EDGE,"E7.64.4");var subQ22=sQuery(id+"F0.wireOp",EDGE,"E7.64.3");var subQ23=sQuery(id+"F0.wireOp",EDGE,"E7.64.2");var subQ24=sQuery(id+"F0.wireOp",EDGE,"E7.64.1");var subQ25=sQuery(id+"F0.wireOp",EDGE,"E7.65.6");var subQ26=sQuery(id+"F0.wireOp",EDGE,"E7.64.0");var subQ27=sQuery(id+"F0.wireOp",EDGE,"E7.63.5");var subQ28=sQuery(id+"F0.wireOp",EDGE,"E7.63.4");var subQ29=sQuery(id+"F0.wireOp",EDGE,"E7.63.3");var subQ30=sQuery(id+"F0.wireOp",EDGE,"E7.63.2");var subQ31=sQuery(id+"F0.wireOp",EDGE,"E7.63.1");var subQ32=sQuery(id+"F0.wireOp",EDGE,"E7.64.6");var subQ33=sQuery(id+"F0.wireOp",EDGE,"E7.63.0");var subQ34=sQuery(id+"F0.wireOp",EDGE,"E7.62.5");var subQ35=sQuery(id+"F0.wireOp",EDGE,"E7.62.4");var subQ36=sQuery(id+"F0.wireOp",EDGE,"E7.62.3");var subQ37=sQuery(id+"F0.wireOp",EDGE,"E7.62.2");var subQ38=sQuery(id+"F0.wireOp",EDGE,"E7.62.1");var subQ39=sQuery(id+"F0.wireOp",EDGE,"E7.63.6");var subQ40=sQuery(id+"F0.wireOp",EDGE,"E7.62.0");var subQ41=sQuery(id+"F0.wireOp",EDGE,"E7.61.5");var subQ42=sQuery(id+"F0.wireOp",EDGE,"E7.61.4");var subQ43=sQuery(id+"F0.wireOp",EDGE,"E7.61.3");var subQ44=sQuery(id+"F0.wireOp",EDGE,"E7.61.2");var subQ45=sQuery(id+"F0.wireOp",EDGE,"E7.61.1");var subQ46=sQuery(id+"F0.wireOp",EDGE,"E7.62.6");var subQ47=sQuery(id+"F0.wireOp",EDGE,"E7.61.0");var subQ48=sQuery(id+"F0.wireOp",EDGE,"E7.60.5");var subQ49=sQuery(id+"F0.wireOp",EDGE,"E7.60.4");var subQ50=sQuery(id+"F0.wireOp",EDGE,"E7.60.3");var subQ51=sQuery(id+"F0.wireOp",EDGE,"E7.60.2");var subQ52=sQuery(id+"F0.wireOp",EDGE,"E7.60.1");var subQ53=sQuery(id+"F0.wireOp",EDGE,"E7.61.6");var subQ54=sQuery(id+"F0.wireOp",EDGE,"E7.60.0");var subQ55=sQuery(id+"F0.wireOp",EDGE,"E7.59.5");var subQ56=sQuery(id+"F0.wireOp",EDGE,"E7.59.4");var subQ57=sQuery(id+"F0.wireOp",EDGE,"E7.59.3");var subQ58=sQuery(id+"F0.wireOp",EDGE,"E7.59.2");var subQ59=sQuery(id+"F0.wireOp",EDGE,"E7.59.1");var subQ60=sQuery(id+"F0.wireOp",EDGE,"E7.60.6");var subQ61=sQuery(id+"F0.wireOp",EDGE,"E7.59.0");var subQ62=sQuery(id+"F0.wireOp",EDGE,"E7.58.5");var subQ63=sQuery(id+"F0.wireOp",EDGE,"E7.58.4");var subQ64=sQuery(id+"F0.wireOp",EDGE,"E7.58.3");var subQ65=sQuery(id+"F0.wireOp",EDGE,"E7.58.2");var subQ66=sQuery(id+"F0.wireOp",EDGE,"E7.58.1");var subQ67=sQuery(id+"F0.wireOp",EDGE,"E7.59.6");var subQ68=sQuery(id+"F0.wireOp",EDGE,"E7.58.0");var subQ69=sQuery(id+"F0.wireOp",EDGE,"E7.57.5");var subQ70=sQuery(id+"F0.wireOp",EDGE,"E7.57.4");var subQ71=sQuery(id+"F0.wireOp",EDGE,"E7.57.3");var subQ72=sQuery(id+"F0.wireOp",EDGE,"E7.57.2");var subQ73=sQuery(id+"F0.wireOp",EDGE,"E7.57.1");var subQ74=sQuery(id+"F0.wireOp",EDGE,"E7.58.6");var subQ75=sQuery(id+"F0.wireOp",EDGE,"E7.57.0");var subQ76=sQuery(id+"F0.wireOp",EDGE,"E7.56.5");var subQ77=sQuery(id+"F0.wireOp",EDGE,"E7.56.4");var subQ78=sQuery(id+"F0.wireOp",EDGE,"E7.56.3");var subQ79=sQuery(id+"F0.wireOp",EDGE,"E7.56.2");var subQ80=sQuery(id+"F0.wireOp",EDGE,"E7.56.1");var subQ81=sQuery(id+"F0.wireOp",EDGE,"E7.57.6");var subQ82=sQuery(id+"F0.wireOp",EDGE,"E7.56.0");var subQ83=sQuery(id+"F0.wireOp",EDGE,"E7.55.5");var subQ84=sQuery(id+"F0.wireOp",EDGE,"E7.55.4");var subQ85=sQuery(id+"F0.wireOp",EDGE,"E7.55.3");var subQ86=sQuery(id+"F0.wireOp",EDGE,"E7.55.2");var subQ87=sQuery(id+"F0.wireOp",EDGE,"E7.55.1");var subQ88=sQuery(id+"F0.wireOp",EDGE,"E7.56.6");var subQ89=sQuery(id+"F0.wireOp",EDGE,"E7.55.0");var subQ90=sQuery(id+"F0.wireOp",EDGE,"E7.54.5");var subQ91=sQuery(id+"F0.wireOp",EDGE,"E7.54.4");var subQ92=sQuery(id+"F0.wireOp",EDGE,"E7.54.3");var subQ93=sQuery(id+"F0.wireOp",EDGE,"E7.54.2");var subQ94=sQuery(id+"F0.wireOp",EDGE,"E7.54.1");var subQ95=sQuery(id+"F0.wireOp",EDGE,"E7.55.6");var subQ96=sQuery(id+"F0.wireOp",EDGE,"E7.54.0");var subQ97=sQuery(id+"F0.wireOp",EDGE,"E7.53.5");var subQ98=sQuery(id+"F0.wireOp",EDGE,"E7.53.4");var subQ99=sQuery(id+"F0.wireOp",EDGE,"E7.53.3");var subQ100=sQuery(id+"F0.wireOp",EDGE,"E7.53.2");var subQ101=sQuery(id+"F0.wireOp",EDGE,"E7.53.1");var subQ102=sQuery(id+"F0.wireOp",EDGE,"E7.54.6");var subQ103=sQuery(id+"F0.wireOp",EDGE,"E7.53.0");var subQ104=sQuery(id+"F0.wireOp",EDGE,"E7.52.5");var subQ105=sQuery(id+"F0.wireOp",EDGE,"E7.52.4");var subQ106=sQuery(id+"F0.wireOp",EDGE,"E7.52.3");var subQ107=sQuery(id+"F0.wireOp",EDGE,"E7.52.2");var subQ108=sQuery(id+"F0.wireOp",EDGE,"E7.52.1");var subQ109=sQuery(id+"F0.wireOp",EDGE,"E7.53.6");var subQ110=sQuery(id+"F0.wireOp",EDGE,"E7.52.0");var subQ111=sQuery(id+"F0.wireOp",EDGE,"E7.51.5");var subQ112=sQuery(id+"F0.wireOp",EDGE,"E7.51.4");var subQ113=sQuery(id+"F0.wireOp",EDGE,"E7.51.3");var subQ114=sQuery(id+"F0.wireOp",EDGE,"E7.51.2");var subQ115=sQuery(id+"F0.wireOp",EDGE,"E7.51.1");var subQ116=sQuery(id+"F0.wireOp",EDGE,"E7.52.6");var subQ117=sQuery(id+"F0.wireOp",EDGE,"E7.51.0");var subQ118=sQuery(id+"F0.wireOp",EDGE,"E7.50.5");var subQ119=sQuery(id+"F0.wireOp",EDGE,"E7.50.4");var subQ120=sQuery(id+"F0.wireOp",EDGE,"E7.50.3");var subQ121=sQuery(id+"F0.wireOp",EDGE,"E7.50.2");var subQ122=sQuery(id+"F0.wireOp",EDGE,"E7.50.1");var subQ123=sQuery(id+"F0.wireOp",EDGE,"E7.51.6");var subQ124=sQuery(id+"F0.wireOp",EDGE,"E7.50.0");var subQ125=sQuery(id+"F0.wireOp",EDGE,"E7.49.5");var subQ126=sQuery(id+"F0.wireOp",EDGE,"E7.49.4");var subQ127=sQuery(id+"F0.wireOp",EDGE,"E7.49.3");var subQ128=sQuery(id+"F0.wireOp",EDGE,"E7.49.2");var subQ129=sQuery(id+"F0.wireOp",EDGE,"E7.49.1");var subQ130=sQuery(id+"F0.wireOp",EDGE,"E7.50.6");var subQ131=sQuery(id+"F0.wireOp",EDGE,"E7.49.0");var subQ132=sQuery(id+"F0.wireOp",EDGE,"E7.48.5");var subQ133=sQuery(id+"F0.wireOp",EDGE,"E7.48.4");var subQ134=sQuery(id+"F0.wireOp",EDGE,"E7.48.3");var subQ135=sQuery(id+"F0.wireOp",EDGE,"E7.48.2");var subQ136=sQuery(id+"F0.wireOp",EDGE,"E7.48.1");var subQ137=sQuery(id+"F0.wireOp",EDGE,"E7.49.6");var subQ138=sQuery(id+"F0.wireOp",EDGE,"E7.48.0");var subQ139=sQuery(id+"F0.wireOp",EDGE,"E7.47.5");var subQ140=sQuery(id+"F0.wireOp",EDGE,"E7.47.4");var subQ141=sQuery(id+"F0.wireOp",EDGE,"E7.47.3");var subQ142=sQuery(id+"F0.wireOp",EDGE,"E7.47.2");var subQ143=sQuery(id+"F0.wireOp",EDGE,"E7.47.1");var subQ144=sQuery(id+"F0.wireOp",EDGE,"E7.48.6");var subQ145=sQuery(id+"F0.wireOp",EDGE,"E7.47.0");var subQ146=sQuery(id+"F0.wireOp",EDGE,"E7.46.5");var subQ147=sQuery(id+"F0.wireOp",EDGE,"E7.46.4");var subQ148=sQuery(id+"F0.wireOp",EDGE,"E7.46.3");var subQ149=sQuery(id+"F0.wireOp",EDGE,"E7.46.2");var subQ150=sQuery(id+"F0.wireOp",EDGE,"E7.46.1");var subQ151=sQuery(id+"F0.wireOp",EDGE,"E7.47.6");var subQ152=sQuery(id+"F0.wireOp",EDGE,"E7.46.0");var subQ153=sQuery(id+"F0.wireOp",EDGE,"E7.45.5");var subQ154=sQuery(id+"F0.wireOp",EDGE,"E7.45.4");var subQ155=sQuery(id+"F0.wireOp",EDGE,"E7.45.3");var subQ156=sQuery(id+"F0.wireOp",EDGE,"E7.45.2");var subQ157=sQuery(id+"F0.wireOp",EDGE,"E7.45.1");var subQ158=sQuery(id+"F0.wireOp",EDGE,"E7.46.6");var subQ159=sQuery(id+"F0.wireOp",EDGE,"E7.45.0");var subQ160=sQuery(id+"F0.wireOp",EDGE,"E7.44.5");var subQ161=sQuery(id+"F0.wireOp",EDGE,"E7.44.4");var subQ162=sQuery(id+"F0.wireOp",EDGE,"E7.44.3");var subQ163=sQuery(id+"F0.wireOp",EDGE,"E7.44.2");var subQ164=sQuery(id+"F0.wireOp",EDGE,"E7.44.1");var subQ165=sQuery(id+"F0.wireOp",EDGE,"E7.45.6");var subQ166=sQuery(id+"F0.wireOp",EDGE,"E7.44.0");var subQ167=sQuery(id+"F0.wireOp",EDGE,"E7.43.5");var subQ168=sQuery(id+"F0.wireOp",EDGE,"E7.43.4");var subQ169=sQuery(id+"F0.wireOp",EDGE,"E7.43.3");var subQ170=sQuery(id+"F0.wireOp",EDGE,"E7.43.2");var subQ171=sQuery(id+"F0.wireOp",EDGE,"E7.43.1");var subQ172=sQuery(id+"F0.wireOp",EDGE,"E7.44.6");var subQ173=sQuery(id+"F0.wireOp",EDGE,"E7.43.0");var subQ174=sQuery(id+"F0.wireOp",EDGE,"E7.42.5");var subQ175=sQuery(id+"F0.wireOp",EDGE,"E7.42.4");var subQ176=sQuery(id+"F0.wireOp",EDGE,"E7.42.3");var subQ177=sQuery(id+"F0.wireOp",EDGE,"E7.42.2");var subQ178=sQuery(id+"F0.wireOp",EDGE,"E7.42.1");var subQ179=sQuery(id+"F0.wireOp",EDGE,"E7.43.6");var subQ180=sQuery(id+"F0.wireOp",EDGE,"E7.42.0");var subQ181=sQuery(id+"F0.wireOp",EDGE,"E7.41.5");var subQ182=sQuery(id+"F0.wireOp",EDGE,"E7.41.4");var subQ183=sQuery(id+"F0.wireOp",EDGE,"E7.41.3");var subQ184=sQuery(id+"F0.wireOp",EDGE,"E7.41.2");var subQ185=sQuery(id+"F0.wireOp",EDGE,"E7.41.1");var subQ186=sQuery(id+"F0.wireOp",EDGE,"E7.42.6");var subQ187=sQuery(id+"F0.wireOp",EDGE,"E7.41.0");var subQ188=sQuery(id+"F0.wireOp",EDGE,"E7.40.5");var subQ189=sQuery(id+"F0.wireOp",EDGE,"E7.40.4");var subQ190=sQuery(id+"F0.wireOp",EDGE,"E7.40.3");var subQ191=sQuery(id+"F0.wireOp",EDGE,"E7.40.2");var subQ192=sQuery(id+"F0.wireOp",EDGE,"E7.40.1");var subQ193=sQuery(id+"F0.wireOp",EDGE,"E7.41.6");var subQ194=sQuery(id+"F0.wireOp",EDGE,"E7.40.0");var subQ195=sQuery(id+"F0.wireOp",EDGE,"E7.39.5");var subQ196=sQuery(id+"F0.wireOp",EDGE,"E7.39.4");var subQ197=sQuery(id+"F0.wireOp",EDGE,"E7.39.3");var subQ198=sQuery(id+"F0.wireOp",EDGE,"E7.39.2");var subQ199=sQuery(id+"F0.wireOp",EDGE,"E7.39.1");var subQ200=sQuery(id+"F0.wireOp",EDGE,"E7.40.6");var subQ201=sQuery(id+"F0.wireOp",EDGE,"E7.39.0");var subQ202=sQuery(id+"F0.wireOp",EDGE,"E7.38.5");var subQ203=sQuery(id+"F0.wireOp",EDGE,"E7.38.4");var subQ204=sQuery(id+"F0.wireOp",EDGE,"E7.38.3");var subQ205=sQuery(id+"F0.wireOp",EDGE,"E7.38.2");var subQ206=sQuery(id+"F0.wireOp",EDGE,"E7.38.1");var subQ207=sQuery(id+"F0.wireOp",EDGE,"E7.39.6");var subQ208=sQuery(id+"F0.wireOp",EDGE,"E7.38.0");var subQ209=sQuery(id+"F0.wireOp",EDGE,"E7.37.5");var subQ210=sQuery(id+"F0.wireOp",EDGE,"E7.37.4");var subQ211=sQuery(id+"F0.wireOp",EDGE,"E7.37.3");var subQ212=sQuery(id+"F0.wireOp",EDGE,"E7.37.2");var subQ213=sQuery(id+"F0.wireOp",EDGE,"E7.37.1");var subQ214=sQuery(id+"F0.wireOp",EDGE,"E7.38.6");var subQ215=sQuery(id+"F0.wireOp",EDGE,"E7.37.0");var subQ216=sQuery(id+"F0.wireOp",EDGE,"E7.36.5");var subQ217=sQuery(id+"F0.wireOp",EDGE,"E7.36.4");var subQ218=sQuery(id+"F0.wireOp",EDGE,"E7.36.3");var subQ219=sQuery(id+"F0.wireOp",EDGE,"E7.36.2");var subQ220=sQuery(id+"F0.wireOp",EDGE,"E7.36.1");var subQ221=sQuery(id+"F0.wireOp",EDGE,"E7.37.6");var subQ222=sQuery(id+"F0.wireOp",EDGE,"E7.36.0");var subQ223=sQuery(id+"F0.wireOp",EDGE,"E7.35.5");var subQ224=sQuery(id+"F0.wireOp",EDGE,"E7.35.4");var subQ225=sQuery(id+"F0.wireOp",EDGE,"E7.35.3");var subQ226=sQuery(id+"F0.wireOp",EDGE,"E7.35.2");var subQ227=sQuery(id+"F0.wireOp",EDGE,"E7.35.1");var subQ228=sQuery(id+"F0.wireOp",EDGE,"E7.36.6");var subQ229=sQuery(id+"F0.wireOp",EDGE,"E7.35.0");var subQ230=sQuery(id+"F0.wireOp",EDGE,"E7.34.5");var subQ231=sQuery(id+"F0.wireOp",EDGE,"E7.34.4");var subQ232=sQuery(id+"F0.wireOp",EDGE,"E7.34.3");var subQ233=sQuery(id+"F0.wireOp",EDGE,"E7.34.2");var subQ234=sQuery(id+"F0.wireOp",EDGE,"E7.34.1");var subQ235=sQuery(id+"F0.wireOp",EDGE,"E7.35.6");var subQ236=sQuery(id+"F0.wireOp",EDGE,"E7.34.0");var subQ237=sQuery(id+"F0.wireOp",EDGE,"E7.33.5");var subQ238=sQuery(id+"F0.wireOp",EDGE,"E7.33.4");var subQ239=sQuery(id+"F0.wireOp",EDGE,"E7.33.3");var subQ240=sQuery(id+"F0.wireOp",EDGE,"E7.33.2");var subQ241=sQuery(id+"F0.wireOp",EDGE,"E7.33.1");var subQ242=sQuery(id+"F0.wireOp",EDGE,"E7.34.6");var subQ243=sQuery(id+"F0.wireOp",EDGE,"E7.33.0");var subQ244=sQuery(id+"F0.wireOp",EDGE,"E7.32.5");var subQ245=sQuery(id+"F0.wireOp",EDGE,"E7.15.4");var subQ246=sQuery(id+"F0.wireOp",EDGE,"E7.15.3");var subQ247=sQuery(id+"F0.wireOp",EDGE,"E7.15.2");var subQ248=sQuery(id+"F0.wireOp",EDGE,"E7.15.1");var subQ249=sQuery(id+"F0.wireOp",EDGE,"E7.16.6");var subQ250=sQuery(id+"F0.wireOp",EDGE,"E7.15.0");var subQ251=sQuery(id+"F0.wireOp",EDGE,"E7.14.5");var subQ252=sQuery(id+"F0.wireOp",EDGE,"E7.14.4");var subQ253=sQuery(id+"F0.wireOp",EDGE,"E7.14.3");var subQ254=sQuery(id+"F0.wireOp",EDGE,"E7.14.2");var subQ255=sQuery(id+"F0.wireOp",EDGE,"E7.14.1");var subQ256=sQuery(id+"F0.wireOp",EDGE,"E7.15.6");var subQ257=sQuery(id+"F0.wireOp",EDGE,"E7.14.0");var subQ258=sQuery(id+"F0.wireOp",EDGE,"E7.13.5");var subQ259=sQuery(id+"F0.wireOp",EDGE,"E7.13.4");var subQ260=sQuery(id+"F0.wireOp",EDGE,"E7.13.3");var subQ261=sQuery(id+"F0.wireOp",EDGE,"E7.13.2");var subQ262=sQuery(id+"F0.wireOp",EDGE,"E7.13.1");var subQ263=sQuery(id+"F0.wireOp",EDGE,"E7.14.6");var subQ264=sQuery(id+"F0.wireOp",EDGE,"E7.13.0");var subQ265=sQuery(id+"F0.wireOp",EDGE,"E7.12.5");var subQ266=sQuery(id+"F0.wireOp",EDGE,"E7.12.4");var subQ267=sQuery(id+"F0.wireOp",EDGE,"E7.12.3");var subQ268=sQuery(id+"F0.wireOp",EDGE,"E7.12.2");var subQ269=sQuery(id+"F0.wireOp",EDGE,"E7.12.1");var subQ270=sQuery(id+"F0.wireOp",EDGE,"E7.13.6");var subQ271=sQuery(id+"F0.wireOp",EDGE,"E7.12.0");var subQ272=sQuery(id+"F0.wireOp",EDGE,"E7.11.5");var subQ273=sQuery(id+"F0.wireOp",EDGE,"E7.11.4");var subQ274=sQuery(id+"F0.wireOp",EDGE,"E7.11.3");var subQ275=sQuery(id+"F0.wireOp",EDGE,"E7.11.2");var subQ276=sQuery(id+"F0.wireOp",EDGE,"E7.11.1");var subQ277=sQuery(id+"F0.wireOp",EDGE,"E7.12.6");var subQ278=sQuery(id+"F0.wireOp",EDGE,"E7.11.0");var subQ279=sQuery(id+"F0.wireOp",EDGE,"E7.10.5");var subQ280=sQuery(id+"F0.wireOp",EDGE,"E7.10.4");var subQ281=sQuery(id+"F0.wireOp",EDGE,"E7.10.3");var subQ282=sQuery(id+"F0.wireOp",EDGE,"E7.10.2");var subQ283=sQuery(id+"F0.wireOp",EDGE,"E7.10.1");var subQ284=sQuery(id+"F0.wireOp",EDGE,"E7.11.6");var subQ285=sQuery(id+"F0.wireOp",EDGE,"E7.10.0");var subQ286=sQuery(id+"F0.wireOp",EDGE,"E7.9.5");var subQ287=sQuery(id+"F0.wireOp",EDGE,"E7.9.4");var subQ288=sQuery(id+"F0.wireOp",EDGE,"E7.9.3");var subQ289=sQuery(id+"F0.wireOp",EDGE,"E7.9.2");var subQ290=sQuery(id+"F0.wireOp",EDGE,"E7.9.1");var subQ291=sQuery(id+"F0.wireOp",EDGE,"E7.10.6");var subQ292=sQuery(id+"F0.wireOp",EDGE,"E7.9.0");var subQ293=sQuery(id+"F0.wireOp",EDGE,"E7.8.5");var subQ294=sQuery(id+"F0.wireOp",EDGE,"E7.8.4");var subQ295=sQuery(id+"F0.wireOp",EDGE,"E7.8.3");var subQ296=sQuery(id+"F0.wireOp",EDGE,"E7.8.2");var subQ297=sQuery(id+"F0.wireOp",EDGE,"E7.8.1");var subQ298=sQuery(id+"F0.wireOp",EDGE,"E7.9.6");var subQ299=sQuery(id+"F0.wireOp",EDGE,"E7.8.0");var subQ300=sQuery(id+"F0.wireOp",EDGE,"E7.7.5");var subQ301=sQuery(id+"F0.wireOp",EDGE,"E7.7.4");var subQ302=sQuery(id+"F0.wireOp",EDGE,"E7.7.3");var subQ303=sQuery(id+"F0.wireOp",EDGE,"E7.3.2");var subQ304=sQuery(id+"F0.wireOp",EDGE,"E7.3.1");var subQ305=sQuery(id+"F0.wireOp",EDGE,"E7.4.6");var subQ306=sQuery(id+"F0.wireOp",EDGE,"E7.3.0");var subQ307=sQuery(id+"F0.wireOp",EDGE,"E7.2.5");var subQ308=sQuery(id+"F0.wireOp",EDGE,"E7.2.4");var subQ309=sQuery(id+"F0.wireOp",EDGE,"E7.2.3");var subQ310=sQuery(id+"F0.wireOp",EDGE,"E7.2.2");var subQ311=sQuery(id+"F0.wireOp",EDGE,"E7.2.1");var subQ312=sQuery(id+"F0.wireOp",EDGE,"E7.3.6");var subQ313=sQuery(id+"F0.wireOp",EDGE,"E7.2.0");var subQ314=sQuery(id+"F0.wireOp",EDGE,"E7.1.5");var subQ315=sQuery(id+"F0.wireOp",EDGE,"E7.1.4");var subQ316=sQuery(id+"F0.wireOp",EDGE,"E7.1.3");var subQ317=sQuery(id+"F0.wireOp",EDGE,"E3");var subQ318=sQuery(id+"F0.wireOp",EDGE,"E2");var subQ319=sQuery(id+"F0.wireOp",EDGE,"E7.95.0");var subQ320=sQuery(id+"F0.wireOp",EDGE,"E1");var subQ321=sQuery(id+"F0.wireOp",EDGE,"E7.1.6");var subQ322=sQuery(id+"F0.wireOp",EDGE,"E0");var subQ323=sQuery(id+"F0.wireOp",EDGE,"E4.trimOffspring");var subQ324=sQuery(id+"F0.wireOp",EDGE,"E5.filletArc");var subQ325=sQuery(id+"F0.wireOp",EDGE,"E6.filletArc");var subQ326=sQuery(id+"F0.wireOp",EDGE,"E7.2.6");var subQ327=sQuery(id+"F0.wireOp",EDGE,"E7.1.0");var subQ328=sQuery(id+"F0.wireOp",EDGE,"E7.1.1");var subQ329=sQuery(id+"F0.wireOp",EDGE,"E7.1.2");var subQ330=sQuery(id+"F0.wireOp",EDGE,"E7.3.3");var subQ331=sQuery(id+"F0.wireOp",EDGE,"E7.3.4");var subQ332=sQuery(id+"F0.wireOp",EDGE,"E7.3.5");var subQ333=sQuery(id+"F0.wireOp",EDGE,"E7.5.6");var subQ334=sQuery(id+"F0.wireOp",EDGE,"E7.4.0");var subQ335=sQuery(id+"F0.wireOp",EDGE,"E7.4.1");var subQ336=sQuery(id+"F0.wireOp",EDGE,"E7.4.2");var subQ337=sQuery(id+"F0.wireOp",EDGE,"E7.4.3");var subQ338=sQuery(id+"F0.wireOp",EDGE,"E7.4.4");var subQ339=sQuery(id+"F0.wireOp",EDGE,"E7.4.5");var subQ340=sQuery(id+"F0.wireOp",EDGE,"E7.6.6");var subQ341=sQuery(id+"F0.wireOp",EDGE,"E7.5.0");var subQ342=sQuery(id+"F0.wireOp",EDGE,"E7.5.1");var subQ343=sQuery(id+"F0.wireOp",EDGE,"E7.5.2");var subQ344=sQuery(id+"F0.wireOp",EDGE,"E7.5.3");var subQ345=sQuery(id+"F0.wireOp",EDGE,"E7.5.4");var subQ346=sQuery(id+"F0.wireOp",EDGE,"E7.5.5");var subQ347=sQuery(id+"F0.wireOp",EDGE,"E7.7.6");var subQ348=sQuery(id+"F0.wireOp",EDGE,"E7.6.0");var subQ349=sQuery(id+"F0.wireOp",EDGE,"E7.6.1");var subQ350=sQuery(id+"F0.wireOp",EDGE,"E7.6.2");var subQ351=sQuery(id+"F0.wireOp",EDGE,"E7.6.3");var subQ352=sQuery(id+"F0.wireOp",EDGE,"E7.6.4");var subQ353=sQuery(id+"F0.wireOp",EDGE,"E7.6.5");var subQ354=sQuery(id+"F0.wireOp",EDGE,"E7.8.6");var subQ355=sQuery(id+"F0.wireOp",EDGE,"E7.7.0");var subQ356=sQuery(id+"F0.wireOp",EDGE,"E7.7.1");var subQ357=sQuery(id+"F0.wireOp",EDGE,"E7.7.2");var subQ358=sQuery(id+"F0.wireOp",EDGE,"E7.15.5");var subQ359=sQuery(id+"F0.wireOp",EDGE,"E7.17.6");var subQ360=sQuery(id+"F0.wireOp",EDGE,"E7.16.0");var subQ361=sQuery(id+"F0.wireOp",EDGE,"E7.16.1");var subQ362=sQuery(id+"F0.wireOp",EDGE,"E7.16.2");var subQ363=sQuery(id+"F0.wireOp",EDGE,"E7.16.3");var subQ364=sQuery(id+"F0.wireOp",EDGE,"E7.16.4");var subQ365=sQuery(id+"F0.wireOp",EDGE,"E7.16.5");var subQ366=sQuery(id+"F0.wireOp",EDGE,"E7.18.6");var subQ367=sQuery(id+"F0.wireOp",EDGE,"E7.17.0");var subQ368=sQuery(id+"F0.wireOp",EDGE,"E7.17.1");var subQ369=sQuery(id+"F0.wireOp",EDGE,"E7.17.2");var subQ370=sQuery(id+"F0.wireOp",EDGE,"E7.17.3");var subQ371=sQuery(id+"F0.wireOp",EDGE,"E7.17.4");var subQ372=sQuery(id+"F0.wireOp",EDGE,"E7.17.5");var subQ373=sQuery(id+"F0.wireOp",EDGE,"E7.19.6");var subQ374=sQuery(id+"F0.wireOp",EDGE,"E7.18.0");var subQ375=sQuery(id+"F0.wireOp",EDGE,"E7.18.1");var subQ376=sQuery(id+"F0.wireOp",EDGE,"E7.18.2");var subQ377=sQuery(id+"F0.wireOp",EDGE,"E7.18.3");var subQ378=sQuery(id+"F0.wireOp",EDGE,"E7.18.4");var subQ379=sQuery(id+"F0.wireOp",EDGE,"E7.18.5");var subQ380=sQuery(id+"F0.wireOp",EDGE,"E7.20.6");var subQ381=sQuery(id+"F0.wireOp",EDGE,"E7.19.0");var subQ382=sQuery(id+"F0.wireOp",EDGE,"E7.19.1");var subQ383=sQuery(id+"F0.wireOp",EDGE,"E7.19.2");var subQ384=sQuery(id+"F0.wireOp",EDGE,"E7.19.3");var subQ385=sQuery(id+"F0.wireOp",EDGE,"E7.19.4");var subQ386=sQuery(id+"F0.wireOp",EDGE,"E7.19.5");var subQ387=sQuery(id+"F0.wireOp",EDGE,"E7.21.6");var subQ388=sQuery(id+"F0.wireOp",EDGE,"E7.20.0");var subQ389=sQuery(id+"F0.wireOp",EDGE,"E7.20.1");var subQ390=sQuery(id+"F0.wireOp",EDGE,"E7.20.2");var subQ391=sQuery(id+"F0.wireOp",EDGE,"E7.20.3");var subQ392=sQuery(id+"F0.wireOp",EDGE,"E7.20.4");var subQ393=sQuery(id+"F0.wireOp",EDGE,"E7.20.5");var subQ394=sQuery(id+"F0.wireOp",EDGE,"E7.22.6");var subQ395=sQuery(id+"F0.wireOp",EDGE,"E7.21.0");var subQ396=sQuery(id+"F0.wireOp",EDGE,"E7.21.1");var subQ397=sQuery(id+"F0.wireOp",EDGE,"E7.21.2");var subQ398=sQuery(id+"F0.wireOp",EDGE,"E7.21.3");var subQ399=sQuery(id+"F0.wireOp",EDGE,"E7.21.4");var subQ400=sQuery(id+"F0.wireOp",EDGE,"E7.21.5");var subQ401=sQuery(id+"F0.wireOp",EDGE,"E7.23.6");var subQ402=sQuery(id+"F0.wireOp",EDGE,"E7.22.0");var subQ403=sQuery(id+"F0.wireOp",EDGE,"E7.22.1");var subQ404=sQuery(id+"F0.wireOp",EDGE,"E7.22.2");var subQ405=sQuery(id+"F0.wireOp",EDGE,"E7.22.3");var subQ406=sQuery(id+"F0.wireOp",EDGE,"E7.22.4");var subQ407=sQuery(id+"F0.wireOp",EDGE,"E7.22.5");var subQ408=sQuery(id+"F0.wireOp",EDGE,"E7.24.6");var subQ409=sQuery(id+"F0.wireOp",EDGE,"E7.23.0");var subQ410=sQuery(id+"F0.wireOp",EDGE,"E7.23.1");var subQ411=sQuery(id+"F0.wireOp",EDGE,"E7.23.2");var subQ412=sQuery(id+"F0.wireOp",EDGE,"E7.23.3");var subQ413=sQuery(id+"F0.wireOp",EDGE,"E7.23.4");var subQ414=sQuery(id+"F0.wireOp",EDGE,"E7.23.5");var subQ415=sQuery(id+"F0.wireOp",EDGE,"E7.25.6");var subQ416=sQuery(id+"F0.wireOp",EDGE,"E7.24.0");var subQ417=sQuery(id+"F0.wireOp",EDGE,"E7.24.1");var subQ418=sQuery(id+"F0.wireOp",EDGE,"E7.24.2");var subQ419=sQuery(id+"F0.wireOp",EDGE,"E7.24.3");var subQ420=sQuery(id+"F0.wireOp",EDGE,"E7.24.4");var subQ421=sQuery(id+"F0.wireOp",EDGE,"E7.24.5");var subQ422=sQuery(id+"F0.wireOp",EDGE,"E7.26.6");var subQ423=sQuery(id+"F0.wireOp",EDGE,"E7.25.0");var subQ424=sQuery(id+"F0.wireOp",EDGE,"E7.25.1");var subQ425=sQuery(id+"F0.wireOp",EDGE,"E7.25.2");var subQ426=sQuery(id+"F0.wireOp",EDGE,"E7.25.3");var subQ427=sQuery(id+"F0.wireOp",EDGE,"E7.25.4");var subQ428=sQuery(id+"F0.wireOp",EDGE,"E7.25.5");var subQ429=sQuery(id+"F0.wireOp",EDGE,"E7.27.6");var subQ430=sQuery(id+"F0.wireOp",EDGE,"E7.26.0");var subQ431=sQuery(id+"F0.wireOp",EDGE,"E7.26.1");var subQ432=sQuery(id+"F0.wireOp",EDGE,"E7.26.2");var subQ433=sQuery(id+"F0.wireOp",EDGE,"E7.26.3");var subQ434=sQuery(id+"F0.wireOp",EDGE,"E7.26.4");var subQ435=sQuery(id+"F0.wireOp",EDGE,"E7.26.5");var subQ436=sQuery(id+"F0.wireOp",EDGE,"E7.28.6");var subQ437=sQuery(id+"F0.wireOp",EDGE,"E7.27.0");var subQ438=sQuery(id+"F0.wireOp",EDGE,"E7.27.1");var subQ439=sQuery(id+"F0.wireOp",EDGE,"E7.27.2");var subQ440=sQuery(id+"F0.wireOp",EDGE,"E7.27.3");var subQ441=sQuery(id+"F0.wireOp",EDGE,"E7.27.4");var subQ442=sQuery(id+"F0.wireOp",EDGE,"E7.27.5");var subQ443=sQuery(id+"F0.wireOp",EDGE,"E7.29.6");var subQ444=sQuery(id+"F0.wireOp",EDGE,"E7.28.0");var subQ445=sQuery(id+"F0.wireOp",EDGE,"E7.28.1");var subQ446=sQuery(id+"F0.wireOp",EDGE,"E7.28.2");var subQ447=sQuery(id+"F0.wireOp",EDGE,"E7.28.3");var subQ448=sQuery(id+"F0.wireOp",EDGE,"E7.28.4");var subQ449=sQuery(id+"F0.wireOp",EDGE,"E7.28.5");var subQ450=sQuery(id+"F0.wireOp",EDGE,"E7.30.6");var subQ451=sQuery(id+"F0.wireOp",EDGE,"E7.29.0");var subQ452=sQuery(id+"F0.wireOp",EDGE,"E7.29.1");var subQ453=sQuery(id+"F0.wireOp",EDGE,"E7.29.2");var subQ454=sQuery(id+"F0.wireOp",EDGE,"E7.29.3");var subQ455=sQuery(id+"F0.wireOp",EDGE,"E7.29.4");var subQ456=sQuery(id+"F0.wireOp",EDGE,"E7.29.5");var subQ457=sQuery(id+"F0.wireOp",EDGE,"E7.31.6");var subQ458=sQuery(id+"F0.wireOp",EDGE,"E7.30.0");var subQ459=sQuery(id+"F0.wireOp",EDGE,"E7.30.1");var subQ460=sQuery(id+"F0.wireOp",EDGE,"E7.30.2");var subQ461=sQuery(id+"F0.wireOp",EDGE,"E7.30.3");var subQ462=sQuery(id+"F0.wireOp",EDGE,"E7.30.4");var subQ463=sQuery(id+"F0.wireOp",EDGE,"E7.30.5");var subQ464=sQuery(id+"F0.wireOp",EDGE,"E7.32.6");var subQ465=sQuery(id+"F0.wireOp",EDGE,"E7.31.0");var subQ466=sQuery(id+"F0.wireOp",EDGE,"E7.31.1");var subQ467=sQuery(id+"F0.wireOp",EDGE,"E7.31.2");var subQ468=sQuery(id+"F0.wireOp",EDGE,"E7.31.3");var subQ469=sQuery(id+"F0.wireOp",EDGE,"E7.31.4");var subQ470=sQuery(id+"F0.wireOp",EDGE,"E7.31.5");var subQ471=sQuery(id+"F0.wireOp",EDGE,"E7.33.6");var subQ472=sQuery(id+"F0.wireOp",EDGE,"E7.32.0");var subQ473=sQuery(id+"F0.wireOp",EDGE,"E7.32.1");var subQ474=sQuery(id+"F0.wireOp",EDGE,"E7.32.2");var subQ475=sQuery(id+"F0.wireOp",EDGE,"E7.32.3");var subQ476=sQuery(id+"F0.wireOp",EDGE,"E7.32.4");var subQ477=sQuery(id+"F0.wireOp",EDGE,"E7.67.5");var subQ478=sQuery(id+"F0.wireOp",EDGE,"E7.69.6");var subQ479=sQuery(id+"F0.wireOp",EDGE,"E7.68.0");var subQ480=sQuery(id+"F0.wireOp",EDGE,"E7.68.1");var subQ481=sQuery(id+"F0.wireOp",EDGE,"E7.68.2");var subQ482=sQuery(id+"F0.wireOp",EDGE,"E7.68.3");var subQ483=sQuery(id+"F0.wireOp",EDGE,"E7.68.4");var subQ484=sQuery(id+"F0.wireOp",EDGE,"E7.68.5");var subQ485=sQuery(id+"F0.wireOp",EDGE,"E7.70.6");var subQ486=sQuery(id+"F0.wireOp",EDGE,"E7.69.0");var subQ487=sQuery(id+"F0.wireOp",EDGE,"E7.69.1");var subQ488=sQuery(id+"F0.wireOp",EDGE,"E7.69.2");var subQ489=sQuery(id+"F0.wireOp",EDGE,"E7.69.3");var subQ490=sQuery(id+"F0.wireOp",EDGE,"E7.69.4");var subQ491=sQuery(id+"F0.wireOp",EDGE,"E7.69.5");var subQ492=sQuery(id+"F0.wireOp",EDGE,"E7.71.6");var subQ493=sQuery(id+"F0.wireOp",EDGE,"E7.70.0");var subQ494=sQuery(id+"F0.wireOp",EDGE,"E7.70.1");var subQ495=sQuery(id+"F0.wireOp",EDGE,"E7.70.2");var subQ496=sQuery(id+"F0.wireOp",EDGE,"E7.70.3");var subQ497=sQuery(id+"F0.wireOp",EDGE,"E7.70.4");var subQ498=sQuery(id+"F0.wireOp",EDGE,"E7.70.5");var subQ499=sQuery(id+"F0.wireOp",EDGE,"E7.72.6");var subQ500=sQuery(id+"F0.wireOp",EDGE,"E7.71.0");var subQ501=sQuery(id+"F0.wireOp",EDGE,"E7.71.1");var subQ502=sQuery(id+"F0.wireOp",EDGE,"E7.71.2");var subQ503=sQuery(id+"F0.wireOp",EDGE,"E7.71.3");var subQ504=sQuery(id+"F0.wireOp",EDGE,"E7.71.4");var subQ505=sQuery(id+"F0.wireOp",EDGE,"E7.71.5");var subQ506=sQuery(id+"F0.wireOp",EDGE,"E7.73.6");var subQ507=sQuery(id+"F0.wireOp",EDGE,"E7.72.0");var subQ508=sQuery(id+"F0.wireOp",EDGE,"E7.72.1");var subQ509=sQuery(id+"F0.wireOp",EDGE,"E7.72.2");var subQ510=sQuery(id+"F0.wireOp",EDGE,"E7.72.3");var subQ511=sQuery(id+"F0.wireOp",EDGE,"E7.72.4");var subQ512=sQuery(id+"F0.wireOp",EDGE,"E7.72.5");var subQ513=sQuery(id+"F0.wireOp",EDGE,"E7.74.6");var subQ514=sQuery(id+"F0.wireOp",EDGE,"E7.73.0");var subQ515=sQuery(id+"F0.wireOp",EDGE,"E7.73.1");var subQ516=sQuery(id+"F0.wireOp",EDGE,"E7.73.2");var subQ517=sQuery(id+"F0.wireOp",EDGE,"E7.73.3");var subQ518=sQuery(id+"F0.wireOp",EDGE,"E7.73.4");var subQ519=sQuery(id+"F0.wireOp",EDGE,"E7.73.5");var subQ520=sQuery(id+"F0.wireOp",EDGE,"E7.75.6");var subQ521=sQuery(id+"F0.wireOp",EDGE,"E7.74.0");var subQ522=sQuery(id+"F0.wireOp",EDGE,"E7.74.1");var subQ523=sQuery(id+"F0.wireOp",EDGE,"E7.74.2");var subQ524=sQuery(id+"F0.wireOp",EDGE,"E7.74.3");var subQ525=sQuery(id+"F0.wireOp",EDGE,"E7.74.4");var subQ526=sQuery(id+"F0.wireOp",EDGE,"E7.74.5");var subQ527=sQuery(id+"F0.wireOp",EDGE,"E7.76.6");var subQ528=sQuery(id+"F0.wireOp",EDGE,"E7.75.0");var subQ529=sQuery(id+"F0.wireOp",EDGE,"E7.75.1");var subQ530=sQuery(id+"F0.wireOp",EDGE,"E7.75.2");var subQ531=sQuery(id+"F0.wireOp",EDGE,"E7.75.3");var subQ532=sQuery(id+"F0.wireOp",EDGE,"E7.75.4");var subQ533=sQuery(id+"F0.wireOp",EDGE,"E7.75.5");var subQ534=sQuery(id+"F0.wireOp",EDGE,"E7.77.6");var subQ535=sQuery(id+"F0.wireOp",EDGE,"E7.76.0");var subQ536=sQuery(id+"F0.wireOp",EDGE,"E7.76.1");var subQ537=sQuery(id+"F0.wireOp",EDGE,"E7.76.2");var subQ538=sQuery(id+"F0.wireOp",EDGE,"E7.76.3");var subQ539=sQuery(id+"F0.wireOp",EDGE,"E7.76.4");var subQ540=sQuery(id+"F0.wireOp",EDGE,"E7.76.5");var subQ541=sQuery(id+"F0.wireOp",EDGE,"E7.78.6");var subQ542=sQuery(id+"F0.wireOp",EDGE,"E7.77.0");var subQ543=sQuery(id+"F0.wireOp",EDGE,"E7.77.1");var subQ544=sQuery(id+"F0.wireOp",EDGE,"E7.77.2");var subQ545=sQuery(id+"F0.wireOp",EDGE,"E7.77.3");var subQ546=sQuery(id+"F0.wireOp",EDGE,"E7.77.4");var subQ547=sQuery(id+"F0.wireOp",EDGE,"E7.77.5");var subQ548=sQuery(id+"F0.wireOp",EDGE,"E7.79.6");var subQ549=sQuery(id+"F0.wireOp",EDGE,"E7.78.0");var subQ550=sQuery(id+"F0.wireOp",EDGE,"E7.78.1");var subQ551=sQuery(id+"F0.wireOp",EDGE,"E7.78.2");var subQ552=sQuery(id+"F0.wireOp",EDGE,"E7.78.3");var subQ553=sQuery(id+"F0.wireOp",EDGE,"E7.78.4");var subQ554=sQuery(id+"F0.wireOp",EDGE,"E7.78.5");var subQ555=sQuery(id+"F0.wireOp",EDGE,"E7.80.6");var subQ556=sQuery(id+"F0.wireOp",EDGE,"E7.79.0");var subQ557=sQuery(id+"F0.wireOp",EDGE,"E7.79.1");var subQ558=sQuery(id+"F0.wireOp",EDGE,"E7.79.2");var subQ559=sQuery(id+"F0.wireOp",EDGE,"E7.79.3");var subQ560=sQuery(id+"F0.wireOp",EDGE,"E7.79.4");var subQ561=sQuery(id+"F0.wireOp",EDGE,"E7.79.5");var subQ562=sQuery(id+"F0.wireOp",EDGE,"E7.81.6");var subQ563=sQuery(id+"F0.wireOp",EDGE,"E7.80.0");var subQ564=sQuery(id+"F0.wireOp",EDGE,"E7.80.1");var subQ565=sQuery(id+"F0.wireOp",EDGE,"E7.80.2");var subQ566=sQuery(id+"F0.wireOp",EDGE,"E7.80.3");var subQ567=sQuery(id+"F0.wireOp",EDGE,"E7.80.4");var subQ568=sQuery(id+"F0.wireOp",EDGE,"E7.80.5");var subQ569=sQuery(id+"F0.wireOp",EDGE,"E7.82.6");var subQ570=sQuery(id+"F0.wireOp",EDGE,"E7.81.0");var subQ571=sQuery(id+"F0.wireOp",EDGE,"E7.81.1");var subQ572=sQuery(id+"F0.wireOp",EDGE,"E7.81.2");var subQ573=sQuery(id+"F0.wireOp",EDGE,"E7.81.3");var subQ574=sQuery(id+"F0.wireOp",EDGE,"E7.81.4");var subQ575=sQuery(id+"F0.wireOp",EDGE,"E7.81.5");var subQ576=sQuery(id+"F0.wireOp",EDGE,"E7.83.6");var subQ577=sQuery(id+"F0.wireOp",EDGE,"E7.82.0");var subQ578=sQuery(id+"F0.wireOp",EDGE,"E7.82.1");var subQ579=sQuery(id+"F0.wireOp",EDGE,"E7.82.2");var subQ580=sQuery(id+"F0.wireOp",EDGE,"E7.82.3");var subQ581=sQuery(id+"F0.wireOp",EDGE,"E7.82.4");var subQ582=sQuery(id+"F0.wireOp",EDGE,"E7.82.5");var subQ583=sQuery(id+"F0.wireOp",EDGE,"E7.84.6");var subQ584=sQuery(id+"F0.wireOp",EDGE,"E7.83.0");var subQ585=sQuery(id+"F0.wireOp",EDGE,"E7.83.1");var subQ586=sQuery(id+"F0.wireOp",EDGE,"E7.83.2");var subQ587=sQuery(id+"F0.wireOp",EDGE,"E7.83.3");var subQ588=sQuery(id+"F0.wireOp",EDGE,"E7.83.4");var subQ589=sQuery(id+"F0.wireOp",EDGE,"E7.83.5");var subQ590=sQuery(id+"F0.wireOp",EDGE,"E7.85.6");var subQ591=sQuery(id+"F0.wireOp",EDGE,"E7.84.0");var subQ592=sQuery(id+"F0.wireOp",EDGE,"E7.84.1");var subQ593=sQuery(id+"F0.wireOp",EDGE,"E7.84.2");var subQ594=sQuery(id+"F0.wireOp",EDGE,"E7.84.3");var subQ595=sQuery(id+"F0.wireOp",EDGE,"E7.84.4");var subQ596=sQuery(id+"F0.wireOp",EDGE,"E7.84.5");var subQ597=sQuery(id+"F0.wireOp",EDGE,"E7.86.6");var subQ598=sQuery(id+"F0.wireOp",EDGE,"E7.85.0");var subQ599=sQuery(id+"F0.wireOp",EDGE,"E7.85.1");var subQ600=sQuery(id+"F0.wireOp",EDGE,"E7.85.2");var subQ601=sQuery(id+"F0.wireOp",EDGE,"E7.85.3");var subQ602=sQuery(id+"F0.wireOp",EDGE,"E7.85.4");var subQ603=sQuery(id+"F0.wireOp",EDGE,"E7.85.5");var subQ604=sQuery(id+"F0.wireOp",EDGE,"E7.87.6");var subQ605=sQuery(id+"F0.wireOp",EDGE,"E7.86.0");var subQ606=sQuery(id+"F0.wireOp",EDGE,"E7.86.1");var subQ607=sQuery(id+"F0.wireOp",EDGE,"E7.86.2");var subQ608=sQuery(id+"F0.wireOp",EDGE,"E7.86.3");var subQ609=sQuery(id+"F0.wireOp",EDGE,"E7.86.4");var subQ610=sQuery(id+"F0.wireOp",EDGE,"E7.86.5");var subQ611=sQuery(id+"F0.wireOp",EDGE,"E7.88.6");var subQ612=sQuery(id+"F0.wireOp",EDGE,"E7.87.0");var subQ613=sQuery(id+"F0.wireOp",EDGE,"E7.87.1");var subQ614=sQuery(id+"F0.wireOp",EDGE,"E7.87.2");var subQ615=sQuery(id+"F0.wireOp",EDGE,"E7.87.3");var subQ616=sQuery(id+"F0.wireOp",EDGE,"E7.87.4");var subQ617=sQuery(id+"F0.wireOp",EDGE,"E7.87.5");var subQ618=sQuery(id+"F0.wireOp",EDGE,"E7.89.6");var subQ619=sQuery(id+"F0.wireOp",EDGE,"E7.88.0");var subQ620=sQuery(id+"F0.wireOp",EDGE,"E7.88.1");var subQ621=sQuery(id+"F0.wireOp",EDGE,"E7.88.2");var subQ622=sQuery(id+"F0.wireOp",EDGE,"E7.88.3");var subQ623=sQuery(id+"F0.wireOp",EDGE,"E7.88.4");var subQ624=sQuery(id+"F0.wireOp",EDGE,"E7.88.5");var subQ625=sQuery(id+"F0.wireOp",EDGE,"E7.90.6");var subQ626=sQuery(id+"F0.wireOp",EDGE,"E7.89.0");var subQ627=sQuery(id+"F0.wireOp",EDGE,"E7.89.1");var subQ628=sQuery(id+"F0.wireOp",EDGE,"E7.89.2");var subQ629=sQuery(id+"F0.wireOp",EDGE,"E7.89.3");var subQ630=sQuery(id+"F0.wireOp",EDGE,"E7.89.4");var subQ631=sQuery(id+"F0.wireOp",EDGE,"E7.89.5");var subQ632=sQuery(id+"F0.wireOp",EDGE,"E7.91.6");var subQ633=sQuery(id+"F0.wireOp",EDGE,"E7.90.0");var subQ634=sQuery(id+"F0.wireOp",EDGE,"E7.90.1");var subQ635=sQuery(id+"F0.wireOp",EDGE,"E7.90.2");var subQ636=sQuery(id+"F0.wireOp",EDGE,"E7.90.3");var subQ637=sQuery(id+"F0.wireOp",EDGE,"E7.90.4");var subQ638=sQuery(id+"F0.wireOp",EDGE,"E7.90.5");var subQ639=sQuery(id+"F0.wireOp",EDGE,"E7.92.6");var subQ640=sQuery(id+"F0.wireOp",EDGE,"E7.91.0");var subQ641=sQuery(id+"F0.wireOp",EDGE,"E7.91.1");var subQ642=sQuery(id+"F0.wireOp",EDGE,"E7.91.2");var subQ643=sQuery(id+"F0.wireOp",EDGE,"E7.91.3");var subQ644=sQuery(id+"F0.wireOp",EDGE,"E7.91.4");var subQ645=sQuery(id+"F0.wireOp",EDGE,"E7.91.5");var subQ646=sQuery(id+"F0.wireOp",EDGE,"E7.93.6");var subQ647=sQuery(id+"F0.wireOp",EDGE,"E7.92.0");var subQ648=sQuery(id+"F0.wireOp",EDGE,"E7.92.1");var subQ649=sQuery(id+"F0.wireOp",EDGE,"E7.92.2");var subQ650=sQuery(id+"F0.wireOp",EDGE,"E7.92.3");var subQ651=sQuery(id+"F0.wireOp",EDGE,"E7.92.4");var subQ652=sQuery(id+"F0.wireOp",EDGE,"E7.92.5");var subQ653=sQuery(id+"F0.wireOp",EDGE,"E7.94.6");var subQ654=sQuery(id+"F0.wireOp",EDGE,"E7.93.0");var subQ655=sQuery(id+"F0.wireOp",EDGE,"E7.93.1");var subQ656=sQuery(id+"F0.wireOp",EDGE,"E7.93.2");var subQ657=sQuery(id+"F0.wireOp",EDGE,"E7.93.3");var subQ658=sQuery(id+"F0.wireOp",EDGE,"E7.93.4");var subQ659=sQuery(id+"F0.wireOp",EDGE,"E7.93.5");var subQ660=sQuery(id+"F0.wireOp",EDGE,"E7.95.6");var subQ661=sQuery(id+"F0.wireOp",EDGE,"E7.94.0");var subQ662=sQuery(id+"F0.wireOp",EDGE,"E7.94.1");var subQ663=sQuery(id+"F0.wireOp",EDGE,"E7.94.2");var subQ664=sQuery(id+"F0.wireOp",EDGE,"E7.94.3");var subQ665=sQuery(id+"F0.wireOp",EDGE,"E7.94.4");var subQ666=sQuery(id+"F0.wireOp",EDGE,"E7.94.5");var subQ667=sQuery(id+"F0.wireOp",EDGE,"E7.95.1");var subQ668=sQuery(id+"F0.wireOp",EDGE,"E7.95.2");var subQ669=sQuery(id+"F0.wireOp",EDGE,"E7.95.3");var subQ670=sQuery(id+"F0.wireOp",EDGE,"E7.95.4");var subQ671=sQuery(id+"F0.wireOp",EDGE,"E7.95.5");Q0=makeQuery(id+"F5.boolean.opBoolean","SPLIT",FACE,{"disambiguationData":[TD([makeQuery(id+"F1.opExtrude","SWEPT_FACE",FACE,{"disambiguationData":[OSD([subQ318])]})])],"derivedFrom":makeQuery(id+"F1.opExtrude","CAP_FACE",FACE,{"disambiguationData":[OSD([subQ322,subQ320,subQ318,subQ317,subQ323,subQ324,subQ325,subQ327,subQ328,subQ329,subQ316,subQ315,subQ314,subQ321,subQ313,subQ311,subQ310,subQ309,subQ308,subQ307,subQ326,subQ306,subQ304,subQ303,subQ330,subQ331,subQ332,subQ312,subQ334,subQ335,subQ336,subQ337,subQ338,subQ339,subQ305,subQ341,subQ342,subQ343,subQ344,subQ345,subQ346,subQ333,subQ348,subQ349,subQ350,subQ351,subQ352,subQ353,subQ340,subQ355,subQ356,subQ357,subQ302,subQ301,subQ300,subQ347,subQ299,subQ297,subQ296,subQ295,subQ294,subQ293,subQ354,subQ292,subQ290,subQ289,subQ288,subQ287,subQ286,subQ298,subQ285,subQ283,subQ282,subQ281,subQ280,subQ279,subQ291,subQ278,subQ276,subQ275,subQ274,subQ273,subQ272,subQ284,subQ271,subQ269,subQ268,subQ267,subQ266,subQ265,subQ277,subQ264,subQ262,subQ261,subQ260,subQ259,subQ258,subQ270,subQ257,subQ255,subQ254,subQ253,subQ252,subQ251,subQ263,subQ250,subQ248,subQ247,subQ246,subQ245,subQ358,subQ256,subQ360,subQ361,subQ362,subQ363,subQ364,subQ365,subQ249,subQ367,subQ368,subQ369,subQ370,subQ371,subQ372,subQ359,subQ374,subQ375,subQ376,subQ377,subQ378,subQ379,subQ366,subQ381,subQ382,subQ383,subQ384,subQ385,subQ386,subQ373,subQ388,subQ389,subQ390,subQ391,subQ392,subQ393,subQ380,subQ395,subQ396,subQ397,subQ398,subQ399,subQ400,subQ387,subQ402,subQ403,subQ404,subQ405,subQ406,subQ407,subQ394,subQ409,subQ410,subQ411,subQ412,subQ413,subQ414,subQ401,subQ416,subQ417,subQ418,subQ419,subQ420,subQ421,subQ408,subQ423,subQ424,subQ425,subQ426,subQ427,subQ428,subQ415,subQ430,subQ431,subQ432,subQ433,subQ434,subQ435,subQ422,subQ437,subQ438,subQ439,subQ440,subQ441,subQ442,subQ429,subQ444,subQ445,subQ446,subQ447,subQ448,subQ449,subQ436,subQ451,subQ452,subQ453,subQ454,subQ455,subQ456,subQ443,subQ458,subQ459,subQ460,subQ461,subQ462,subQ463,subQ450,subQ465,subQ466,subQ467,subQ468,subQ469,subQ470,subQ457,subQ472,subQ473,subQ474,subQ475,subQ476,subQ244,subQ464,subQ243,subQ241,subQ240,subQ239,subQ238,subQ237,subQ471,subQ236,subQ234,subQ233,subQ232,subQ231,subQ230,subQ242,subQ229,subQ227,subQ226,subQ225,subQ224,subQ223,subQ235,subQ222,subQ220,subQ219,subQ218,subQ217,subQ216,subQ228,subQ215,subQ213,subQ212,subQ211,subQ210,subQ209,subQ221,subQ208,subQ206,subQ205,subQ204,subQ203,subQ202,subQ214,subQ201,subQ199,subQ198,subQ197,subQ196,subQ195,subQ207,subQ194,subQ192,subQ191,subQ190,subQ189,subQ188,subQ200,subQ187,subQ185,subQ184,subQ183,subQ182,subQ181,subQ193,subQ180,subQ178,subQ177,subQ176,subQ175,subQ174,subQ186,subQ173,subQ171,subQ170,subQ169,subQ168,subQ167,subQ179,subQ166,subQ164,subQ163,subQ162,subQ161,subQ160,subQ172,subQ159,subQ157,subQ156,subQ155,subQ154,subQ153,subQ165,subQ152,subQ150,subQ149,subQ148,subQ147,subQ146,subQ158,subQ145,subQ143,subQ142,subQ141,subQ140,subQ139,subQ151,subQ138,subQ136,subQ135,subQ134,subQ133,subQ132,subQ144,subQ131,subQ129,subQ128,subQ127,subQ126,subQ125,subQ137,subQ124,subQ122,subQ121,subQ120,subQ119,subQ118,subQ130,subQ117,subQ115,subQ114,subQ113,subQ112,subQ111,subQ123,subQ110,subQ108,subQ107,subQ106,subQ105,subQ104,subQ116,subQ103,subQ101,subQ100,subQ99,subQ98,subQ97,subQ109,subQ96,subQ94,subQ93,subQ92,subQ91,subQ90,subQ102,subQ89,subQ87,subQ86,subQ85,subQ84,subQ83,subQ95,subQ82,subQ80,subQ79,subQ78,subQ77,subQ76,subQ88,subQ75,subQ73,subQ72,subQ71,subQ70,subQ69,subQ81,subQ68,subQ66,subQ65,subQ64,subQ63,subQ62,subQ74,subQ61,subQ59,subQ58,subQ57,subQ56,subQ55,subQ67,subQ54,subQ52,subQ51,subQ50,subQ49,subQ48,subQ60,subQ47,subQ45,subQ44,subQ43,subQ42,subQ41,subQ53,subQ40,subQ38,subQ37,subQ36,subQ35,subQ34,subQ46,subQ33,subQ31,subQ30,subQ29,subQ28,subQ27,subQ39,subQ26,subQ24,subQ23,subQ22,subQ21,subQ20,subQ32,subQ19,subQ17,subQ16,subQ15,subQ14,subQ13,subQ25,subQ12,subQ10,subQ9,subQ8,subQ7,subQ6,subQ18,subQ5,subQ3,subQ2,subQ1,subQ0,subQ477,subQ11,subQ479,subQ480,subQ481,subQ482,subQ483,subQ484,subQ4,subQ486,subQ487,subQ488,subQ489,subQ490,subQ491,subQ478,subQ493,subQ494,subQ495,subQ496,subQ497,subQ498,subQ485,subQ500,subQ501,subQ502,subQ503,subQ504,subQ505,subQ492,subQ507,subQ508,subQ509,subQ510,subQ511,subQ512,subQ499,subQ514,subQ515,subQ516,subQ517,subQ518,subQ519,subQ506,subQ521,subQ522,subQ523,subQ524,subQ525,subQ526,subQ513,subQ528,subQ529,subQ530,subQ531,subQ532,subQ533,subQ520,subQ535,subQ536,subQ537,subQ538,subQ539,subQ540,subQ527,subQ542,subQ543,subQ544,subQ545,subQ546,subQ547,subQ534,subQ549,subQ550,subQ551,subQ552,subQ553,subQ554,subQ541,subQ556,subQ557,subQ558,subQ559,subQ560,subQ561,subQ548,subQ563,subQ564,subQ565,subQ566,subQ567,subQ568,subQ555,subQ570,subQ571,subQ572,subQ573,subQ574,subQ575,subQ562,subQ577,subQ578,subQ579,subQ580,subQ581,subQ582,subQ569,subQ584,subQ585,subQ586,subQ587,subQ588,subQ589,subQ576,subQ591,subQ592,subQ593,subQ594,subQ595,subQ596,subQ583,subQ598,subQ599,subQ600,subQ601,subQ602,subQ603,subQ590,subQ605,subQ606,subQ607,subQ608,subQ609,subQ610,subQ597,subQ612,subQ613,subQ614,subQ615,subQ616,subQ617,subQ604,subQ619,subQ620,subQ621,subQ622,subQ623,subQ624,subQ611,subQ626,subQ627,subQ628,subQ629,subQ630,subQ631,subQ618,subQ633,subQ634,subQ635,subQ636,subQ637,subQ638,subQ625,subQ640,subQ641,subQ642,subQ643,subQ644,subQ645,subQ632,subQ647,subQ648,subQ649,subQ650,subQ651,subQ652,subQ639,subQ654,subQ655,subQ656,subQ657,subQ658,subQ659,subQ646,subQ661,subQ662,subQ663,subQ664,subQ665,subQ666,subQ653,subQ319,subQ667,subQ668,subQ669,subQ670,subQ671,subQ660])],"isStart":true})});}
            var sketch = newSketch(context, id + "F6", { "sketchPlane" : qUnion([Q0])});
            skCircle(sketch, "E11", {"center": v(0, 0) * mm, "radius": 19.05 * mm});
            skSolve(sketch);
        }
        {
            var Q0;
            Q0=makeQuery(id+"F6.imprint","IMPRINT",FACE,{"disambiguationData":[TD([[makeQuery(id+"F6.imprint","IMPRINT",EDGE,{"derivedFrom":makeQuery(id+"F5.opExtrude","CAP_EDGE",EDGE,{"disambiguationData":[OSD([sQuery(id+"F4.wireOp",EDGE,"E9.0")])],"isStart":true})}),-1.0]])]});
            var Q1;
            Q1=makeQuery(id+"F6.imprint","IMPRINT",FACE,{"disambiguationData":[TD([[makeQuery(id+"F6.imprint","IMPRINT",EDGE,{"derivedFrom":sQuery(id+"F6.wireOp",EDGE,"E11")}),1.0]])]});
            extrude(context, id + "F7", {"entities" : qUnion([Q0, Q1]), "operationType" : NewBodyOperationType.ADD, "depth" : 12.7 * mm, "offsetDistance" : 25.4 * mm});
        }
        {
            var Q0;
            Q0=makeQuery(id+"F3.opExtrude","CAP_FACE",FACE,{"disambiguationData":[OSD([sQuery(id+"F2.wireOp",EDGE,"E8")])],"isStart":false});
            var sketch = newSketch(context, id + "F8", { "sketchPlane" : qUnion([Q0])});
            skCircle(sketch, "E12", {"center": v(0, 0) * mm, "radius": 11.11 * mm});
            skSolve(sketch);
        }
        {
            var Q0;
            Q0 = qSketchRegion(id + "F8", true);
            extrude(context, id + "F9", {"entities" : qUnion([Q0]), "operationType" : NewBodyOperationType.REMOVE, "oppositeDirection" : true, "depth" : 17.14 * mm, "offsetDistance" : 25.4 * mm});
        }
        {
            var Q0;
            Q0=makeQuery(id+"F3.opExtrude","CAP_FACE",FACE,{"disambiguationData":[OSD([sQuery(id+"F2.wireOp",EDGE,"E8")])],"isStart":false});
            var sketch = newSketch(context, id + "F10", { "sketchPlane" : qUnion([Q0])});
            skPoint(sketch, "E13.center.orphan", {"position": v(1.83, 0) * mm});
            skCircle(sketch, "E14", {"center": v(0, 0) * mm, "radius": 13.33 * mm});
            skSolve(sketch);
        }
        {
            var Q0;
            Q0 = qSketchRegion(id + "F10", true);
            extrude(context, id + "F11", {"entities" : qUnion([Q0]), "operationType" : NewBodyOperationType.REMOVE, "oppositeDirection" : true, "depth" : 1 * mm, "offsetDistance" : 25.4 * mm});
        }
    });
